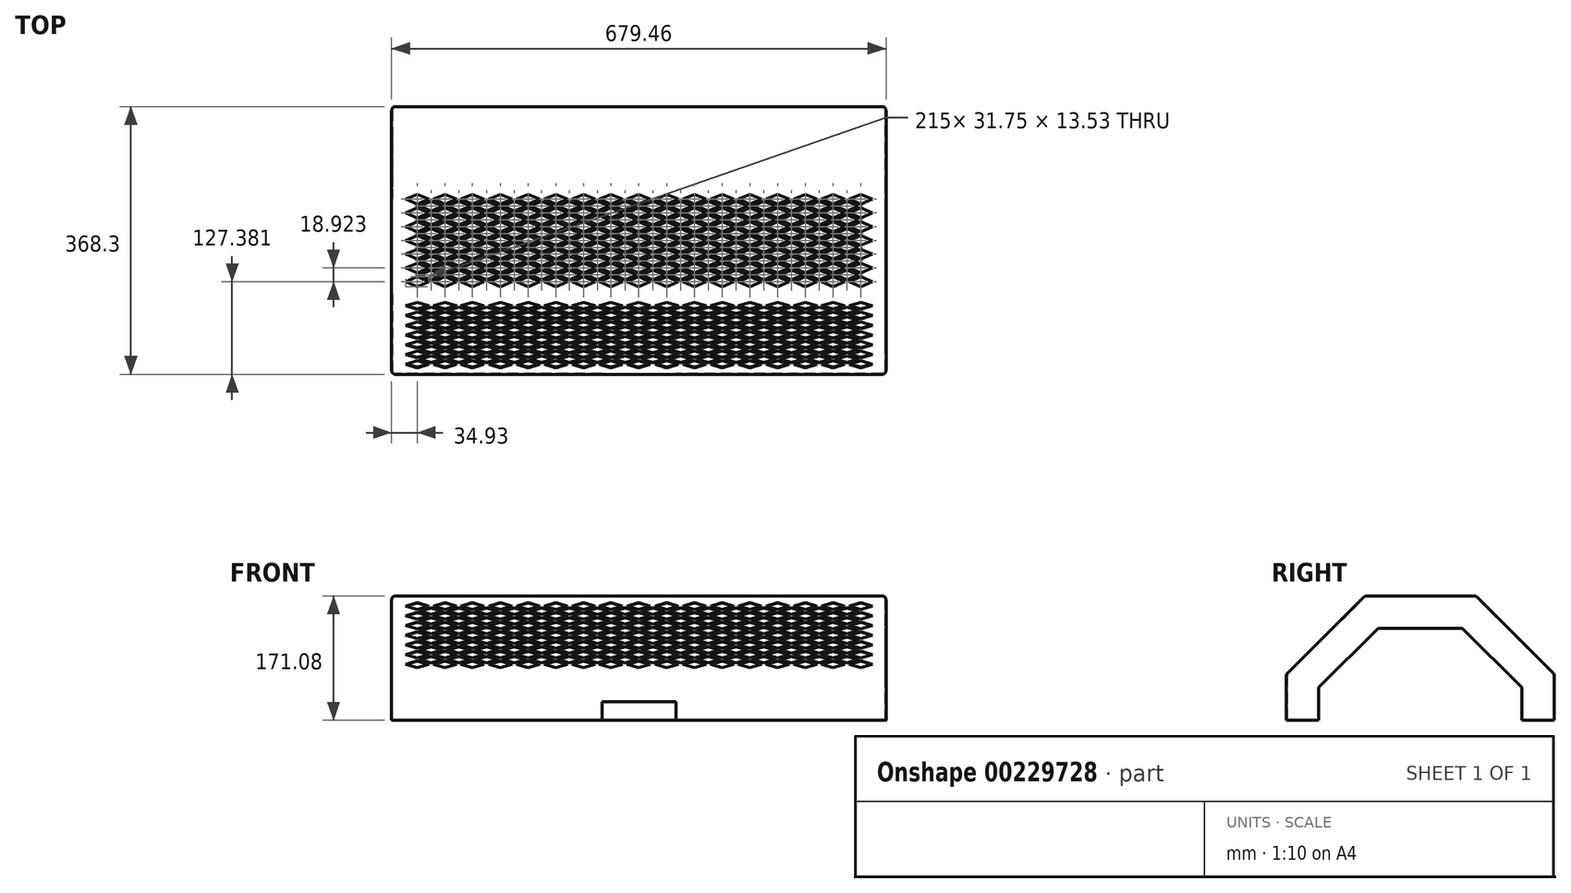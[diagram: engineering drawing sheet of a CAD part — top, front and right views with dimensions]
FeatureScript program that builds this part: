
annotation { "Feature Type Name" : "Feature", "Feature Type Description" : "" }
export const myFeature = defineFeature(function(context is Context, id is Id, definition is map)
    precondition{}
    {
        {
            var Q0;
            Q0=qCreatedBy(makeId("Right.planeOp"),FACE);
            var sketch = newSketch(context, id + "F0", { "sketchPlane" : qUnion([Q0])});
            skLineSegment(sketch, "E0", {"start": v(0, 0) * mm, "end": v(0, 333.95) * mm, "construction": true});
            skLineSegment(sketch, "E1", {"start": v(184.15, 0) * mm, "end": v(184.15, 63.5) * mm});
            skLineSegment(sketch, "E2", {"start": v(184.15, 63.5) * mm, "end": v(76.2, 171.08) * mm});
            skLineSegment(sketch, "E3", {"start": v(76.2, 171.08) * mm, "end": v(0, 171.08) * mm});
            skLineSegment(sketch, "E4", {"start": v(184.15, 0) * mm, "end": v(139.7, 0) * mm});
            skLineSegment(sketch, "E5", {"start": v(139.7, 0) * mm, "end": v(139.7, 45.04) * mm});
            skLineSegment(sketch, "E6", {"start": v(139.7, 45.04) * mm, "end": v(57.83, 126.63) * mm});
            skLineSegment(sketch, "E7", {"start": v(57.83, 126.63) * mm, "end": v(0, 126.63) * mm});
            skLineSegment(sketch, "E8.MirrorCS", {"start": v(-139.7, 45.04) * mm, "end": v(-57.83, 126.63) * mm});
            skLineSegment(sketch, "E9.MirrorCS", {"start": v(-184.15, 0) * mm, "end": v(-184.15, 63.5) * mm});
            skLineSegment(sketch, "E10.MirrorCS", {"start": v(-139.7, 0) * mm, "end": v(-139.7, 45.04) * mm});
            skLineSegment(sketch, "E11.MirrorCS", {"start": v(-76.2, 171.08) * mm, "end": v(0, 171.08) * mm});
            skLineSegment(sketch, "E12.MirrorCS", {"start": v(-57.83, 126.63) * mm, "end": v(0, 126.63) * mm});
            skLineSegment(sketch, "E13.MirrorCS", {"start": v(-184.15, 63.5) * mm, "end": v(-76.2, 171.08) * mm});
            skLineSegment(sketch, "E14.MirrorCS", {"start": v(-184.15, 0) * mm, "end": v(-139.7, 0) * mm});
            skSolve(sketch);
        }
        {
            var Q0;
            Q0 = qSketchRegion(id + "F0", true);
            extrude(context, id + "F1", {"entities" : qUnion([Q0]), "endBound" : BoundingType.SYMMETRIC, "depth" : 679.45 * mm});
        }
        {
            var Q0;
            Q0=makeQuery(id+"F1.opExtrude","SWEPT_EDGE",EDGE,{"disambiguationData":[OSD([sQuery(id+"F0.wireOp",EDGE,"E11.MirrorCS"),sQuery(id+"F0.wireOp",EDGE,"E13.MirrorCS")])]});
            var Q1;
            Q1=makeQuery(id+"F1.opExtrude","SWEPT_EDGE",EDGE,{"disambiguationData":[OSD([sQuery(id+"F0.wireOp",EDGE,"E2"),sQuery(id+"F0.wireOp",EDGE,"E3")])]});
            var Q2;
            Q2=makeQuery(id+"F1.opExtrude","SWEPT_EDGE",EDGE,{"disambiguationData":[OSD([sQuery(id+"F0.wireOp",EDGE,"E1"),sQuery(id+"F0.wireOp",EDGE,"E2")])]});
            var Q3;
            Q3=makeQuery(id+"F1.opExtrude","CAP_EDGE",EDGE,{"disambiguationData":[OSD([sQuery(id+"F0.wireOp",EDGE,"E1")])],"isStart":false});
            var Q4;
            Q4=makeQuery(id+"F1.opExtrude","CAP_EDGE",EDGE,{"disambiguationData":[OSD([sQuery(id+"F0.wireOp",EDGE,"E2")])],"isStart":false});
            var Q5;
            Q5=makeQuery(id+"F1.opExtrude","CAP_EDGE",EDGE,{"disambiguationData":[OSD([sQuery(id+"F0.wireOp",EDGE,"E3"),sQuery(id+"F0.wireOp",EDGE,"E11.MirrorCS")])],"isStart":false});
            var Q6;
            Q6=makeQuery(id+"F1.opExtrude","SWEPT_EDGE",EDGE,{"disambiguationData":[OSD([sQuery(id+"F0.wireOp",EDGE,"E9.MirrorCS"),sQuery(id+"F0.wireOp",EDGE,"E13.MirrorCS")])]});
            var Q7;
            Q7=makeQuery(id+"F1.opExtrude","CAP_EDGE",EDGE,{"disambiguationData":[OSD([sQuery(id+"F0.wireOp",EDGE,"E13.MirrorCS")])],"isStart":false});
            var Q8;
            Q8=makeQuery(id+"F1.opExtrude","CAP_EDGE",EDGE,{"disambiguationData":[OSD([sQuery(id+"F0.wireOp",EDGE,"E9.MirrorCS")])],"isStart":false});
            var Q9;
            Q9=makeQuery(id+"F1.opExtrude","CAP_EDGE",EDGE,{"disambiguationData":[OSD([sQuery(id+"F0.wireOp",EDGE,"E1")])],"isStart":true});
            var Q10;
            Q10=makeQuery(id+"F1.opExtrude","CAP_EDGE",EDGE,{"disambiguationData":[OSD([sQuery(id+"F0.wireOp",EDGE,"E2")])],"isStart":true});
            var Q11;
            Q11=makeQuery(id+"F1.opExtrude","CAP_EDGE",EDGE,{"disambiguationData":[OSD([sQuery(id+"F0.wireOp",EDGE,"E3"),sQuery(id+"F0.wireOp",EDGE,"E11.MirrorCS")])],"isStart":true});
            var Q12;
            Q12=makeQuery(id+"F1.opExtrude","CAP_EDGE",EDGE,{"disambiguationData":[OSD([sQuery(id+"F0.wireOp",EDGE,"E13.MirrorCS")])],"isStart":true});
            var Q13;
            Q13=makeQuery(id+"F1.opExtrude","CAP_EDGE",EDGE,{"disambiguationData":[OSD([sQuery(id+"F0.wireOp",EDGE,"E9.MirrorCS")])],"isStart":true});
            fillet(context, id + "F2", {"entities" : qUnion([Q0, Q1, Q2, Q3, Q4, Q5, Q6, Q7, Q8, Q9, Q10, Q11, Q12, Q13]), "radius" : 5.08 * mm, "tangentPropagation" : true, "allowEdgeOverflow" : false});
        }
        {
            var Q0;
            Q0=makeQuery(id+"F1.opExtrude","SWEPT_FACE",FACE,{"disambiguationData":[OSD([sQuery(id+"F0.wireOp",EDGE,"E4")])]});
            var Q1;
            Q1=makeQuery(id+"F1.opExtrude","SWEPT_FACE",FACE,{"disambiguationData":[OSD([sQuery(id+"F0.wireOp",EDGE,"E5")])]});
            var Q2;
            Q2=makeQuery(id+"F1.opExtrude","SWEPT_FACE",FACE,{"disambiguationData":[OSD([sQuery(id+"F0.wireOp",EDGE,"E6")])]});
            var Q3;
            Q3=makeQuery(id+"F1.opExtrude","SWEPT_FACE",FACE,{"disambiguationData":[OSD([sQuery(id+"F0.wireOp",EDGE,"E7"),sQuery(id+"F0.wireOp",EDGE,"E12.MirrorCS")])]});
            var Q4;
            Q4=makeQuery(id+"F1.opExtrude","SWEPT_FACE",FACE,{"disambiguationData":[OSD([sQuery(id+"F0.wireOp",EDGE,"E8.MirrorCS")])]});
            var Q5;
            Q5=makeQuery(id+"F1.opExtrude","SWEPT_FACE",FACE,{"disambiguationData":[OSD([sQuery(id+"F0.wireOp",EDGE,"E14.MirrorCS")])]});
            var Q6;
            Q6=makeQuery(id+"F1.opExtrude","SWEPT_FACE",FACE,{"disambiguationData":[OSD([sQuery(id+"F0.wireOp",EDGE,"E10.MirrorCS")])]});
            shell(context, id + "F3", {"entities" : qUnion([Q0, Q1, Q2, Q3, Q4, Q5, Q6]), "thickness" : 0.95 * mm});
        }
        {
            var Q0;
            Q0=makeQuery(id+"F1.opExtrude","SWEPT_FACE",FACE,{"disambiguationData":[OSD([sQuery(id+"F0.wireOp",EDGE,"E9.MirrorCS")])]});
            var sketch = newSketch(context, id + "F4", { "sketchPlane" : qUnion([Q0])});
            skLineSegment(sketch, "E15.bottom", {"start": v(-50.8, 0) * mm, "end": v(50.8, 0) * mm});
            skLineSegment(sketch, "E15.top", {"start": v(-50.8, 25.4) * mm, "end": v(50.8, 25.4) * mm});
            skLineSegment(sketch, "E15.left", {"start": v(-50.8, 0) * mm, "end": v(-50.8, 25.4) * mm});
            skLineSegment(sketch, "E15.right", {"start": v(50.8, 0) * mm, "end": v(50.8, 25.4) * mm});
            skSolve(sketch);
        }
        {
            var Q0;
            Q0 = qSketchRegion(id + "F4", true);
            extrude(context, id + "F5", {"entities" : qUnion([Q0]), "operationType" : NewBodyOperationType.REMOVE, "oppositeDirection" : true, "depth" : 25.4 * mm});
        }
        {
            var Q0;
            Q0=makeQuery(id+"F1.opExtrude","SWEPT_FACE",FACE,{"disambiguationData":[OSD([sQuery(id+"F0.wireOp",EDGE,"E3"),sQuery(id+"F0.wireOp",EDGE,"E11.MirrorCS")])]});
            var sketch = newSketch(context, id + "F6", { "sketchPlane" : qUnion([Q0])});
            skLineSegment(sketch, "E16", {"start": v(-15.88, 0) * mm, "end": v(0, 6.76) * mm});
            skLineSegment(sketch, "E17", {"start": v(0, 6.76) * mm, "end": v(15.88, 0) * mm});
            skLineSegment(sketch, "E18", {"start": v(15.88, 0) * mm, "end": v(0, -6.76) * mm});
            skLineSegment(sketch, "E19", {"start": v(0, -6.76) * mm, "end": v(-15.88, 0) * mm});
            skLineSegment(sketch, "E20.0.1.0", {"start": v(15.88, 18.92) * mm, "end": v(0, 12.16) * mm});
            skLineSegment(sketch, "E20.0.1.1", {"start": v(0, 25.69) * mm, "end": v(15.88, 18.92) * mm});
            skLineSegment(sketch, "E20.0.1.2", {"start": v(-15.88, 18.92) * mm, "end": v(0, 25.69) * mm});
            skLineSegment(sketch, "E20.0.1.3", {"start": v(0, 12.16) * mm, "end": v(-15.88, 18.92) * mm});
            skLineSegment(sketch, "E20.0.2.0", {"start": v(15.88, 37.85) * mm, "end": v(0, 31.08) * mm});
            skLineSegment(sketch, "E20.0.2.1", {"start": v(0, 44.6) * mm, "end": v(15.88, 37.85) * mm});
            skLineSegment(sketch, "E20.0.2.2", {"start": v(-15.88, 37.85) * mm, "end": v(0, 44.6) * mm});
            skLineSegment(sketch, "E20.0.2.3", {"start": v(0, 31.08) * mm, "end": v(-15.87, 37.85) * mm});
            skLineSegment(sketch, "E20.0.3.0", {"start": v(15.88, 56.77) * mm, "end": v(0, 50) * mm});
            skLineSegment(sketch, "E20.0.3.1", {"start": v(0, 63.53) * mm, "end": v(15.88, 56.77) * mm});
            skLineSegment(sketch, "E20.0.3.2", {"start": v(-15.88, 56.77) * mm, "end": v(0, 63.53) * mm});
            skLineSegment(sketch, "E20.0.3.3", {"start": v(0, 50) * mm, "end": v(-15.87, 56.77) * mm});
            skLineSegment(sketch, "E20.1.0.0", {"start": v(53.98, 0) * mm, "end": v(38.1, -6.76) * mm});
            skLineSegment(sketch, "E20.1.0.1", {"start": v(38.1, 6.76) * mm, "end": v(53.98, 0) * mm});
            skLineSegment(sketch, "E20.1.0.2", {"start": v(22.22, 0) * mm, "end": v(38.1, 6.76) * mm});
            skLineSegment(sketch, "E20.1.0.3", {"start": v(38.1, -6.76) * mm, "end": v(22.23, 0) * mm});
            skLineSegment(sketch, "E20.1.1.0", {"start": v(53.98, 18.92) * mm, "end": v(38.1, 12.16) * mm});
            skLineSegment(sketch, "E20.1.1.1", {"start": v(38.1, 25.69) * mm, "end": v(53.98, 18.92) * mm});
            skLineSegment(sketch, "E20.1.1.2", {"start": v(22.22, 18.92) * mm, "end": v(38.1, 25.69) * mm});
            skLineSegment(sketch, "E20.1.1.3", {"start": v(38.1, 12.16) * mm, "end": v(22.23, 18.92) * mm});
            skLineSegment(sketch, "E20.1.2.0", {"start": v(53.98, 37.85) * mm, "end": v(38.1, 31.08) * mm});
            skLineSegment(sketch, "E20.1.2.1", {"start": v(38.1, 44.6) * mm, "end": v(53.98, 37.85) * mm});
            skLineSegment(sketch, "E20.1.2.2", {"start": v(22.22, 37.85) * mm, "end": v(38.1, 44.6) * mm});
            skLineSegment(sketch, "E20.1.2.3", {"start": v(38.1, 31.08) * mm, "end": v(22.23, 37.85) * mm});
            skLineSegment(sketch, "E20.1.3.0", {"start": v(53.98, 56.77) * mm, "end": v(38.1, 50) * mm});
            skLineSegment(sketch, "E20.1.3.1", {"start": v(38.1, 63.53) * mm, "end": v(53.98, 56.77) * mm});
            skLineSegment(sketch, "E20.1.3.2", {"start": v(22.22, 56.77) * mm, "end": v(38.1, 63.53) * mm});
            skLineSegment(sketch, "E20.1.3.3", {"start": v(38.1, 50) * mm, "end": v(22.23, 56.77) * mm});
            skLineSegment(sketch, "E20.2.0.0", {"start": v(92.08, 0) * mm, "end": v(76.2, -6.76) * mm});
            skLineSegment(sketch, "E20.2.0.1", {"start": v(76.2, 6.76) * mm, "end": v(92.08, 0) * mm});
            skLineSegment(sketch, "E20.2.0.2", {"start": v(60.33, 0) * mm, "end": v(76.2, 6.76) * mm});
            skLineSegment(sketch, "E20.2.0.3", {"start": v(76.2, -6.76) * mm, "end": v(60.33, 0) * mm});
            skLineSegment(sketch, "E20.2.1.0", {"start": v(92.08, 18.92) * mm, "end": v(76.2, 12.16) * mm});
            skLineSegment(sketch, "E20.2.1.1", {"start": v(76.2, 25.69) * mm, "end": v(92.08, 18.92) * mm});
            skLineSegment(sketch, "E20.2.1.2", {"start": v(60.33, 18.92) * mm, "end": v(76.2, 25.69) * mm});
            skLineSegment(sketch, "E20.2.1.3", {"start": v(76.2, 12.16) * mm, "end": v(60.33, 18.92) * mm});
            skLineSegment(sketch, "E20.2.2.0", {"start": v(92.08, 37.85) * mm, "end": v(76.2, 31.08) * mm});
            skLineSegment(sketch, "E20.2.2.1", {"start": v(76.2, 44.6) * mm, "end": v(92.08, 37.85) * mm});
            skLineSegment(sketch, "E20.2.2.2", {"start": v(60.33, 37.85) * mm, "end": v(76.2, 44.6) * mm});
            skLineSegment(sketch, "E20.2.2.3", {"start": v(76.2, 31.08) * mm, "end": v(60.33, 37.85) * mm});
            skLineSegment(sketch, "E20.2.3.0", {"start": v(92.08, 56.77) * mm, "end": v(76.2, 50) * mm});
            skLineSegment(sketch, "E20.2.3.1", {"start": v(76.2, 63.53) * mm, "end": v(92.08, 56.77) * mm});
            skLineSegment(sketch, "E20.2.3.2", {"start": v(60.33, 56.77) * mm, "end": v(76.2, 63.53) * mm});
            skLineSegment(sketch, "E20.2.3.3", {"start": v(76.2, 50) * mm, "end": v(60.33, 56.77) * mm});
            skLineSegment(sketch, "E20.3.0.0", {"start": v(130.18, 0) * mm, "end": v(114.3, -6.76) * mm});
            skLineSegment(sketch, "E20.3.0.1", {"start": v(114.3, 6.76) * mm, "end": v(130.18, 0) * mm});
            skLineSegment(sketch, "E20.3.0.2", {"start": v(98.43, 0) * mm, "end": v(114.3, 6.76) * mm});
            skLineSegment(sketch, "E20.3.0.3", {"start": v(114.3, -6.76) * mm, "end": v(98.43, 0) * mm});
            skLineSegment(sketch, "E20.3.1.0", {"start": v(130.18, 18.92) * mm, "end": v(114.3, 12.16) * mm});
            skLineSegment(sketch, "E20.3.1.1", {"start": v(114.3, 25.69) * mm, "end": v(130.18, 18.92) * mm});
            skLineSegment(sketch, "E20.3.1.2", {"start": v(98.43, 18.92) * mm, "end": v(114.3, 25.69) * mm});
            skLineSegment(sketch, "E20.3.1.3", {"start": v(114.3, 12.16) * mm, "end": v(98.43, 18.92) * mm});
            skLineSegment(sketch, "E20.3.2.0", {"start": v(130.18, 37.85) * mm, "end": v(114.3, 31.08) * mm});
            skLineSegment(sketch, "E20.3.2.1", {"start": v(114.3, 44.6) * mm, "end": v(130.18, 37.85) * mm});
            skLineSegment(sketch, "E20.3.2.2", {"start": v(98.43, 37.85) * mm, "end": v(114.3, 44.6) * mm});
            skLineSegment(sketch, "E20.3.2.3", {"start": v(114.3, 31.08) * mm, "end": v(98.43, 37.85) * mm});
            skLineSegment(sketch, "E20.3.3.0", {"start": v(130.18, 56.77) * mm, "end": v(114.3, 50) * mm});
            skLineSegment(sketch, "E20.3.3.1", {"start": v(114.3, 63.53) * mm, "end": v(130.18, 56.77) * mm});
            skLineSegment(sketch, "E20.3.3.2", {"start": v(98.43, 56.77) * mm, "end": v(114.3, 63.53) * mm});
            skLineSegment(sketch, "E20.3.3.3", {"start": v(114.3, 50) * mm, "end": v(98.43, 56.77) * mm});
            skLineSegment(sketch, "E20.4.0.0", {"start": v(168.28, 0) * mm, "end": v(152.4, -6.76) * mm});
            skLineSegment(sketch, "E20.4.0.1", {"start": v(152.4, 6.76) * mm, "end": v(168.28, 0) * mm});
            skLineSegment(sketch, "E20.4.0.2", {"start": v(136.53, 0) * mm, "end": v(152.4, 6.76) * mm});
            skLineSegment(sketch, "E20.4.0.3", {"start": v(152.4, -6.76) * mm, "end": v(136.53, 0) * mm});
            skLineSegment(sketch, "E20.4.1.0", {"start": v(168.28, 18.92) * mm, "end": v(152.4, 12.16) * mm});
            skLineSegment(sketch, "E20.4.1.1", {"start": v(152.4, 25.69) * mm, "end": v(168.28, 18.92) * mm});
            skLineSegment(sketch, "E20.4.1.2", {"start": v(136.53, 18.92) * mm, "end": v(152.4, 25.69) * mm});
            skLineSegment(sketch, "E20.4.1.3", {"start": v(152.4, 12.16) * mm, "end": v(136.53, 18.92) * mm});
            skLineSegment(sketch, "E20.4.2.0", {"start": v(168.28, 37.85) * mm, "end": v(152.4, 31.08) * mm});
            skLineSegment(sketch, "E20.4.2.1", {"start": v(152.4, 44.6) * mm, "end": v(168.28, 37.85) * mm});
            skLineSegment(sketch, "E20.4.2.2", {"start": v(136.53, 37.85) * mm, "end": v(152.4, 44.6) * mm});
            skLineSegment(sketch, "E20.4.2.3", {"start": v(152.4, 31.08) * mm, "end": v(136.53, 37.85) * mm});
            skLineSegment(sketch, "E20.4.3.0", {"start": v(168.28, 56.77) * mm, "end": v(152.4, 50) * mm});
            skLineSegment(sketch, "E20.4.3.1", {"start": v(152.4, 63.53) * mm, "end": v(168.28, 56.77) * mm});
            skLineSegment(sketch, "E20.4.3.2", {"start": v(136.53, 56.77) * mm, "end": v(152.4, 63.53) * mm});
            skLineSegment(sketch, "E20.4.3.3", {"start": v(152.4, 50) * mm, "end": v(136.53, 56.77) * mm});
            skLineSegment(sketch, "E20.5.0.0", {"start": v(206.38, 0) * mm, "end": v(190.5, -6.76) * mm});
            skLineSegment(sketch, "E20.5.0.1", {"start": v(190.5, 6.76) * mm, "end": v(206.38, 0) * mm});
            skLineSegment(sketch, "E20.5.0.2", {"start": v(174.62, 0) * mm, "end": v(190.5, 6.76) * mm});
            skLineSegment(sketch, "E20.5.0.3", {"start": v(190.5, -6.76) * mm, "end": v(174.62, 0) * mm});
            skLineSegment(sketch, "E20.5.1.0", {"start": v(206.38, 18.92) * mm, "end": v(190.5, 12.16) * mm});
            skLineSegment(sketch, "E20.5.1.1", {"start": v(190.5, 25.69) * mm, "end": v(206.38, 18.92) * mm});
            skLineSegment(sketch, "E20.5.1.2", {"start": v(174.62, 18.92) * mm, "end": v(190.5, 25.69) * mm});
            skLineSegment(sketch, "E20.5.1.3", {"start": v(190.5, 12.16) * mm, "end": v(174.62, 18.92) * mm});
            skLineSegment(sketch, "E20.5.2.0", {"start": v(206.38, 37.85) * mm, "end": v(190.5, 31.08) * mm});
            skLineSegment(sketch, "E20.5.2.1", {"start": v(190.5, 44.6) * mm, "end": v(206.38, 37.85) * mm});
            skLineSegment(sketch, "E20.5.2.2", {"start": v(174.62, 37.85) * mm, "end": v(190.5, 44.6) * mm});
            skLineSegment(sketch, "E20.5.2.3", {"start": v(190.5, 31.08) * mm, "end": v(174.62, 37.85) * mm});
            skLineSegment(sketch, "E20.5.3.0", {"start": v(206.38, 56.77) * mm, "end": v(190.5, 50) * mm});
            skLineSegment(sketch, "E20.5.3.1", {"start": v(190.5, 63.53) * mm, "end": v(206.38, 56.77) * mm});
            skLineSegment(sketch, "E20.5.3.2", {"start": v(174.62, 56.77) * mm, "end": v(190.5, 63.53) * mm});
            skLineSegment(sketch, "E20.5.3.3", {"start": v(190.5, 50) * mm, "end": v(174.62, 56.77) * mm});
            skLineSegment(sketch, "E20.6.0.0", {"start": v(244.48, 0) * mm, "end": v(228.6, -6.76) * mm});
            skLineSegment(sketch, "E20.6.0.1", {"start": v(228.6, 6.76) * mm, "end": v(244.48, 0) * mm});
            skLineSegment(sketch, "E20.6.0.2", {"start": v(212.73, 0) * mm, "end": v(228.6, 6.76) * mm});
            skLineSegment(sketch, "E20.6.0.3", {"start": v(228.6, -6.76) * mm, "end": v(212.73, 0) * mm});
            skLineSegment(sketch, "E20.6.1.0", {"start": v(244.48, 18.92) * mm, "end": v(228.6, 12.16) * mm});
            skLineSegment(sketch, "E20.6.1.1", {"start": v(228.6, 25.69) * mm, "end": v(244.48, 18.92) * mm});
            skLineSegment(sketch, "E20.6.1.2", {"start": v(212.73, 18.92) * mm, "end": v(228.6, 25.69) * mm});
            skLineSegment(sketch, "E20.6.1.3", {"start": v(228.6, 12.16) * mm, "end": v(212.73, 18.92) * mm});
            skLineSegment(sketch, "E20.6.2.0", {"start": v(244.48, 37.85) * mm, "end": v(228.6, 31.08) * mm});
            skLineSegment(sketch, "E20.6.2.1", {"start": v(228.6, 44.6) * mm, "end": v(244.48, 37.85) * mm});
            skLineSegment(sketch, "E20.6.2.2", {"start": v(212.73, 37.85) * mm, "end": v(228.6, 44.6) * mm});
            skLineSegment(sketch, "E20.6.2.3", {"start": v(228.6, 31.08) * mm, "end": v(212.73, 37.85) * mm});
            skLineSegment(sketch, "E20.6.3.0", {"start": v(244.48, 56.77) * mm, "end": v(228.6, 50) * mm});
            skLineSegment(sketch, "E20.6.3.1", {"start": v(228.6, 63.53) * mm, "end": v(244.48, 56.77) * mm});
            skLineSegment(sketch, "E20.6.3.2", {"start": v(212.73, 56.77) * mm, "end": v(228.6, 63.53) * mm});
            skLineSegment(sketch, "E20.6.3.3", {"start": v(228.6, 50) * mm, "end": v(212.73, 56.77) * mm});
            skLineSegment(sketch, "E20.7.0.0", {"start": v(282.58, 0) * mm, "end": v(266.7, -6.76) * mm});
            skLineSegment(sketch, "E20.7.0.1", {"start": v(266.7, 6.76) * mm, "end": v(282.58, 0) * mm});
            skLineSegment(sketch, "E20.7.0.2", {"start": v(250.82, 0) * mm, "end": v(266.7, 6.76) * mm});
            skLineSegment(sketch, "E20.7.0.3", {"start": v(266.7, -6.76) * mm, "end": v(250.83, 0) * mm});
            skLineSegment(sketch, "E20.7.1.0", {"start": v(282.58, 18.92) * mm, "end": v(266.7, 12.16) * mm});
            skLineSegment(sketch, "E20.7.1.1", {"start": v(266.7, 25.69) * mm, "end": v(282.58, 18.92) * mm});
            skLineSegment(sketch, "E20.7.1.2", {"start": v(250.82, 18.92) * mm, "end": v(266.7, 25.69) * mm});
            skLineSegment(sketch, "E20.7.1.3", {"start": v(266.7, 12.16) * mm, "end": v(250.83, 18.92) * mm});
            skLineSegment(sketch, "E20.7.2.0", {"start": v(282.58, 37.85) * mm, "end": v(266.7, 31.08) * mm});
            skLineSegment(sketch, "E20.7.2.1", {"start": v(266.7, 44.6) * mm, "end": v(282.58, 37.85) * mm});
            skLineSegment(sketch, "E20.7.2.2", {"start": v(250.82, 37.85) * mm, "end": v(266.7, 44.6) * mm});
            skLineSegment(sketch, "E20.7.2.3", {"start": v(266.7, 31.08) * mm, "end": v(250.83, 37.85) * mm});
            skLineSegment(sketch, "E20.7.3.0", {"start": v(282.58, 56.77) * mm, "end": v(266.7, 50) * mm});
            skLineSegment(sketch, "E20.7.3.1", {"start": v(266.7, 63.53) * mm, "end": v(282.58, 56.77) * mm});
            skLineSegment(sketch, "E20.7.3.2", {"start": v(250.82, 56.77) * mm, "end": v(266.7, 63.53) * mm});
            skLineSegment(sketch, "E20.7.3.3", {"start": v(266.7, 50) * mm, "end": v(250.83, 56.77) * mm});
            skLineSegment(sketch, "E20.8.0.0", {"start": v(320.68, 0) * mm, "end": v(304.8, -6.76) * mm});
            skLineSegment(sketch, "E20.8.0.1", {"start": v(304.8, 6.76) * mm, "end": v(320.68, 0) * mm});
            skLineSegment(sketch, "E20.8.0.2", {"start": v(288.93, 0) * mm, "end": v(304.8, 6.76) * mm});
            skLineSegment(sketch, "E20.8.0.3", {"start": v(304.8, -6.76) * mm, "end": v(288.93, 0) * mm});
            skLineSegment(sketch, "E20.8.1.0", {"start": v(320.68, 18.92) * mm, "end": v(304.8, 12.16) * mm});
            skLineSegment(sketch, "E20.8.1.1", {"start": v(304.8, 25.69) * mm, "end": v(320.68, 18.92) * mm});
            skLineSegment(sketch, "E20.8.1.2", {"start": v(288.93, 18.92) * mm, "end": v(304.8, 25.69) * mm});
            skLineSegment(sketch, "E20.8.1.3", {"start": v(304.8, 12.16) * mm, "end": v(288.93, 18.92) * mm});
            skLineSegment(sketch, "E20.8.2.0", {"start": v(320.68, 37.85) * mm, "end": v(304.8, 31.08) * mm});
            skLineSegment(sketch, "E20.8.2.1", {"start": v(304.8, 44.6) * mm, "end": v(320.68, 37.85) * mm});
            skLineSegment(sketch, "E20.8.2.2", {"start": v(288.93, 37.85) * mm, "end": v(304.8, 44.6) * mm});
            skLineSegment(sketch, "E20.8.2.3", {"start": v(304.8, 31.08) * mm, "end": v(288.93, 37.85) * mm});
            skLineSegment(sketch, "E20.8.3.0", {"start": v(320.68, 56.77) * mm, "end": v(304.8, 50) * mm});
            skLineSegment(sketch, "E20.8.3.1", {"start": v(304.8, 63.53) * mm, "end": v(320.68, 56.77) * mm});
            skLineSegment(sketch, "E20.8.3.2", {"start": v(288.93, 56.77) * mm, "end": v(304.8, 63.53) * mm});
            skLineSegment(sketch, "E20.8.3.3", {"start": v(304.8, 50) * mm, "end": v(288.93, 56.77) * mm});
            skLineSegment(sketch, "E20.direction1", {"start": v(-15.88, 0) * mm, "end": v(22.23, 0) * mm, "construction": true});
            skLineSegment(sketch, "E20.direction2", {"start": v(-15.88, 0) * mm, "end": v(-15.88, 18.92) * mm, "construction": true});
            skLineSegment(sketch, "E21.0.1.0", {"start": v(228.6, -25.69) * mm, "end": v(212.73, -18.92) * mm});
            skLineSegment(sketch, "E21.0.1.1", {"start": v(174.62, -18.92) * mm, "end": v(190.5, -12.16) * mm});
            skLineSegment(sketch, "E21.0.1.2", {"start": v(38.1, -25.69) * mm, "end": v(22.23, -18.92) * mm});
            skLineSegment(sketch, "E21.0.1.3", {"start": v(76.2, -25.69) * mm, "end": v(60.33, -18.92) * mm});
            skLineSegment(sketch, "E21.0.1.4", {"start": v(114.3, -25.69) * mm, "end": v(98.43, -18.92) * mm});
            skLineSegment(sketch, "E21.0.1.5", {"start": v(60.33, -18.92) * mm, "end": v(76.2, -12.16) * mm});
            skLineSegment(sketch, "E21.0.1.6", {"start": v(190.5, -25.69) * mm, "end": v(174.62, -18.92) * mm});
            skLineSegment(sketch, "E21.0.1.7", {"start": v(266.7, -25.69) * mm, "end": v(250.83, -18.92) * mm});
            skLineSegment(sketch, "E21.0.1.8", {"start": v(304.8, -25.69) * mm, "end": v(288.93, -18.92) * mm});
            skLineSegment(sketch, "E21.0.1.9", {"start": v(98.43, -18.92) * mm, "end": v(114.3, -12.16) * mm});
            skLineSegment(sketch, "E21.0.1.10", {"start": v(136.53, -18.92) * mm, "end": v(152.4, -12.16) * mm});
            skLineSegment(sketch, "E21.0.1.11", {"start": v(22.22, -18.92) * mm, "end": v(38.1, -12.16) * mm});
            skLineSegment(sketch, "E21.0.1.12", {"start": v(152.4, -25.69) * mm, "end": v(136.53, -18.92) * mm});
            skLineSegment(sketch, "E21.0.1.13", {"start": v(250.82, -18.92) * mm, "end": v(266.7, -12.16) * mm});
            skLineSegment(sketch, "E21.0.1.14", {"start": v(288.93, -18.92) * mm, "end": v(304.8, -12.16) * mm});
            skLineSegment(sketch, "E21.0.1.15", {"start": v(212.73, -18.92) * mm, "end": v(228.6, -12.16) * mm});
            skLineSegment(sketch, "E21.0.1.16", {"start": v(206.38, -18.92) * mm, "end": v(190.5, -25.69) * mm});
            skLineSegment(sketch, "E21.0.1.17", {"start": v(53.98, -18.92) * mm, "end": v(38.1, -25.69) * mm});
            skLineSegment(sketch, "E21.0.1.18", {"start": v(92.08, -18.92) * mm, "end": v(76.2, -25.69) * mm});
            skLineSegment(sketch, "E21.0.1.19", {"start": v(130.18, -18.92) * mm, "end": v(114.3, -25.69) * mm});
            skLineSegment(sketch, "E21.0.1.20", {"start": v(244.48, -18.92) * mm, "end": v(228.6, -25.69) * mm});
            skLineSegment(sketch, "E21.0.1.21", {"start": v(168.28, -18.92) * mm, "end": v(152.4, -25.69) * mm});
            skLineSegment(sketch, "E21.0.1.22", {"start": v(282.58, -18.92) * mm, "end": v(266.7, -25.69) * mm});
            skLineSegment(sketch, "E21.0.1.23", {"start": v(190.5, -12.16) * mm, "end": v(206.38, -18.92) * mm});
            skLineSegment(sketch, "E21.0.1.24", {"start": v(228.6, -12.16) * mm, "end": v(244.48, -18.92) * mm});
            skLineSegment(sketch, "E21.0.1.25", {"start": v(266.7, -12.16) * mm, "end": v(282.58, -18.92) * mm});
            skLineSegment(sketch, "E21.0.1.26", {"start": v(304.8, -12.16) * mm, "end": v(320.68, -18.92) * mm});
            skLineSegment(sketch, "E21.0.1.27", {"start": v(38.1, -12.16) * mm, "end": v(53.98, -18.92) * mm});
            skLineSegment(sketch, "E21.0.1.28", {"start": v(76.2, -12.16) * mm, "end": v(92.08, -18.92) * mm});
            skLineSegment(sketch, "E21.0.1.29", {"start": v(114.3, -12.16) * mm, "end": v(130.18, -18.92) * mm});
            skLineSegment(sketch, "E21.0.1.30", {"start": v(152.4, -12.16) * mm, "end": v(168.28, -18.92) * mm});
            skLineSegment(sketch, "E21.0.1.31", {"start": v(320.68, -18.92) * mm, "end": v(304.8, -25.69) * mm});
            skLineSegment(sketch, "E21.0.1.32", {"start": v(-15.88, -18.92) * mm, "end": v(0, -12.16) * mm});
            skLineSegment(sketch, "E21.0.1.33", {"start": v(0, -12.16) * mm, "end": v(15.88, -18.92) * mm});
            skLineSegment(sketch, "E21.0.1.34", {"start": v(15.88, -18.92) * mm, "end": v(0, -25.69) * mm});
            skLineSegment(sketch, "E21.0.1.35", {"start": v(0, -25.69) * mm, "end": v(-15.88, -18.92) * mm});
            skLineSegment(sketch, "E21.0.2.0", {"start": v(228.6, -44.6) * mm, "end": v(212.73, -37.85) * mm});
            skLineSegment(sketch, "E21.0.2.1", {"start": v(174.62, -37.85) * mm, "end": v(190.5, -31.08) * mm});
            skLineSegment(sketch, "E21.0.2.2", {"start": v(38.1, -44.6) * mm, "end": v(22.23, -37.85) * mm});
            skLineSegment(sketch, "E21.0.2.3", {"start": v(76.2, -44.6) * mm, "end": v(60.33, -37.85) * mm});
            skLineSegment(sketch, "E21.0.2.4", {"start": v(114.3, -44.6) * mm, "end": v(98.43, -37.85) * mm});
            skLineSegment(sketch, "E21.0.2.5", {"start": v(60.33, -37.85) * mm, "end": v(76.2, -31.08) * mm});
            skLineSegment(sketch, "E21.0.2.6", {"start": v(190.5, -44.6) * mm, "end": v(174.62, -37.85) * mm});
            skLineSegment(sketch, "E21.0.2.7", {"start": v(266.7, -44.6) * mm, "end": v(250.83, -37.85) * mm});
            skLineSegment(sketch, "E21.0.2.8", {"start": v(304.8, -44.6) * mm, "end": v(288.93, -37.85) * mm});
            skLineSegment(sketch, "E21.0.2.9", {"start": v(98.43, -37.85) * mm, "end": v(114.3, -31.08) * mm});
            skLineSegment(sketch, "E21.0.2.10", {"start": v(136.53, -37.85) * mm, "end": v(152.4, -31.08) * mm});
            skLineSegment(sketch, "E21.0.2.11", {"start": v(22.22, -37.85) * mm, "end": v(38.1, -31.08) * mm});
            skLineSegment(sketch, "E21.0.2.12", {"start": v(152.4, -44.6) * mm, "end": v(136.53, -37.85) * mm});
            skLineSegment(sketch, "E21.0.2.13", {"start": v(250.82, -37.85) * mm, "end": v(266.7, -31.08) * mm});
            skLineSegment(sketch, "E21.0.2.14", {"start": v(288.93, -37.85) * mm, "end": v(304.8, -31.08) * mm});
            skLineSegment(sketch, "E21.0.2.15", {"start": v(212.73, -37.85) * mm, "end": v(228.6, -31.08) * mm});
            skLineSegment(sketch, "E21.0.2.16", {"start": v(206.38, -37.85) * mm, "end": v(190.5, -44.6) * mm});
            skLineSegment(sketch, "E21.0.2.17", {"start": v(53.98, -37.85) * mm, "end": v(38.1, -44.6) * mm});
            skLineSegment(sketch, "E21.0.2.18", {"start": v(92.08, -37.85) * mm, "end": v(76.2, -44.6) * mm});
            skLineSegment(sketch, "E21.0.2.19", {"start": v(130.18, -37.85) * mm, "end": v(114.3, -44.6) * mm});
            skLineSegment(sketch, "E21.0.2.20", {"start": v(244.48, -37.85) * mm, "end": v(228.6, -44.6) * mm});
            skLineSegment(sketch, "E21.0.2.21", {"start": v(168.28, -37.85) * mm, "end": v(152.4, -44.6) * mm});
            skLineSegment(sketch, "E21.0.2.22", {"start": v(282.58, -37.85) * mm, "end": v(266.7, -44.6) * mm});
            skLineSegment(sketch, "E21.0.2.23", {"start": v(190.5, -31.08) * mm, "end": v(206.38, -37.85) * mm});
            skLineSegment(sketch, "E21.0.2.24", {"start": v(228.6, -31.08) * mm, "end": v(244.48, -37.85) * mm});
            skLineSegment(sketch, "E21.0.2.25", {"start": v(266.7, -31.08) * mm, "end": v(282.58, -37.85) * mm});
            skLineSegment(sketch, "E21.0.2.26", {"start": v(304.8, -31.08) * mm, "end": v(320.68, -37.85) * mm});
            skLineSegment(sketch, "E21.0.2.27", {"start": v(38.1, -31.08) * mm, "end": v(53.98, -37.85) * mm});
            skLineSegment(sketch, "E21.0.2.28", {"start": v(76.2, -31.08) * mm, "end": v(92.08, -37.85) * mm});
            skLineSegment(sketch, "E21.0.2.29", {"start": v(114.3, -31.08) * mm, "end": v(130.18, -37.85) * mm});
            skLineSegment(sketch, "E21.0.2.30", {"start": v(152.4, -31.08) * mm, "end": v(168.28, -37.85) * mm});
            skLineSegment(sketch, "E21.0.2.31", {"start": v(320.68, -37.85) * mm, "end": v(304.8, -44.6) * mm});
            skLineSegment(sketch, "E21.0.2.32", {"start": v(-15.88, -37.85) * mm, "end": v(0, -31.08) * mm});
            skLineSegment(sketch, "E21.0.2.33", {"start": v(0, -31.08) * mm, "end": v(15.88, -37.85) * mm});
            skLineSegment(sketch, "E21.0.2.34", {"start": v(15.88, -37.85) * mm, "end": v(0, -44.6) * mm});
            skLineSegment(sketch, "E21.0.2.35", {"start": v(0, -44.6) * mm, "end": v(-15.87, -37.85) * mm});
            skLineSegment(sketch, "E21.0.3.0", {"start": v(228.6, -63.53) * mm, "end": v(212.73, -56.77) * mm});
            skLineSegment(sketch, "E21.0.3.1", {"start": v(174.62, -56.77) * mm, "end": v(190.5, -50) * mm});
            skLineSegment(sketch, "E21.0.3.2", {"start": v(38.1, -63.53) * mm, "end": v(22.23, -56.77) * mm});
            skLineSegment(sketch, "E21.0.3.3", {"start": v(76.2, -63.53) * mm, "end": v(60.33, -56.77) * mm});
            skLineSegment(sketch, "E21.0.3.4", {"start": v(114.3, -63.53) * mm, "end": v(98.43, -56.77) * mm});
            skLineSegment(sketch, "E21.0.3.5", {"start": v(60.33, -56.77) * mm, "end": v(76.2, -50) * mm});
            skLineSegment(sketch, "E21.0.3.6", {"start": v(190.5, -63.53) * mm, "end": v(174.62, -56.77) * mm});
            skLineSegment(sketch, "E21.0.3.7", {"start": v(266.7, -63.53) * mm, "end": v(250.83, -56.77) * mm});
            skLineSegment(sketch, "E21.0.3.8", {"start": v(304.8, -63.53) * mm, "end": v(288.93, -56.77) * mm});
            skLineSegment(sketch, "E21.0.3.9", {"start": v(98.43, -56.77) * mm, "end": v(114.3, -50) * mm});
            skLineSegment(sketch, "E21.0.3.10", {"start": v(136.53, -56.77) * mm, "end": v(152.4, -50) * mm});
            skLineSegment(sketch, "E21.0.3.11", {"start": v(22.22, -56.77) * mm, "end": v(38.1, -50) * mm});
            skLineSegment(sketch, "E21.0.3.12", {"start": v(152.4, -63.53) * mm, "end": v(136.53, -56.77) * mm});
            skLineSegment(sketch, "E21.0.3.13", {"start": v(250.82, -56.77) * mm, "end": v(266.7, -50) * mm});
            skLineSegment(sketch, "E21.0.3.14", {"start": v(288.93, -56.77) * mm, "end": v(304.8, -50) * mm});
            skLineSegment(sketch, "E21.0.3.15", {"start": v(212.73, -56.77) * mm, "end": v(228.6, -50) * mm});
            skLineSegment(sketch, "E21.0.3.16", {"start": v(206.38, -56.77) * mm, "end": v(190.5, -63.53) * mm});
            skLineSegment(sketch, "E21.0.3.17", {"start": v(53.98, -56.77) * mm, "end": v(38.1, -63.53) * mm});
            skLineSegment(sketch, "E21.0.3.18", {"start": v(92.08, -56.77) * mm, "end": v(76.2, -63.53) * mm});
            skLineSegment(sketch, "E21.0.3.19", {"start": v(130.18, -56.77) * mm, "end": v(114.3, -63.53) * mm});
            skLineSegment(sketch, "E21.0.3.20", {"start": v(244.48, -56.77) * mm, "end": v(228.6, -63.53) * mm});
            skLineSegment(sketch, "E21.0.3.21", {"start": v(168.28, -56.77) * mm, "end": v(152.4, -63.53) * mm});
            skLineSegment(sketch, "E21.0.3.22", {"start": v(282.58, -56.77) * mm, "end": v(266.7, -63.53) * mm});
            skLineSegment(sketch, "E21.0.3.23", {"start": v(190.5, -50) * mm, "end": v(206.38, -56.77) * mm});
            skLineSegment(sketch, "E21.0.3.24", {"start": v(228.6, -50) * mm, "end": v(244.48, -56.77) * mm});
            skLineSegment(sketch, "E21.0.3.25", {"start": v(266.7, -50) * mm, "end": v(282.58, -56.77) * mm});
            skLineSegment(sketch, "E21.0.3.26", {"start": v(304.8, -50) * mm, "end": v(320.68, -56.77) * mm});
            skLineSegment(sketch, "E21.0.3.27", {"start": v(38.1, -50) * mm, "end": v(53.98, -56.77) * mm});
            skLineSegment(sketch, "E21.0.3.28", {"start": v(76.2, -50) * mm, "end": v(92.08, -56.77) * mm});
            skLineSegment(sketch, "E21.0.3.29", {"start": v(114.3, -50) * mm, "end": v(130.18, -56.77) * mm});
            skLineSegment(sketch, "E21.0.3.30", {"start": v(152.4, -50) * mm, "end": v(168.28, -56.77) * mm});
            skLineSegment(sketch, "E21.0.3.31", {"start": v(320.68, -56.77) * mm, "end": v(304.8, -63.53) * mm});
            skLineSegment(sketch, "E21.0.3.32", {"start": v(-15.88, -56.77) * mm, "end": v(0, -50) * mm});
            skLineSegment(sketch, "E21.0.3.33", {"start": v(0, -50) * mm, "end": v(15.88, -56.77) * mm});
            skLineSegment(sketch, "E21.0.3.34", {"start": v(15.88, -56.77) * mm, "end": v(0, -63.53) * mm});
            skLineSegment(sketch, "E21.0.3.35", {"start": v(0, -63.53) * mm, "end": v(-15.87, -56.77) * mm});
            skLineSegment(sketch, "E21.direction1", {"start": v(-15.88, 0) * mm, "end": v(9.52, 0) * mm, "construction": true});
            skLineSegment(sketch, "E21.direction2", {"start": v(-15.88, 0) * mm, "end": v(-15.88, -18.92) * mm, "construction": true});
            skLineSegment(sketch, "E22.1.0.0", {"start": v(-53.98, -18.92) * mm, "end": v(-38.1, -12.16) * mm});
            skLineSegment(sketch, "E22.1.0.1", {"start": v(-22.23, -18.92) * mm, "end": v(-38.1, -25.69) * mm});
            skLineSegment(sketch, "E22.1.0.2", {"start": v(-38.1, -25.69) * mm, "end": v(-53.98, -18.92) * mm});
            skLineSegment(sketch, "E22.1.0.3", {"start": v(-53.98, -37.85) * mm, "end": v(-38.1, -31.08) * mm});
            skLineSegment(sketch, "E22.1.0.4", {"start": v(-38.1, -31.08) * mm, "end": v(-22.23, -37.85) * mm});
            skLineSegment(sketch, "E22.1.0.5", {"start": v(-22.23, -37.85) * mm, "end": v(-38.1, -44.6) * mm});
            skLineSegment(sketch, "E22.1.0.6", {"start": v(-38.1, -44.6) * mm, "end": v(-53.98, -37.85) * mm});
            skLineSegment(sketch, "E22.1.0.7", {"start": v(-53.98, -56.77) * mm, "end": v(-38.1, -50) * mm});
            skLineSegment(sketch, "E22.1.0.8", {"start": v(-38.1, -63.53) * mm, "end": v(-53.98, -56.77) * mm});
            skLineSegment(sketch, "E22.1.0.9", {"start": v(-38.1, -50) * mm, "end": v(-22.23, -56.77) * mm});
            skLineSegment(sketch, "E22.1.0.10", {"start": v(-22.23, -56.77) * mm, "end": v(-38.1, -63.53) * mm});
            skLineSegment(sketch, "E22.1.0.11", {"start": v(-38.1, 63.53) * mm, "end": v(-22.23, 56.77) * mm});
            skLineSegment(sketch, "E22.1.0.12", {"start": v(-53.98, 56.77) * mm, "end": v(-38.1, 63.53) * mm});
            skLineSegment(sketch, "E22.1.0.13", {"start": v(-38.1, 50) * mm, "end": v(-53.98, 56.77) * mm});
            skLineSegment(sketch, "E22.1.0.14", {"start": v(-53.98, 0) * mm, "end": v(-38.1, 6.76) * mm});
            skLineSegment(sketch, "E22.1.0.15", {"start": v(-38.1, 6.76) * mm, "end": v(-22.23, 0) * mm});
            skLineSegment(sketch, "E22.1.0.16", {"start": v(-38.1, -6.76) * mm, "end": v(-53.98, 0) * mm});
            skLineSegment(sketch, "E22.1.0.17", {"start": v(-22.23, 18.92) * mm, "end": v(-38.1, 12.16) * mm});
            skLineSegment(sketch, "E22.1.0.18", {"start": v(-38.1, 25.69) * mm, "end": v(-22.23, 18.92) * mm});
            skLineSegment(sketch, "E22.1.0.19", {"start": v(-53.98, 18.92) * mm, "end": v(-38.1, 25.69) * mm});
            skLineSegment(sketch, "E22.1.0.20", {"start": v(-38.1, 12.16) * mm, "end": v(-53.98, 18.92) * mm});
            skLineSegment(sketch, "E22.1.0.21", {"start": v(-22.23, 37.85) * mm, "end": v(-38.1, 31.08) * mm});
            skLineSegment(sketch, "E22.1.0.22", {"start": v(-38.1, 44.6) * mm, "end": v(-22.23, 37.85) * mm});
            skLineSegment(sketch, "E22.1.0.23", {"start": v(-53.98, 37.85) * mm, "end": v(-38.1, 44.6) * mm});
            skLineSegment(sketch, "E22.1.0.24", {"start": v(-38.1, 31.08) * mm, "end": v(-53.98, 37.85) * mm});
            skLineSegment(sketch, "E22.1.0.25", {"start": v(-22.23, 56.77) * mm, "end": v(-38.1, 50) * mm});
            skLineSegment(sketch, "E22.1.0.26", {"start": v(-38.1, -12.16) * mm, "end": v(-22.23, -18.92) * mm});
            skLineSegment(sketch, "E22.1.0.27", {"start": v(-22.23, 0) * mm, "end": v(-38.1, -6.76) * mm});
            skLineSegment(sketch, "E22.2.0.0", {"start": v(-92.08, -18.92) * mm, "end": v(-76.2, -12.16) * mm});
            skLineSegment(sketch, "E22.2.0.1", {"start": v(-60.33, -18.92) * mm, "end": v(-76.2, -25.69) * mm});
            skLineSegment(sketch, "E22.2.0.2", {"start": v(-76.2, -25.69) * mm, "end": v(-92.08, -18.92) * mm});
            skLineSegment(sketch, "E22.2.0.3", {"start": v(-92.08, -37.85) * mm, "end": v(-76.2, -31.08) * mm});
            skLineSegment(sketch, "E22.2.0.4", {"start": v(-76.2, -31.08) * mm, "end": v(-60.32, -37.85) * mm});
            skLineSegment(sketch, "E22.2.0.5", {"start": v(-60.33, -37.85) * mm, "end": v(-76.2, -44.6) * mm});
            skLineSegment(sketch, "E22.2.0.6", {"start": v(-76.2, -44.6) * mm, "end": v(-92.08, -37.85) * mm});
            skLineSegment(sketch, "E22.2.0.7", {"start": v(-92.08, -56.77) * mm, "end": v(-76.2, -50) * mm});
            skLineSegment(sketch, "E22.2.0.8", {"start": v(-76.2, -63.53) * mm, "end": v(-92.08, -56.77) * mm});
            skLineSegment(sketch, "E22.2.0.9", {"start": v(-76.2, -50) * mm, "end": v(-60.32, -56.77) * mm});
            skLineSegment(sketch, "E22.2.0.10", {"start": v(-60.33, -56.77) * mm, "end": v(-76.2, -63.53) * mm});
            skLineSegment(sketch, "E22.2.0.11", {"start": v(-76.2, 63.53) * mm, "end": v(-60.32, 56.77) * mm});
            skLineSegment(sketch, "E22.2.0.12", {"start": v(-92.08, 56.77) * mm, "end": v(-76.2, 63.53) * mm});
            skLineSegment(sketch, "E22.2.0.13", {"start": v(-76.2, 50) * mm, "end": v(-92.08, 56.77) * mm});
            skLineSegment(sketch, "E22.2.0.14", {"start": v(-92.08, 0) * mm, "end": v(-76.2, 6.76) * mm});
            skLineSegment(sketch, "E22.2.0.15", {"start": v(-76.2, 6.76) * mm, "end": v(-60.32, 0) * mm});
            skLineSegment(sketch, "E22.2.0.16", {"start": v(-76.2, -6.76) * mm, "end": v(-92.08, 0) * mm});
            skLineSegment(sketch, "E22.2.0.17", {"start": v(-60.33, 18.92) * mm, "end": v(-76.2, 12.16) * mm});
            skLineSegment(sketch, "E22.2.0.18", {"start": v(-76.2, 25.69) * mm, "end": v(-60.32, 18.92) * mm});
            skLineSegment(sketch, "E22.2.0.19", {"start": v(-92.08, 18.92) * mm, "end": v(-76.2, 25.69) * mm});
            skLineSegment(sketch, "E22.2.0.20", {"start": v(-76.2, 12.16) * mm, "end": v(-92.08, 18.92) * mm});
            skLineSegment(sketch, "E22.2.0.21", {"start": v(-60.33, 37.85) * mm, "end": v(-76.2, 31.08) * mm});
            skLineSegment(sketch, "E22.2.0.22", {"start": v(-76.2, 44.6) * mm, "end": v(-60.32, 37.85) * mm});
            skLineSegment(sketch, "E22.2.0.23", {"start": v(-92.08, 37.85) * mm, "end": v(-76.2, 44.6) * mm});
            skLineSegment(sketch, "E22.2.0.24", {"start": v(-76.2, 31.08) * mm, "end": v(-92.08, 37.85) * mm});
            skLineSegment(sketch, "E22.2.0.25", {"start": v(-60.33, 56.77) * mm, "end": v(-76.2, 50) * mm});
            skLineSegment(sketch, "E22.2.0.26", {"start": v(-76.2, -12.16) * mm, "end": v(-60.32, -18.92) * mm});
            skLineSegment(sketch, "E22.2.0.27", {"start": v(-60.33, 0) * mm, "end": v(-76.2, -6.76) * mm});
            skLineSegment(sketch, "E22.3.0.0", {"start": v(-130.18, -18.92) * mm, "end": v(-114.3, -12.16) * mm});
            skLineSegment(sketch, "E22.3.0.1", {"start": v(-98.43, -18.92) * mm, "end": v(-114.3, -25.69) * mm});
            skLineSegment(sketch, "E22.3.0.2", {"start": v(-114.3, -25.69) * mm, "end": v(-130.18, -18.92) * mm});
            skLineSegment(sketch, "E22.3.0.3", {"start": v(-130.18, -37.85) * mm, "end": v(-114.3, -31.08) * mm});
            skLineSegment(sketch, "E22.3.0.4", {"start": v(-114.3, -31.08) * mm, "end": v(-98.43, -37.85) * mm});
            skLineSegment(sketch, "E22.3.0.5", {"start": v(-98.43, -37.85) * mm, "end": v(-114.3, -44.6) * mm});
            skLineSegment(sketch, "E22.3.0.6", {"start": v(-114.3, -44.6) * mm, "end": v(-130.18, -37.85) * mm});
            skLineSegment(sketch, "E22.3.0.7", {"start": v(-130.18, -56.77) * mm, "end": v(-114.3, -50) * mm});
            skLineSegment(sketch, "E22.3.0.8", {"start": v(-114.3, -63.53) * mm, "end": v(-130.18, -56.77) * mm});
            skLineSegment(sketch, "E22.3.0.9", {"start": v(-114.3, -50) * mm, "end": v(-98.43, -56.77) * mm});
            skLineSegment(sketch, "E22.3.0.10", {"start": v(-98.43, -56.77) * mm, "end": v(-114.3, -63.53) * mm});
            skLineSegment(sketch, "E22.3.0.11", {"start": v(-114.3, 63.53) * mm, "end": v(-98.43, 56.77) * mm});
            skLineSegment(sketch, "E22.3.0.12", {"start": v(-130.18, 56.77) * mm, "end": v(-114.3, 63.53) * mm});
            skLineSegment(sketch, "E22.3.0.13", {"start": v(-114.3, 50) * mm, "end": v(-130.18, 56.77) * mm});
            skLineSegment(sketch, "E22.3.0.14", {"start": v(-130.18, 0) * mm, "end": v(-114.3, 6.76) * mm});
            skLineSegment(sketch, "E22.3.0.15", {"start": v(-114.3, 6.76) * mm, "end": v(-98.43, 0) * mm});
            skLineSegment(sketch, "E22.3.0.16", {"start": v(-114.3, -6.76) * mm, "end": v(-130.18, 0) * mm});
            skLineSegment(sketch, "E22.3.0.17", {"start": v(-98.43, 18.92) * mm, "end": v(-114.3, 12.16) * mm});
            skLineSegment(sketch, "E22.3.0.18", {"start": v(-114.3, 25.69) * mm, "end": v(-98.43, 18.92) * mm});
            skLineSegment(sketch, "E22.3.0.19", {"start": v(-130.18, 18.92) * mm, "end": v(-114.3, 25.69) * mm});
            skLineSegment(sketch, "E22.3.0.20", {"start": v(-114.3, 12.16) * mm, "end": v(-130.18, 18.92) * mm});
            skLineSegment(sketch, "E22.3.0.21", {"start": v(-98.43, 37.85) * mm, "end": v(-114.3, 31.08) * mm});
            skLineSegment(sketch, "E22.3.0.22", {"start": v(-114.3, 44.6) * mm, "end": v(-98.43, 37.85) * mm});
            skLineSegment(sketch, "E22.3.0.23", {"start": v(-130.18, 37.85) * mm, "end": v(-114.3, 44.6) * mm});
            skLineSegment(sketch, "E22.3.0.24", {"start": v(-114.3, 31.08) * mm, "end": v(-130.18, 37.85) * mm});
            skLineSegment(sketch, "E22.3.0.25", {"start": v(-98.43, 56.77) * mm, "end": v(-114.3, 50) * mm});
            skLineSegment(sketch, "E22.3.0.26", {"start": v(-114.3, -12.16) * mm, "end": v(-98.43, -18.92) * mm});
            skLineSegment(sketch, "E22.3.0.27", {"start": v(-98.43, 0) * mm, "end": v(-114.3, -6.76) * mm});
            skLineSegment(sketch, "E22.4.0.0", {"start": v(-168.28, -18.92) * mm, "end": v(-152.4, -12.16) * mm});
            skLineSegment(sketch, "E22.4.0.1", {"start": v(-136.53, -18.92) * mm, "end": v(-152.4, -25.69) * mm});
            skLineSegment(sketch, "E22.4.0.2", {"start": v(-152.4, -25.69) * mm, "end": v(-168.28, -18.92) * mm});
            skLineSegment(sketch, "E22.4.0.3", {"start": v(-168.28, -37.85) * mm, "end": v(-152.4, -31.08) * mm});
            skLineSegment(sketch, "E22.4.0.4", {"start": v(-152.4, -31.08) * mm, "end": v(-136.53, -37.85) * mm});
            skLineSegment(sketch, "E22.4.0.5", {"start": v(-136.53, -37.85) * mm, "end": v(-152.4, -44.6) * mm});
            skLineSegment(sketch, "E22.4.0.6", {"start": v(-152.4, -44.6) * mm, "end": v(-168.28, -37.85) * mm});
            skLineSegment(sketch, "E22.4.0.7", {"start": v(-168.28, -56.77) * mm, "end": v(-152.4, -50) * mm});
            skLineSegment(sketch, "E22.4.0.8", {"start": v(-152.4, -63.53) * mm, "end": v(-168.28, -56.77) * mm});
            skLineSegment(sketch, "E22.4.0.9", {"start": v(-152.4, -50) * mm, "end": v(-136.53, -56.77) * mm});
            skLineSegment(sketch, "E22.4.0.10", {"start": v(-136.53, -56.77) * mm, "end": v(-152.4, -63.53) * mm});
            skLineSegment(sketch, "E22.4.0.11", {"start": v(-152.4, 63.53) * mm, "end": v(-136.53, 56.77) * mm});
            skLineSegment(sketch, "E22.4.0.12", {"start": v(-168.28, 56.77) * mm, "end": v(-152.4, 63.53) * mm});
            skLineSegment(sketch, "E22.4.0.13", {"start": v(-152.4, 50) * mm, "end": v(-168.28, 56.77) * mm});
            skLineSegment(sketch, "E22.4.0.14", {"start": v(-168.28, 0) * mm, "end": v(-152.4, 6.76) * mm});
            skLineSegment(sketch, "E22.4.0.15", {"start": v(-152.4, 6.76) * mm, "end": v(-136.53, 0) * mm});
            skLineSegment(sketch, "E22.4.0.16", {"start": v(-152.4, -6.76) * mm, "end": v(-168.28, 0) * mm});
            skLineSegment(sketch, "E22.4.0.17", {"start": v(-136.53, 18.92) * mm, "end": v(-152.4, 12.16) * mm});
            skLineSegment(sketch, "E22.4.0.18", {"start": v(-152.4, 25.69) * mm, "end": v(-136.53, 18.92) * mm});
            skLineSegment(sketch, "E22.4.0.19", {"start": v(-168.28, 18.92) * mm, "end": v(-152.4, 25.69) * mm});
            skLineSegment(sketch, "E22.4.0.20", {"start": v(-152.4, 12.16) * mm, "end": v(-168.28, 18.92) * mm});
            skLineSegment(sketch, "E22.4.0.21", {"start": v(-136.53, 37.85) * mm, "end": v(-152.4, 31.08) * mm});
            skLineSegment(sketch, "E22.4.0.22", {"start": v(-152.4, 44.6) * mm, "end": v(-136.53, 37.85) * mm});
            skLineSegment(sketch, "E22.4.0.23", {"start": v(-168.28, 37.85) * mm, "end": v(-152.4, 44.6) * mm});
            skLineSegment(sketch, "E22.4.0.24", {"start": v(-152.4, 31.08) * mm, "end": v(-168.28, 37.85) * mm});
            skLineSegment(sketch, "E22.4.0.25", {"start": v(-136.53, 56.77) * mm, "end": v(-152.4, 50) * mm});
            skLineSegment(sketch, "E22.4.0.26", {"start": v(-152.4, -12.16) * mm, "end": v(-136.53, -18.92) * mm});
            skLineSegment(sketch, "E22.4.0.27", {"start": v(-136.53, 0) * mm, "end": v(-152.4, -6.76) * mm});
            skLineSegment(sketch, "E22.5.0.0", {"start": v(-206.38, -18.92) * mm, "end": v(-190.5, -12.16) * mm});
            skLineSegment(sketch, "E22.5.0.1", {"start": v(-174.62, -18.92) * mm, "end": v(-190.5, -25.69) * mm});
            skLineSegment(sketch, "E22.5.0.2", {"start": v(-190.5, -25.69) * mm, "end": v(-206.38, -18.92) * mm});
            skLineSegment(sketch, "E22.5.0.3", {"start": v(-206.38, -37.85) * mm, "end": v(-190.5, -31.08) * mm});
            skLineSegment(sketch, "E22.5.0.4", {"start": v(-190.5, -31.08) * mm, "end": v(-174.62, -37.85) * mm});
            skLineSegment(sketch, "E22.5.0.5", {"start": v(-174.62, -37.85) * mm, "end": v(-190.5, -44.6) * mm});
            skLineSegment(sketch, "E22.5.0.6", {"start": v(-190.5, -44.6) * mm, "end": v(-206.38, -37.85) * mm});
            skLineSegment(sketch, "E22.5.0.7", {"start": v(-206.38, -56.77) * mm, "end": v(-190.5, -50) * mm});
            skLineSegment(sketch, "E22.5.0.8", {"start": v(-190.5, -63.53) * mm, "end": v(-206.38, -56.77) * mm});
            skLineSegment(sketch, "E22.5.0.9", {"start": v(-190.5, -50) * mm, "end": v(-174.62, -56.77) * mm});
            skLineSegment(sketch, "E22.5.0.10", {"start": v(-174.62, -56.77) * mm, "end": v(-190.5, -63.53) * mm});
            skLineSegment(sketch, "E22.5.0.11", {"start": v(-190.5, 63.53) * mm, "end": v(-174.62, 56.77) * mm});
            skLineSegment(sketch, "E22.5.0.12", {"start": v(-206.38, 56.77) * mm, "end": v(-190.5, 63.53) * mm});
            skLineSegment(sketch, "E22.5.0.13", {"start": v(-190.5, 50) * mm, "end": v(-206.38, 56.77) * mm});
            skLineSegment(sketch, "E22.5.0.14", {"start": v(-206.38, 0) * mm, "end": v(-190.5, 6.76) * mm});
            skLineSegment(sketch, "E22.5.0.15", {"start": v(-190.5, 6.76) * mm, "end": v(-174.62, 0) * mm});
            skLineSegment(sketch, "E22.5.0.16", {"start": v(-190.5, -6.76) * mm, "end": v(-206.38, 0) * mm});
            skLineSegment(sketch, "E22.5.0.17", {"start": v(-174.62, 18.92) * mm, "end": v(-190.5, 12.16) * mm});
            skLineSegment(sketch, "E22.5.0.18", {"start": v(-190.5, 25.69) * mm, "end": v(-174.62, 18.92) * mm});
            skLineSegment(sketch, "E22.5.0.19", {"start": v(-206.38, 18.92) * mm, "end": v(-190.5, 25.69) * mm});
            skLineSegment(sketch, "E22.5.0.20", {"start": v(-190.5, 12.16) * mm, "end": v(-206.38, 18.92) * mm});
            skLineSegment(sketch, "E22.5.0.21", {"start": v(-174.62, 37.85) * mm, "end": v(-190.5, 31.08) * mm});
            skLineSegment(sketch, "E22.5.0.22", {"start": v(-190.5, 44.6) * mm, "end": v(-174.62, 37.85) * mm});
            skLineSegment(sketch, "E22.5.0.23", {"start": v(-206.38, 37.85) * mm, "end": v(-190.5, 44.6) * mm});
            skLineSegment(sketch, "E22.5.0.24", {"start": v(-190.5, 31.08) * mm, "end": v(-206.38, 37.85) * mm});
            skLineSegment(sketch, "E22.5.0.25", {"start": v(-174.62, 56.77) * mm, "end": v(-190.5, 50) * mm});
            skLineSegment(sketch, "E22.5.0.26", {"start": v(-190.5, -12.16) * mm, "end": v(-174.62, -18.92) * mm});
            skLineSegment(sketch, "E22.5.0.27", {"start": v(-174.62, 0) * mm, "end": v(-190.5, -6.76) * mm});
            skLineSegment(sketch, "E22.6.0.0", {"start": v(-244.48, -18.92) * mm, "end": v(-228.6, -12.16) * mm});
            skLineSegment(sketch, "E22.6.0.1", {"start": v(-212.73, -18.92) * mm, "end": v(-228.6, -25.69) * mm});
            skLineSegment(sketch, "E22.6.0.2", {"start": v(-228.6, -25.69) * mm, "end": v(-244.48, -18.92) * mm});
            skLineSegment(sketch, "E22.6.0.3", {"start": v(-244.48, -37.85) * mm, "end": v(-228.6, -31.08) * mm});
            skLineSegment(sketch, "E22.6.0.4", {"start": v(-228.6, -31.08) * mm, "end": v(-212.73, -37.85) * mm});
            skLineSegment(sketch, "E22.6.0.5", {"start": v(-212.73, -37.85) * mm, "end": v(-228.6, -44.6) * mm});
            skLineSegment(sketch, "E22.6.0.6", {"start": v(-228.6, -44.6) * mm, "end": v(-244.48, -37.85) * mm});
            skLineSegment(sketch, "E22.6.0.7", {"start": v(-244.48, -56.77) * mm, "end": v(-228.6, -50) * mm});
            skLineSegment(sketch, "E22.6.0.8", {"start": v(-228.6, -63.53) * mm, "end": v(-244.48, -56.77) * mm});
            skLineSegment(sketch, "E22.6.0.9", {"start": v(-228.6, -50) * mm, "end": v(-212.73, -56.77) * mm});
            skLineSegment(sketch, "E22.6.0.10", {"start": v(-212.73, -56.77) * mm, "end": v(-228.6, -63.53) * mm});
            skLineSegment(sketch, "E22.6.0.11", {"start": v(-228.6, 63.53) * mm, "end": v(-212.73, 56.77) * mm});
            skLineSegment(sketch, "E22.6.0.12", {"start": v(-244.48, 56.77) * mm, "end": v(-228.6, 63.53) * mm});
            skLineSegment(sketch, "E22.6.0.13", {"start": v(-228.6, 50) * mm, "end": v(-244.48, 56.77) * mm});
            skLineSegment(sketch, "E22.6.0.14", {"start": v(-244.48, 0) * mm, "end": v(-228.6, 6.76) * mm});
            skLineSegment(sketch, "E22.6.0.15", {"start": v(-228.6, 6.76) * mm, "end": v(-212.73, 0) * mm});
            skLineSegment(sketch, "E22.6.0.16", {"start": v(-228.6, -6.76) * mm, "end": v(-244.48, 0) * mm});
            skLineSegment(sketch, "E22.6.0.17", {"start": v(-212.73, 18.92) * mm, "end": v(-228.6, 12.16) * mm});
            skLineSegment(sketch, "E22.6.0.18", {"start": v(-228.6, 25.69) * mm, "end": v(-212.73, 18.92) * mm});
            skLineSegment(sketch, "E22.6.0.19", {"start": v(-244.48, 18.92) * mm, "end": v(-228.6, 25.69) * mm});
            skLineSegment(sketch, "E22.6.0.20", {"start": v(-228.6, 12.16) * mm, "end": v(-244.48, 18.92) * mm});
            skLineSegment(sketch, "E22.6.0.21", {"start": v(-212.73, 37.85) * mm, "end": v(-228.6, 31.08) * mm});
            skLineSegment(sketch, "E22.6.0.22", {"start": v(-228.6, 44.6) * mm, "end": v(-212.73, 37.85) * mm});
            skLineSegment(sketch, "E22.6.0.23", {"start": v(-244.48, 37.85) * mm, "end": v(-228.6, 44.6) * mm});
            skLineSegment(sketch, "E22.6.0.24", {"start": v(-228.6, 31.08) * mm, "end": v(-244.48, 37.85) * mm});
            skLineSegment(sketch, "E22.6.0.25", {"start": v(-212.73, 56.77) * mm, "end": v(-228.6, 50) * mm});
            skLineSegment(sketch, "E22.6.0.26", {"start": v(-228.6, -12.16) * mm, "end": v(-212.73, -18.92) * mm});
            skLineSegment(sketch, "E22.6.0.27", {"start": v(-212.73, 0) * mm, "end": v(-228.6, -6.76) * mm});
            skLineSegment(sketch, "E22.7.0.0", {"start": v(-282.58, -18.92) * mm, "end": v(-266.7, -12.16) * mm});
            skLineSegment(sketch, "E22.7.0.1", {"start": v(-250.83, -18.92) * mm, "end": v(-266.7, -25.69) * mm});
            skLineSegment(sketch, "E22.7.0.2", {"start": v(-266.7, -25.69) * mm, "end": v(-282.57, -18.92) * mm});
            skLineSegment(sketch, "E22.7.0.3", {"start": v(-282.58, -37.85) * mm, "end": v(-266.7, -31.08) * mm});
            skLineSegment(sketch, "E22.7.0.4", {"start": v(-266.7, -31.08) * mm, "end": v(-250.82, -37.85) * mm});
            skLineSegment(sketch, "E22.7.0.5", {"start": v(-250.83, -37.85) * mm, "end": v(-266.7, -44.6) * mm});
            skLineSegment(sketch, "E22.7.0.6", {"start": v(-266.7, -44.6) * mm, "end": v(-282.57, -37.85) * mm});
            skLineSegment(sketch, "E22.7.0.7", {"start": v(-282.58, -56.77) * mm, "end": v(-266.7, -50) * mm});
            skLineSegment(sketch, "E22.7.0.8", {"start": v(-266.7, -63.53) * mm, "end": v(-282.57, -56.77) * mm});
            skLineSegment(sketch, "E22.7.0.9", {"start": v(-266.7, -50) * mm, "end": v(-250.82, -56.77) * mm});
            skLineSegment(sketch, "E22.7.0.10", {"start": v(-250.83, -56.77) * mm, "end": v(-266.7, -63.53) * mm});
            skLineSegment(sketch, "E22.7.0.11", {"start": v(-266.7, 63.53) * mm, "end": v(-250.82, 56.77) * mm});
            skLineSegment(sketch, "E22.7.0.12", {"start": v(-282.58, 56.77) * mm, "end": v(-266.7, 63.53) * mm});
            skLineSegment(sketch, "E22.7.0.13", {"start": v(-266.7, 50) * mm, "end": v(-282.57, 56.77) * mm});
            skLineSegment(sketch, "E22.7.0.14", {"start": v(-282.58, 0) * mm, "end": v(-266.7, 6.76) * mm});
            skLineSegment(sketch, "E22.7.0.15", {"start": v(-266.7, 6.76) * mm, "end": v(-250.82, 0) * mm});
            skLineSegment(sketch, "E22.7.0.16", {"start": v(-266.7, -6.76) * mm, "end": v(-282.57, 0) * mm});
            skLineSegment(sketch, "E22.7.0.17", {"start": v(-250.83, 18.92) * mm, "end": v(-266.7, 12.16) * mm});
            skLineSegment(sketch, "E22.7.0.18", {"start": v(-266.7, 25.69) * mm, "end": v(-250.82, 18.92) * mm});
            skLineSegment(sketch, "E22.7.0.19", {"start": v(-282.58, 18.92) * mm, "end": v(-266.7, 25.69) * mm});
            skLineSegment(sketch, "E22.7.0.20", {"start": v(-266.7, 12.16) * mm, "end": v(-282.57, 18.92) * mm});
            skLineSegment(sketch, "E22.7.0.21", {"start": v(-250.83, 37.85) * mm, "end": v(-266.7, 31.08) * mm});
            skLineSegment(sketch, "E22.7.0.22", {"start": v(-266.7, 44.6) * mm, "end": v(-250.82, 37.85) * mm});
            skLineSegment(sketch, "E22.7.0.23", {"start": v(-282.58, 37.85) * mm, "end": v(-266.7, 44.6) * mm});
            skLineSegment(sketch, "E22.7.0.24", {"start": v(-266.7, 31.08) * mm, "end": v(-282.57, 37.85) * mm});
            skLineSegment(sketch, "E22.7.0.25", {"start": v(-250.83, 56.77) * mm, "end": v(-266.7, 50) * mm});
            skLineSegment(sketch, "E22.7.0.26", {"start": v(-266.7, -12.16) * mm, "end": v(-250.82, -18.92) * mm});
            skLineSegment(sketch, "E22.7.0.27", {"start": v(-250.82, 0) * mm, "end": v(-266.7, -6.76) * mm});
            skLineSegment(sketch, "E22.8.0.0", {"start": v(-320.68, -18.92) * mm, "end": v(-304.8, -12.16) * mm});
            skLineSegment(sketch, "E22.8.0.1", {"start": v(-288.93, -18.92) * mm, "end": v(-304.8, -25.69) * mm});
            skLineSegment(sketch, "E22.8.0.2", {"start": v(-304.8, -25.69) * mm, "end": v(-320.68, -18.92) * mm});
            skLineSegment(sketch, "E22.8.0.3", {"start": v(-320.68, -37.85) * mm, "end": v(-304.8, -31.08) * mm});
            skLineSegment(sketch, "E22.8.0.4", {"start": v(-304.8, -31.08) * mm, "end": v(-288.93, -37.85) * mm});
            skLineSegment(sketch, "E22.8.0.5", {"start": v(-288.93, -37.85) * mm, "end": v(-304.8, -44.6) * mm});
            skLineSegment(sketch, "E22.8.0.6", {"start": v(-304.8, -44.6) * mm, "end": v(-320.68, -37.85) * mm});
            skLineSegment(sketch, "E22.8.0.7", {"start": v(-320.68, -56.77) * mm, "end": v(-304.8, -50) * mm});
            skLineSegment(sketch, "E22.8.0.8", {"start": v(-304.8, -63.53) * mm, "end": v(-320.68, -56.77) * mm});
            skLineSegment(sketch, "E22.8.0.9", {"start": v(-304.8, -50) * mm, "end": v(-288.93, -56.77) * mm});
            skLineSegment(sketch, "E22.8.0.10", {"start": v(-288.93, -56.77) * mm, "end": v(-304.8, -63.53) * mm});
            skLineSegment(sketch, "E22.8.0.11", {"start": v(-304.8, 63.53) * mm, "end": v(-288.93, 56.77) * mm});
            skLineSegment(sketch, "E22.8.0.12", {"start": v(-320.68, 56.77) * mm, "end": v(-304.8, 63.53) * mm});
            skLineSegment(sketch, "E22.8.0.13", {"start": v(-304.8, 50) * mm, "end": v(-320.68, 56.77) * mm});
            skLineSegment(sketch, "E22.8.0.14", {"start": v(-320.68, 0) * mm, "end": v(-304.8, 6.76) * mm});
            skLineSegment(sketch, "E22.8.0.15", {"start": v(-304.8, 6.76) * mm, "end": v(-288.93, 0) * mm});
            skLineSegment(sketch, "E22.8.0.16", {"start": v(-304.8, -6.76) * mm, "end": v(-320.68, 0) * mm});
            skLineSegment(sketch, "E22.8.0.17", {"start": v(-288.93, 18.92) * mm, "end": v(-304.8, 12.16) * mm});
            skLineSegment(sketch, "E22.8.0.18", {"start": v(-304.8, 25.69) * mm, "end": v(-288.93, 18.92) * mm});
            skLineSegment(sketch, "E22.8.0.19", {"start": v(-320.68, 18.92) * mm, "end": v(-304.8, 25.69) * mm});
            skLineSegment(sketch, "E22.8.0.20", {"start": v(-304.8, 12.16) * mm, "end": v(-320.68, 18.92) * mm});
            skLineSegment(sketch, "E22.8.0.21", {"start": v(-288.93, 37.85) * mm, "end": v(-304.8, 31.08) * mm});
            skLineSegment(sketch, "E22.8.0.22", {"start": v(-304.8, 44.6) * mm, "end": v(-288.93, 37.85) * mm});
            skLineSegment(sketch, "E22.8.0.23", {"start": v(-320.68, 37.85) * mm, "end": v(-304.8, 44.6) * mm});
            skLineSegment(sketch, "E22.8.0.24", {"start": v(-304.8, 31.08) * mm, "end": v(-320.68, 37.85) * mm});
            skLineSegment(sketch, "E22.8.0.25", {"start": v(-288.93, 56.77) * mm, "end": v(-304.8, 50) * mm});
            skLineSegment(sketch, "E22.8.0.26", {"start": v(-304.8, -12.16) * mm, "end": v(-288.93, -18.92) * mm});
            skLineSegment(sketch, "E22.8.0.27", {"start": v(-288.93, 0) * mm, "end": v(-304.8, -6.76) * mm});
            skLineSegment(sketch, "E22.direction1", {"start": v(-15.88, -56.77) * mm, "end": v(-53.98, -56.77) * mm, "construction": true});
            skLineSegment(sketch, "E23", {"start": v(285.75, -40.54) * mm, "end": v(269.87, -47.3) * mm});
            skLineSegment(sketch, "E24", {"start": v(269.87, -47.3) * mm, "end": v(285.75, -54.07) * mm});
            skLineSegment(sketch, "E25", {"start": v(285.75, -54.07) * mm, "end": v(301.62, -47.3) * mm});
            skLineSegment(sketch, "E26", {"start": v(301.62, -47.3) * mm, "end": v(285.75, -40.54) * mm});
            skLineSegment(sketch, "E27.0.1.0", {"start": v(285.75, -21.62) * mm, "end": v(269.87, -28.38) * mm});
            skLineSegment(sketch, "E27.0.1.1", {"start": v(301.62, -28.38) * mm, "end": v(285.75, -21.62) * mm});
            skLineSegment(sketch, "E27.0.1.2", {"start": v(285.75, -35.15) * mm, "end": v(301.62, -28.38) * mm});
            skLineSegment(sketch, "E27.0.1.3", {"start": v(269.87, -28.38) * mm, "end": v(285.75, -35.15) * mm});
            skLineSegment(sketch, "E27.0.2.0", {"start": v(285.75, -2.7) * mm, "end": v(269.87, -9.46) * mm});
            skLineSegment(sketch, "E27.0.2.1", {"start": v(301.62, -9.46) * mm, "end": v(285.75, -2.7) * mm});
            skLineSegment(sketch, "E27.0.2.2", {"start": v(285.75, -16.22) * mm, "end": v(301.62, -9.46) * mm});
            skLineSegment(sketch, "E27.0.2.3", {"start": v(269.87, -9.46) * mm, "end": v(285.75, -16.22) * mm});
            skLineSegment(sketch, "E27.0.3.0", {"start": v(285.75, 16.22) * mm, "end": v(269.87, 9.46) * mm});
            skLineSegment(sketch, "E27.0.3.1", {"start": v(301.62, 9.46) * mm, "end": v(285.75, 16.22) * mm});
            skLineSegment(sketch, "E27.0.3.2", {"start": v(285.75, 2.7) * mm, "end": v(301.62, 9.46) * mm});
            skLineSegment(sketch, "E27.0.3.3", {"start": v(269.87, 9.46) * mm, "end": v(285.75, 2.7) * mm});
            skLineSegment(sketch, "E27.0.4.0", {"start": v(285.75, 35.15) * mm, "end": v(269.87, 28.38) * mm});
            skLineSegment(sketch, "E27.0.4.1", {"start": v(301.62, 28.38) * mm, "end": v(285.75, 35.15) * mm});
            skLineSegment(sketch, "E27.0.4.2", {"start": v(285.75, 21.62) * mm, "end": v(301.62, 28.38) * mm});
            skLineSegment(sketch, "E27.0.4.3", {"start": v(269.87, 28.38) * mm, "end": v(285.75, 21.62) * mm});
            skLineSegment(sketch, "E27.0.5.0", {"start": v(285.75, 54.07) * mm, "end": v(269.87, 47.3) * mm});
            skLineSegment(sketch, "E27.0.5.1", {"start": v(301.62, 47.3) * mm, "end": v(285.75, 54.07) * mm});
            skLineSegment(sketch, "E27.0.5.2", {"start": v(285.75, 40.54) * mm, "end": v(301.62, 47.3) * mm});
            skLineSegment(sketch, "E27.0.5.3", {"start": v(269.87, 47.3) * mm, "end": v(285.75, 40.54) * mm});
            skLineSegment(sketch, "E27.1.0.0", {"start": v(247.65, -40.54) * mm, "end": v(231.77, -47.3) * mm});
            skLineSegment(sketch, "E27.1.0.1", {"start": v(263.52, -47.3) * mm, "end": v(247.65, -40.54) * mm});
            skLineSegment(sketch, "E27.1.0.2", {"start": v(247.65, -54.07) * mm, "end": v(263.52, -47.3) * mm});
            skLineSegment(sketch, "E27.1.0.3", {"start": v(231.77, -47.3) * mm, "end": v(247.65, -54.07) * mm});
            skLineSegment(sketch, "E27.1.1.0", {"start": v(247.65, -21.62) * mm, "end": v(231.77, -28.38) * mm});
            skLineSegment(sketch, "E27.1.1.1", {"start": v(263.52, -28.38) * mm, "end": v(247.65, -21.62) * mm});
            skLineSegment(sketch, "E27.1.1.2", {"start": v(247.65, -35.15) * mm, "end": v(263.52, -28.38) * mm});
            skLineSegment(sketch, "E27.1.1.3", {"start": v(231.77, -28.38) * mm, "end": v(247.65, -35.15) * mm});
            skLineSegment(sketch, "E27.1.2.0", {"start": v(247.65, -2.7) * mm, "end": v(231.77, -9.46) * mm});
            skLineSegment(sketch, "E27.1.2.1", {"start": v(263.52, -9.46) * mm, "end": v(247.65, -2.7) * mm});
            skLineSegment(sketch, "E27.1.2.2", {"start": v(247.65, -16.22) * mm, "end": v(263.52, -9.46) * mm});
            skLineSegment(sketch, "E27.1.2.3", {"start": v(231.77, -9.46) * mm, "end": v(247.65, -16.22) * mm});
            skLineSegment(sketch, "E27.1.3.0", {"start": v(247.65, 16.22) * mm, "end": v(231.77, 9.46) * mm});
            skLineSegment(sketch, "E27.1.3.1", {"start": v(263.52, 9.46) * mm, "end": v(247.65, 16.22) * mm});
            skLineSegment(sketch, "E27.1.3.2", {"start": v(247.65, 2.7) * mm, "end": v(263.52, 9.46) * mm});
            skLineSegment(sketch, "E27.1.3.3", {"start": v(231.77, 9.46) * mm, "end": v(247.65, 2.7) * mm});
            skLineSegment(sketch, "E27.1.4.0", {"start": v(247.65, 35.15) * mm, "end": v(231.77, 28.38) * mm});
            skLineSegment(sketch, "E27.1.4.1", {"start": v(263.52, 28.38) * mm, "end": v(247.65, 35.15) * mm});
            skLineSegment(sketch, "E27.1.4.2", {"start": v(247.65, 21.62) * mm, "end": v(263.52, 28.38) * mm});
            skLineSegment(sketch, "E27.1.4.3", {"start": v(231.77, 28.38) * mm, "end": v(247.65, 21.62) * mm});
            skLineSegment(sketch, "E27.1.5.0", {"start": v(247.65, 54.07) * mm, "end": v(231.77, 47.3) * mm});
            skLineSegment(sketch, "E27.1.5.1", {"start": v(263.52, 47.3) * mm, "end": v(247.65, 54.07) * mm});
            skLineSegment(sketch, "E27.1.5.2", {"start": v(247.65, 40.54) * mm, "end": v(263.52, 47.3) * mm});
            skLineSegment(sketch, "E27.1.5.3", {"start": v(231.77, 47.3) * mm, "end": v(247.65, 40.54) * mm});
            skLineSegment(sketch, "E27.2.0.0", {"start": v(209.55, -40.54) * mm, "end": v(193.67, -47.3) * mm});
            skLineSegment(sketch, "E27.2.0.1", {"start": v(225.42, -47.3) * mm, "end": v(209.55, -40.54) * mm});
            skLineSegment(sketch, "E27.2.0.2", {"start": v(209.55, -54.07) * mm, "end": v(225.42, -47.3) * mm});
            skLineSegment(sketch, "E27.2.0.3", {"start": v(193.67, -47.3) * mm, "end": v(209.55, -54.07) * mm});
            skLineSegment(sketch, "E27.2.1.0", {"start": v(209.55, -21.62) * mm, "end": v(193.67, -28.38) * mm});
            skLineSegment(sketch, "E27.2.1.1", {"start": v(225.42, -28.38) * mm, "end": v(209.55, -21.62) * mm});
            skLineSegment(sketch, "E27.2.1.2", {"start": v(209.55, -35.15) * mm, "end": v(225.42, -28.38) * mm});
            skLineSegment(sketch, "E27.2.1.3", {"start": v(193.67, -28.38) * mm, "end": v(209.55, -35.15) * mm});
            skLineSegment(sketch, "E27.2.2.0", {"start": v(209.55, -2.7) * mm, "end": v(193.67, -9.46) * mm});
            skLineSegment(sketch, "E27.2.2.1", {"start": v(225.42, -9.46) * mm, "end": v(209.55, -2.7) * mm});
            skLineSegment(sketch, "E27.2.2.2", {"start": v(209.55, -16.22) * mm, "end": v(225.42, -9.46) * mm});
            skLineSegment(sketch, "E27.2.2.3", {"start": v(193.67, -9.46) * mm, "end": v(209.55, -16.22) * mm});
            skLineSegment(sketch, "E27.2.3.0", {"start": v(209.55, 16.22) * mm, "end": v(193.67, 9.46) * mm});
            skLineSegment(sketch, "E27.2.3.1", {"start": v(225.42, 9.46) * mm, "end": v(209.55, 16.22) * mm});
            skLineSegment(sketch, "E27.2.3.2", {"start": v(209.55, 2.7) * mm, "end": v(225.42, 9.46) * mm});
            skLineSegment(sketch, "E27.2.3.3", {"start": v(193.67, 9.46) * mm, "end": v(209.55, 2.7) * mm});
            skLineSegment(sketch, "E27.2.4.0", {"start": v(209.55, 35.15) * mm, "end": v(193.67, 28.38) * mm});
            skLineSegment(sketch, "E27.2.4.1", {"start": v(225.42, 28.38) * mm, "end": v(209.55, 35.15) * mm});
            skLineSegment(sketch, "E27.2.4.2", {"start": v(209.55, 21.62) * mm, "end": v(225.42, 28.38) * mm});
            skLineSegment(sketch, "E27.2.4.3", {"start": v(193.67, 28.38) * mm, "end": v(209.55, 21.62) * mm});
            skLineSegment(sketch, "E27.2.5.0", {"start": v(209.55, 54.07) * mm, "end": v(193.67, 47.3) * mm});
            skLineSegment(sketch, "E27.2.5.1", {"start": v(225.42, 47.3) * mm, "end": v(209.55, 54.07) * mm});
            skLineSegment(sketch, "E27.2.5.2", {"start": v(209.55, 40.54) * mm, "end": v(225.42, 47.3) * mm});
            skLineSegment(sketch, "E27.2.5.3", {"start": v(193.67, 47.3) * mm, "end": v(209.55, 40.54) * mm});
            skLineSegment(sketch, "E27.3.0.0", {"start": v(171.45, -40.54) * mm, "end": v(155.57, -47.3) * mm});
            skLineSegment(sketch, "E27.3.0.1", {"start": v(187.32, -47.3) * mm, "end": v(171.45, -40.54) * mm});
            skLineSegment(sketch, "E27.3.0.2", {"start": v(171.45, -54.07) * mm, "end": v(187.32, -47.3) * mm});
            skLineSegment(sketch, "E27.3.0.3", {"start": v(155.57, -47.3) * mm, "end": v(171.45, -54.07) * mm});
            skLineSegment(sketch, "E27.3.1.0", {"start": v(171.45, -21.62) * mm, "end": v(155.57, -28.38) * mm});
            skLineSegment(sketch, "E27.3.1.1", {"start": v(187.32, -28.38) * mm, "end": v(171.45, -21.62) * mm});
            skLineSegment(sketch, "E27.3.1.2", {"start": v(171.45, -35.15) * mm, "end": v(187.32, -28.38) * mm});
            skLineSegment(sketch, "E27.3.1.3", {"start": v(155.57, -28.38) * mm, "end": v(171.45, -35.15) * mm});
            skLineSegment(sketch, "E27.3.2.0", {"start": v(171.45, -2.7) * mm, "end": v(155.57, -9.46) * mm});
            skLineSegment(sketch, "E27.3.2.1", {"start": v(187.32, -9.46) * mm, "end": v(171.45, -2.7) * mm});
            skLineSegment(sketch, "E27.3.2.2", {"start": v(171.45, -16.22) * mm, "end": v(187.32, -9.46) * mm});
            skLineSegment(sketch, "E27.3.2.3", {"start": v(155.57, -9.46) * mm, "end": v(171.45, -16.22) * mm});
            skLineSegment(sketch, "E27.3.3.0", {"start": v(171.45, 16.22) * mm, "end": v(155.57, 9.46) * mm});
            skLineSegment(sketch, "E27.3.3.1", {"start": v(187.32, 9.46) * mm, "end": v(171.45, 16.22) * mm});
            skLineSegment(sketch, "E27.3.3.2", {"start": v(171.45, 2.7) * mm, "end": v(187.32, 9.46) * mm});
            skLineSegment(sketch, "E27.3.3.3", {"start": v(155.57, 9.46) * mm, "end": v(171.45, 2.7) * mm});
            skLineSegment(sketch, "E27.3.4.0", {"start": v(171.45, 35.15) * mm, "end": v(155.57, 28.38) * mm});
            skLineSegment(sketch, "E27.3.4.1", {"start": v(187.32, 28.38) * mm, "end": v(171.45, 35.15) * mm});
            skLineSegment(sketch, "E27.3.4.2", {"start": v(171.45, 21.62) * mm, "end": v(187.32, 28.38) * mm});
            skLineSegment(sketch, "E27.3.4.3", {"start": v(155.57, 28.38) * mm, "end": v(171.45, 21.62) * mm});
            skLineSegment(sketch, "E27.3.5.0", {"start": v(171.45, 54.07) * mm, "end": v(155.57, 47.3) * mm});
            skLineSegment(sketch, "E27.3.5.1", {"start": v(187.32, 47.3) * mm, "end": v(171.45, 54.07) * mm});
            skLineSegment(sketch, "E27.3.5.2", {"start": v(171.45, 40.54) * mm, "end": v(187.32, 47.3) * mm});
            skLineSegment(sketch, "E27.3.5.3", {"start": v(155.57, 47.3) * mm, "end": v(171.45, 40.54) * mm});
            skLineSegment(sketch, "E27.4.0.0", {"start": v(133.35, -40.54) * mm, "end": v(117.47, -47.3) * mm});
            skLineSegment(sketch, "E27.4.0.1", {"start": v(149.22, -47.3) * mm, "end": v(133.35, -40.54) * mm});
            skLineSegment(sketch, "E27.4.0.2", {"start": v(133.35, -54.07) * mm, "end": v(149.22, -47.3) * mm});
            skLineSegment(sketch, "E27.4.0.3", {"start": v(117.47, -47.3) * mm, "end": v(133.35, -54.07) * mm});
            skLineSegment(sketch, "E27.4.1.0", {"start": v(133.35, -21.62) * mm, "end": v(117.47, -28.38) * mm});
            skLineSegment(sketch, "E27.4.1.1", {"start": v(149.22, -28.38) * mm, "end": v(133.35, -21.62) * mm});
            skLineSegment(sketch, "E27.4.1.2", {"start": v(133.35, -35.15) * mm, "end": v(149.22, -28.38) * mm});
            skLineSegment(sketch, "E27.4.1.3", {"start": v(117.47, -28.38) * mm, "end": v(133.35, -35.15) * mm});
            skLineSegment(sketch, "E27.4.2.0", {"start": v(133.35, -2.7) * mm, "end": v(117.47, -9.46) * mm});
            skLineSegment(sketch, "E27.4.2.1", {"start": v(149.22, -9.46) * mm, "end": v(133.35, -2.7) * mm});
            skLineSegment(sketch, "E27.4.2.2", {"start": v(133.35, -16.22) * mm, "end": v(149.22, -9.46) * mm});
            skLineSegment(sketch, "E27.4.2.3", {"start": v(117.47, -9.46) * mm, "end": v(133.35, -16.22) * mm});
            skLineSegment(sketch, "E27.4.3.0", {"start": v(133.35, 16.22) * mm, "end": v(117.47, 9.46) * mm});
            skLineSegment(sketch, "E27.4.3.1", {"start": v(149.22, 9.46) * mm, "end": v(133.35, 16.22) * mm});
            skLineSegment(sketch, "E27.4.3.2", {"start": v(133.35, 2.7) * mm, "end": v(149.22, 9.46) * mm});
            skLineSegment(sketch, "E27.4.3.3", {"start": v(117.47, 9.46) * mm, "end": v(133.35, 2.7) * mm});
            skLineSegment(sketch, "E27.4.4.0", {"start": v(133.35, 35.15) * mm, "end": v(117.47, 28.38) * mm});
            skLineSegment(sketch, "E27.4.4.1", {"start": v(149.22, 28.38) * mm, "end": v(133.35, 35.15) * mm});
            skLineSegment(sketch, "E27.4.4.2", {"start": v(133.35, 21.62) * mm, "end": v(149.22, 28.38) * mm});
            skLineSegment(sketch, "E27.4.4.3", {"start": v(117.47, 28.38) * mm, "end": v(133.35, 21.62) * mm});
            skLineSegment(sketch, "E27.4.5.0", {"start": v(133.35, 54.07) * mm, "end": v(117.47, 47.3) * mm});
            skLineSegment(sketch, "E27.4.5.1", {"start": v(149.22, 47.3) * mm, "end": v(133.35, 54.07) * mm});
            skLineSegment(sketch, "E27.4.5.2", {"start": v(133.35, 40.54) * mm, "end": v(149.22, 47.3) * mm});
            skLineSegment(sketch, "E27.4.5.3", {"start": v(117.47, 47.3) * mm, "end": v(133.35, 40.54) * mm});
            skLineSegment(sketch, "E27.5.0.0", {"start": v(95.25, -40.54) * mm, "end": v(79.37, -47.3) * mm});
            skLineSegment(sketch, "E27.5.0.1", {"start": v(111.12, -47.3) * mm, "end": v(95.25, -40.54) * mm});
            skLineSegment(sketch, "E27.5.0.2", {"start": v(95.25, -54.07) * mm, "end": v(111.12, -47.3) * mm});
            skLineSegment(sketch, "E27.5.0.3", {"start": v(79.37, -47.3) * mm, "end": v(95.25, -54.07) * mm});
            skLineSegment(sketch, "E27.5.1.0", {"start": v(95.25, -21.62) * mm, "end": v(79.37, -28.38) * mm});
            skLineSegment(sketch, "E27.5.1.1", {"start": v(111.12, -28.38) * mm, "end": v(95.25, -21.62) * mm});
            skLineSegment(sketch, "E27.5.1.2", {"start": v(95.25, -35.15) * mm, "end": v(111.12, -28.38) * mm});
            skLineSegment(sketch, "E27.5.1.3", {"start": v(79.37, -28.38) * mm, "end": v(95.25, -35.15) * mm});
            skLineSegment(sketch, "E27.5.2.0", {"start": v(95.25, -2.7) * mm, "end": v(79.37, -9.46) * mm});
            skLineSegment(sketch, "E27.5.2.1", {"start": v(111.12, -9.46) * mm, "end": v(95.25, -2.7) * mm});
            skLineSegment(sketch, "E27.5.2.2", {"start": v(95.25, -16.22) * mm, "end": v(111.12, -9.46) * mm});
            skLineSegment(sketch, "E27.5.2.3", {"start": v(79.37, -9.46) * mm, "end": v(95.25, -16.22) * mm});
            skLineSegment(sketch, "E27.5.3.0", {"start": v(95.25, 16.22) * mm, "end": v(79.37, 9.46) * mm});
            skLineSegment(sketch, "E27.5.3.1", {"start": v(111.12, 9.46) * mm, "end": v(95.25, 16.22) * mm});
            skLineSegment(sketch, "E27.5.3.2", {"start": v(95.25, 2.7) * mm, "end": v(111.12, 9.46) * mm});
            skLineSegment(sketch, "E27.5.3.3", {"start": v(79.37, 9.46) * mm, "end": v(95.25, 2.7) * mm});
            skLineSegment(sketch, "E27.5.4.0", {"start": v(95.25, 35.15) * mm, "end": v(79.37, 28.38) * mm});
            skLineSegment(sketch, "E27.5.4.1", {"start": v(111.12, 28.38) * mm, "end": v(95.25, 35.15) * mm});
            skLineSegment(sketch, "E27.5.4.2", {"start": v(95.25, 21.62) * mm, "end": v(111.12, 28.38) * mm});
            skLineSegment(sketch, "E27.5.4.3", {"start": v(79.37, 28.38) * mm, "end": v(95.25, 21.62) * mm});
            skLineSegment(sketch, "E27.5.5.0", {"start": v(95.25, 54.07) * mm, "end": v(79.37, 47.3) * mm});
            skLineSegment(sketch, "E27.5.5.1", {"start": v(111.12, 47.3) * mm, "end": v(95.25, 54.07) * mm});
            skLineSegment(sketch, "E27.5.5.2", {"start": v(95.25, 40.54) * mm, "end": v(111.12, 47.3) * mm});
            skLineSegment(sketch, "E27.5.5.3", {"start": v(79.37, 47.3) * mm, "end": v(95.25, 40.54) * mm});
            skLineSegment(sketch, "E27.6.0.0", {"start": v(57.15, -40.54) * mm, "end": v(41.27, -47.3) * mm});
            skLineSegment(sketch, "E27.6.0.1", {"start": v(73.02, -47.3) * mm, "end": v(57.15, -40.54) * mm});
            skLineSegment(sketch, "E27.6.0.2", {"start": v(57.15, -54.07) * mm, "end": v(73.02, -47.3) * mm});
            skLineSegment(sketch, "E27.6.0.3", {"start": v(41.27, -47.3) * mm, "end": v(57.15, -54.07) * mm});
            skLineSegment(sketch, "E27.6.1.0", {"start": v(57.15, -21.62) * mm, "end": v(41.27, -28.38) * mm});
            skLineSegment(sketch, "E27.6.1.1", {"start": v(73.02, -28.38) * mm, "end": v(57.15, -21.62) * mm});
            skLineSegment(sketch, "E27.6.1.2", {"start": v(57.15, -35.15) * mm, "end": v(73.02, -28.38) * mm});
            skLineSegment(sketch, "E27.6.1.3", {"start": v(41.27, -28.38) * mm, "end": v(57.15, -35.15) * mm});
            skLineSegment(sketch, "E27.6.2.0", {"start": v(57.15, -2.7) * mm, "end": v(41.27, -9.46) * mm});
            skLineSegment(sketch, "E27.6.2.1", {"start": v(73.02, -9.46) * mm, "end": v(57.15, -2.7) * mm});
            skLineSegment(sketch, "E27.6.2.2", {"start": v(57.15, -16.22) * mm, "end": v(73.02, -9.46) * mm});
            skLineSegment(sketch, "E27.6.2.3", {"start": v(41.27, -9.46) * mm, "end": v(57.15, -16.22) * mm});
            skLineSegment(sketch, "E27.6.3.0", {"start": v(57.15, 16.22) * mm, "end": v(41.27, 9.46) * mm});
            skLineSegment(sketch, "E27.6.3.1", {"start": v(73.02, 9.46) * mm, "end": v(57.15, 16.22) * mm});
            skLineSegment(sketch, "E27.6.3.2", {"start": v(57.15, 2.7) * mm, "end": v(73.02, 9.46) * mm});
            skLineSegment(sketch, "E27.6.3.3", {"start": v(41.27, 9.46) * mm, "end": v(57.15, 2.7) * mm});
            skLineSegment(sketch, "E27.6.4.0", {"start": v(57.15, 35.15) * mm, "end": v(41.27, 28.38) * mm});
            skLineSegment(sketch, "E27.6.4.1", {"start": v(73.02, 28.38) * mm, "end": v(57.15, 35.15) * mm});
            skLineSegment(sketch, "E27.6.4.2", {"start": v(57.15, 21.62) * mm, "end": v(73.02, 28.38) * mm});
            skLineSegment(sketch, "E27.6.4.3", {"start": v(41.27, 28.38) * mm, "end": v(57.15, 21.62) * mm});
            skLineSegment(sketch, "E27.6.5.0", {"start": v(57.15, 54.07) * mm, "end": v(41.27, 47.3) * mm});
            skLineSegment(sketch, "E27.6.5.1", {"start": v(73.02, 47.3) * mm, "end": v(57.15, 54.07) * mm});
            skLineSegment(sketch, "E27.6.5.2", {"start": v(57.15, 40.54) * mm, "end": v(73.02, 47.3) * mm});
            skLineSegment(sketch, "E27.6.5.3", {"start": v(41.27, 47.3) * mm, "end": v(57.15, 40.54) * mm});
            skLineSegment(sketch, "E27.7.0.0", {"start": v(19.05, -40.54) * mm, "end": v(3.17, -47.3) * mm});
            skLineSegment(sketch, "E27.7.0.1", {"start": v(34.92, -47.3) * mm, "end": v(19.05, -40.54) * mm});
            skLineSegment(sketch, "E27.7.0.2", {"start": v(19.05, -54.07) * mm, "end": v(34.92, -47.3) * mm});
            skLineSegment(sketch, "E27.7.0.3", {"start": v(3.17, -47.3) * mm, "end": v(19.05, -54.07) * mm});
            skLineSegment(sketch, "E27.7.1.0", {"start": v(19.05, -21.62) * mm, "end": v(3.17, -28.38) * mm});
            skLineSegment(sketch, "E27.7.1.1", {"start": v(34.92, -28.38) * mm, "end": v(19.05, -21.62) * mm});
            skLineSegment(sketch, "E27.7.1.2", {"start": v(19.05, -35.15) * mm, "end": v(34.92, -28.38) * mm});
            skLineSegment(sketch, "E27.7.1.3", {"start": v(3.17, -28.38) * mm, "end": v(19.05, -35.15) * mm});
            skLineSegment(sketch, "E27.7.2.0", {"start": v(19.05, -2.7) * mm, "end": v(3.17, -9.46) * mm});
            skLineSegment(sketch, "E27.7.2.1", {"start": v(34.92, -9.46) * mm, "end": v(19.05, -2.7) * mm});
            skLineSegment(sketch, "E27.7.2.2", {"start": v(19.05, -16.22) * mm, "end": v(34.92, -9.46) * mm});
            skLineSegment(sketch, "E27.7.2.3", {"start": v(3.17, -9.46) * mm, "end": v(19.05, -16.22) * mm});
            skLineSegment(sketch, "E27.7.3.0", {"start": v(19.05, 16.22) * mm, "end": v(3.17, 9.46) * mm});
            skLineSegment(sketch, "E27.7.3.1", {"start": v(34.92, 9.46) * mm, "end": v(19.05, 16.22) * mm});
            skLineSegment(sketch, "E27.7.3.2", {"start": v(19.05, 2.7) * mm, "end": v(34.92, 9.46) * mm});
            skLineSegment(sketch, "E27.7.3.3", {"start": v(3.17, 9.46) * mm, "end": v(19.05, 2.7) * mm});
            skLineSegment(sketch, "E27.7.4.0", {"start": v(19.05, 35.15) * mm, "end": v(3.17, 28.38) * mm});
            skLineSegment(sketch, "E27.7.4.1", {"start": v(34.92, 28.38) * mm, "end": v(19.05, 35.15) * mm});
            skLineSegment(sketch, "E27.7.4.2", {"start": v(19.05, 21.62) * mm, "end": v(34.92, 28.38) * mm});
            skLineSegment(sketch, "E27.7.4.3", {"start": v(3.17, 28.38) * mm, "end": v(19.05, 21.62) * mm});
            skLineSegment(sketch, "E27.7.5.0", {"start": v(19.05, 54.07) * mm, "end": v(3.17, 47.3) * mm});
            skLineSegment(sketch, "E27.7.5.1", {"start": v(34.92, 47.3) * mm, "end": v(19.05, 54.07) * mm});
            skLineSegment(sketch, "E27.7.5.2", {"start": v(19.05, 40.54) * mm, "end": v(34.92, 47.3) * mm});
            skLineSegment(sketch, "E27.7.5.3", {"start": v(3.17, 47.3) * mm, "end": v(19.05, 40.54) * mm});
            skLineSegment(sketch, "E27.8.0.0", {"start": v(-19.05, -40.54) * mm, "end": v(-34.93, -47.3) * mm});
            skLineSegment(sketch, "E27.8.0.1", {"start": v(-3.18, -47.3) * mm, "end": v(-19.05, -40.54) * mm});
            skLineSegment(sketch, "E27.8.0.2", {"start": v(-19.05, -54.07) * mm, "end": v(-3.18, -47.3) * mm});
            skLineSegment(sketch, "E27.8.0.3", {"start": v(-34.93, -47.3) * mm, "end": v(-19.05, -54.07) * mm});
            skLineSegment(sketch, "E27.8.1.0", {"start": v(-19.05, -21.62) * mm, "end": v(-34.93, -28.38) * mm});
            skLineSegment(sketch, "E27.8.1.1", {"start": v(-3.18, -28.38) * mm, "end": v(-19.05, -21.62) * mm});
            skLineSegment(sketch, "E27.8.1.2", {"start": v(-19.05, -35.15) * mm, "end": v(-3.18, -28.38) * mm});
            skLineSegment(sketch, "E27.8.1.3", {"start": v(-34.93, -28.38) * mm, "end": v(-19.05, -35.15) * mm});
            skLineSegment(sketch, "E27.8.2.0", {"start": v(-19.05, -2.7) * mm, "end": v(-34.93, -9.46) * mm});
            skLineSegment(sketch, "E27.8.2.1", {"start": v(-3.18, -9.46) * mm, "end": v(-19.05, -2.7) * mm});
            skLineSegment(sketch, "E27.8.2.2", {"start": v(-19.05, -16.22) * mm, "end": v(-3.18, -9.46) * mm});
            skLineSegment(sketch, "E27.8.2.3", {"start": v(-34.93, -9.46) * mm, "end": v(-19.05, -16.22) * mm});
            skLineSegment(sketch, "E27.8.3.0", {"start": v(-19.05, 16.22) * mm, "end": v(-34.93, 9.46) * mm});
            skLineSegment(sketch, "E27.8.3.1", {"start": v(-3.18, 9.46) * mm, "end": v(-19.05, 16.22) * mm});
            skLineSegment(sketch, "E27.8.3.2", {"start": v(-19.05, 2.7) * mm, "end": v(-3.18, 9.46) * mm});
            skLineSegment(sketch, "E27.8.3.3", {"start": v(-34.93, 9.46) * mm, "end": v(-19.05, 2.7) * mm});
            skLineSegment(sketch, "E27.8.4.0", {"start": v(-19.05, 35.15) * mm, "end": v(-34.93, 28.38) * mm});
            skLineSegment(sketch, "E27.8.4.1", {"start": v(-3.18, 28.38) * mm, "end": v(-19.05, 35.15) * mm});
            skLineSegment(sketch, "E27.8.4.2", {"start": v(-19.05, 21.62) * mm, "end": v(-3.18, 28.38) * mm});
            skLineSegment(sketch, "E27.8.4.3", {"start": v(-34.93, 28.38) * mm, "end": v(-19.05, 21.62) * mm});
            skLineSegment(sketch, "E27.8.5.0", {"start": v(-19.05, 54.07) * mm, "end": v(-34.93, 47.3) * mm});
            skLineSegment(sketch, "E27.8.5.1", {"start": v(-3.18, 47.3) * mm, "end": v(-19.05, 54.07) * mm});
            skLineSegment(sketch, "E27.8.5.2", {"start": v(-19.05, 40.54) * mm, "end": v(-3.18, 47.3) * mm});
            skLineSegment(sketch, "E27.8.5.3", {"start": v(-34.93, 47.3) * mm, "end": v(-19.05, 40.54) * mm});
            skLineSegment(sketch, "E27.9.0.0", {"start": v(-57.15, -40.54) * mm, "end": v(-73.03, -47.3) * mm});
            skLineSegment(sketch, "E27.9.0.1", {"start": v(-41.28, -47.3) * mm, "end": v(-57.15, -40.54) * mm});
            skLineSegment(sketch, "E27.9.0.2", {"start": v(-57.15, -54.07) * mm, "end": v(-41.28, -47.3) * mm});
            skLineSegment(sketch, "E27.9.0.3", {"start": v(-73.03, -47.3) * mm, "end": v(-57.15, -54.07) * mm});
            skLineSegment(sketch, "E27.9.1.0", {"start": v(-57.15, -21.62) * mm, "end": v(-73.03, -28.38) * mm});
            skLineSegment(sketch, "E27.9.1.1", {"start": v(-41.28, -28.38) * mm, "end": v(-57.15, -21.62) * mm});
            skLineSegment(sketch, "E27.9.1.2", {"start": v(-57.15, -35.15) * mm, "end": v(-41.28, -28.38) * mm});
            skLineSegment(sketch, "E27.9.1.3", {"start": v(-73.03, -28.38) * mm, "end": v(-57.15, -35.15) * mm});
            skLineSegment(sketch, "E27.9.2.0", {"start": v(-57.15, -2.7) * mm, "end": v(-73.03, -9.46) * mm});
            skLineSegment(sketch, "E27.9.2.1", {"start": v(-41.28, -9.46) * mm, "end": v(-57.15, -2.7) * mm});
            skLineSegment(sketch, "E27.9.2.2", {"start": v(-57.15, -16.22) * mm, "end": v(-41.28, -9.46) * mm});
            skLineSegment(sketch, "E27.9.2.3", {"start": v(-73.03, -9.46) * mm, "end": v(-57.15, -16.22) * mm});
            skLineSegment(sketch, "E27.9.3.0", {"start": v(-57.15, 16.22) * mm, "end": v(-73.03, 9.46) * mm});
            skLineSegment(sketch, "E27.9.3.1", {"start": v(-41.28, 9.46) * mm, "end": v(-57.15, 16.22) * mm});
            skLineSegment(sketch, "E27.9.3.2", {"start": v(-57.15, 2.7) * mm, "end": v(-41.28, 9.46) * mm});
            skLineSegment(sketch, "E27.9.3.3", {"start": v(-73.03, 9.46) * mm, "end": v(-57.15, 2.7) * mm});
            skLineSegment(sketch, "E27.9.4.0", {"start": v(-57.15, 35.15) * mm, "end": v(-73.03, 28.38) * mm});
            skLineSegment(sketch, "E27.9.4.1", {"start": v(-41.28, 28.38) * mm, "end": v(-57.15, 35.15) * mm});
            skLineSegment(sketch, "E27.9.4.2", {"start": v(-57.15, 21.62) * mm, "end": v(-41.28, 28.38) * mm});
            skLineSegment(sketch, "E27.9.4.3", {"start": v(-73.03, 28.38) * mm, "end": v(-57.15, 21.62) * mm});
            skLineSegment(sketch, "E27.9.5.0", {"start": v(-57.15, 54.07) * mm, "end": v(-73.03, 47.3) * mm});
            skLineSegment(sketch, "E27.9.5.1", {"start": v(-41.28, 47.3) * mm, "end": v(-57.15, 54.07) * mm});
            skLineSegment(sketch, "E27.9.5.2", {"start": v(-57.15, 40.54) * mm, "end": v(-41.28, 47.3) * mm});
            skLineSegment(sketch, "E27.9.5.3", {"start": v(-73.03, 47.3) * mm, "end": v(-57.15, 40.54) * mm});
            skLineSegment(sketch, "E27.10.0.0", {"start": v(-95.25, -40.54) * mm, "end": v(-111.13, -47.3) * mm});
            skLineSegment(sketch, "E27.10.0.1", {"start": v(-79.38, -47.3) * mm, "end": v(-95.25, -40.54) * mm});
            skLineSegment(sketch, "E27.10.0.2", {"start": v(-95.25, -54.07) * mm, "end": v(-79.38, -47.3) * mm});
            skLineSegment(sketch, "E27.10.0.3", {"start": v(-111.13, -47.3) * mm, "end": v(-95.25, -54.07) * mm});
            skLineSegment(sketch, "E27.10.1.0", {"start": v(-95.25, -21.62) * mm, "end": v(-111.13, -28.38) * mm});
            skLineSegment(sketch, "E27.10.1.1", {"start": v(-79.38, -28.38) * mm, "end": v(-95.25, -21.62) * mm});
            skLineSegment(sketch, "E27.10.1.2", {"start": v(-95.25, -35.15) * mm, "end": v(-79.38, -28.38) * mm});
            skLineSegment(sketch, "E27.10.1.3", {"start": v(-111.13, -28.38) * mm, "end": v(-95.25, -35.15) * mm});
            skLineSegment(sketch, "E27.10.2.0", {"start": v(-95.25, -2.7) * mm, "end": v(-111.13, -9.46) * mm});
            skLineSegment(sketch, "E27.10.2.1", {"start": v(-79.38, -9.46) * mm, "end": v(-95.25, -2.7) * mm});
            skLineSegment(sketch, "E27.10.2.2", {"start": v(-95.25, -16.22) * mm, "end": v(-79.38, -9.46) * mm});
            skLineSegment(sketch, "E27.10.2.3", {"start": v(-111.13, -9.46) * mm, "end": v(-95.25, -16.22) * mm});
            skLineSegment(sketch, "E27.10.3.0", {"start": v(-95.25, 16.22) * mm, "end": v(-111.13, 9.46) * mm});
            skLineSegment(sketch, "E27.10.3.1", {"start": v(-79.38, 9.46) * mm, "end": v(-95.25, 16.22) * mm});
            skLineSegment(sketch, "E27.10.3.2", {"start": v(-95.25, 2.7) * mm, "end": v(-79.38, 9.46) * mm});
            skLineSegment(sketch, "E27.10.3.3", {"start": v(-111.13, 9.46) * mm, "end": v(-95.25, 2.7) * mm});
            skLineSegment(sketch, "E27.10.4.0", {"start": v(-95.25, 35.15) * mm, "end": v(-111.13, 28.38) * mm});
            skLineSegment(sketch, "E27.10.4.1", {"start": v(-79.38, 28.38) * mm, "end": v(-95.25, 35.15) * mm});
            skLineSegment(sketch, "E27.10.4.2", {"start": v(-95.25, 21.62) * mm, "end": v(-79.38, 28.38) * mm});
            skLineSegment(sketch, "E27.10.4.3", {"start": v(-111.13, 28.38) * mm, "end": v(-95.25, 21.62) * mm});
            skLineSegment(sketch, "E27.10.5.0", {"start": v(-95.25, 54.07) * mm, "end": v(-111.13, 47.3) * mm});
            skLineSegment(sketch, "E27.10.5.1", {"start": v(-79.38, 47.3) * mm, "end": v(-95.25, 54.07) * mm});
            skLineSegment(sketch, "E27.10.5.2", {"start": v(-95.25, 40.54) * mm, "end": v(-79.38, 47.3) * mm});
            skLineSegment(sketch, "E27.10.5.3", {"start": v(-111.13, 47.3) * mm, "end": v(-95.25, 40.54) * mm});
            skLineSegment(sketch, "E27.11.0.0", {"start": v(-133.35, -40.54) * mm, "end": v(-149.23, -47.3) * mm});
            skLineSegment(sketch, "E27.11.0.1", {"start": v(-117.48, -47.3) * mm, "end": v(-133.35, -40.54) * mm});
            skLineSegment(sketch, "E27.11.0.2", {"start": v(-133.35, -54.07) * mm, "end": v(-117.48, -47.3) * mm});
            skLineSegment(sketch, "E27.11.0.3", {"start": v(-149.23, -47.3) * mm, "end": v(-133.35, -54.07) * mm});
            skLineSegment(sketch, "E27.11.1.0", {"start": v(-133.35, -21.62) * mm, "end": v(-149.23, -28.38) * mm});
            skLineSegment(sketch, "E27.11.1.1", {"start": v(-117.48, -28.38) * mm, "end": v(-133.35, -21.62) * mm});
            skLineSegment(sketch, "E27.11.1.2", {"start": v(-133.35, -35.15) * mm, "end": v(-117.48, -28.38) * mm});
            skLineSegment(sketch, "E27.11.1.3", {"start": v(-149.23, -28.38) * mm, "end": v(-133.35, -35.15) * mm});
            skLineSegment(sketch, "E27.11.2.0", {"start": v(-133.35, -2.7) * mm, "end": v(-149.23, -9.46) * mm});
            skLineSegment(sketch, "E27.11.2.1", {"start": v(-117.48, -9.46) * mm, "end": v(-133.35, -2.7) * mm});
            skLineSegment(sketch, "E27.11.2.2", {"start": v(-133.35, -16.22) * mm, "end": v(-117.48, -9.46) * mm});
            skLineSegment(sketch, "E27.11.2.3", {"start": v(-149.23, -9.46) * mm, "end": v(-133.35, -16.22) * mm});
            skLineSegment(sketch, "E27.11.3.0", {"start": v(-133.35, 16.22) * mm, "end": v(-149.23, 9.46) * mm});
            skLineSegment(sketch, "E27.11.3.1", {"start": v(-117.48, 9.46) * mm, "end": v(-133.35, 16.22) * mm});
            skLineSegment(sketch, "E27.11.3.2", {"start": v(-133.35, 2.7) * mm, "end": v(-117.48, 9.46) * mm});
            skLineSegment(sketch, "E27.11.3.3", {"start": v(-149.23, 9.46) * mm, "end": v(-133.35, 2.7) * mm});
            skLineSegment(sketch, "E27.11.4.0", {"start": v(-133.35, 35.15) * mm, "end": v(-149.23, 28.38) * mm});
            skLineSegment(sketch, "E27.11.4.1", {"start": v(-117.48, 28.38) * mm, "end": v(-133.35, 35.15) * mm});
            skLineSegment(sketch, "E27.11.4.2", {"start": v(-133.35, 21.62) * mm, "end": v(-117.48, 28.38) * mm});
            skLineSegment(sketch, "E27.11.4.3", {"start": v(-149.23, 28.38) * mm, "end": v(-133.35, 21.62) * mm});
            skLineSegment(sketch, "E27.11.5.0", {"start": v(-133.35, 54.07) * mm, "end": v(-149.23, 47.3) * mm});
            skLineSegment(sketch, "E27.11.5.1", {"start": v(-117.48, 47.3) * mm, "end": v(-133.35, 54.07) * mm});
            skLineSegment(sketch, "E27.11.5.2", {"start": v(-133.35, 40.54) * mm, "end": v(-117.48, 47.3) * mm});
            skLineSegment(sketch, "E27.11.5.3", {"start": v(-149.23, 47.3) * mm, "end": v(-133.35, 40.54) * mm});
            skLineSegment(sketch, "E27.12.0.0", {"start": v(-171.45, -40.54) * mm, "end": v(-187.33, -47.3) * mm});
            skLineSegment(sketch, "E27.12.0.1", {"start": v(-155.58, -47.3) * mm, "end": v(-171.45, -40.54) * mm});
            skLineSegment(sketch, "E27.12.0.2", {"start": v(-171.45, -54.07) * mm, "end": v(-155.58, -47.3) * mm});
            skLineSegment(sketch, "E27.12.0.3", {"start": v(-187.33, -47.3) * mm, "end": v(-171.45, -54.07) * mm});
            skLineSegment(sketch, "E27.12.1.0", {"start": v(-171.45, -21.62) * mm, "end": v(-187.33, -28.38) * mm});
            skLineSegment(sketch, "E27.12.1.1", {"start": v(-155.58, -28.38) * mm, "end": v(-171.45, -21.62) * mm});
            skLineSegment(sketch, "E27.12.1.2", {"start": v(-171.45, -35.15) * mm, "end": v(-155.58, -28.38) * mm});
            skLineSegment(sketch, "E27.12.1.3", {"start": v(-187.33, -28.38) * mm, "end": v(-171.45, -35.15) * mm});
            skLineSegment(sketch, "E27.12.2.0", {"start": v(-171.45, -2.7) * mm, "end": v(-187.33, -9.46) * mm});
            skLineSegment(sketch, "E27.12.2.1", {"start": v(-155.58, -9.46) * mm, "end": v(-171.45, -2.7) * mm});
            skLineSegment(sketch, "E27.12.2.2", {"start": v(-171.45, -16.22) * mm, "end": v(-155.58, -9.46) * mm});
            skLineSegment(sketch, "E27.12.2.3", {"start": v(-187.33, -9.46) * mm, "end": v(-171.45, -16.22) * mm});
            skLineSegment(sketch, "E27.12.3.0", {"start": v(-171.45, 16.22) * mm, "end": v(-187.33, 9.46) * mm});
            skLineSegment(sketch, "E27.12.3.1", {"start": v(-155.58, 9.46) * mm, "end": v(-171.45, 16.22) * mm});
            skLineSegment(sketch, "E27.12.3.2", {"start": v(-171.45, 2.7) * mm, "end": v(-155.58, 9.46) * mm});
            skLineSegment(sketch, "E27.12.3.3", {"start": v(-187.33, 9.46) * mm, "end": v(-171.45, 2.7) * mm});
            skLineSegment(sketch, "E27.12.4.0", {"start": v(-171.45, 35.15) * mm, "end": v(-187.33, 28.38) * mm});
            skLineSegment(sketch, "E27.12.4.1", {"start": v(-155.58, 28.38) * mm, "end": v(-171.45, 35.15) * mm});
            skLineSegment(sketch, "E27.12.4.2", {"start": v(-171.45, 21.62) * mm, "end": v(-155.58, 28.38) * mm});
            skLineSegment(sketch, "E27.12.4.3", {"start": v(-187.33, 28.38) * mm, "end": v(-171.45, 21.62) * mm});
            skLineSegment(sketch, "E27.12.5.0", {"start": v(-171.45, 54.07) * mm, "end": v(-187.33, 47.3) * mm});
            skLineSegment(sketch, "E27.12.5.1", {"start": v(-155.58, 47.3) * mm, "end": v(-171.45, 54.07) * mm});
            skLineSegment(sketch, "E27.12.5.2", {"start": v(-171.45, 40.54) * mm, "end": v(-155.58, 47.3) * mm});
            skLineSegment(sketch, "E27.12.5.3", {"start": v(-187.33, 47.3) * mm, "end": v(-171.45, 40.54) * mm});
            skLineSegment(sketch, "E27.13.0.0", {"start": v(-209.55, -40.54) * mm, "end": v(-225.43, -47.3) * mm});
            skLineSegment(sketch, "E27.13.0.1", {"start": v(-193.68, -47.3) * mm, "end": v(-209.55, -40.54) * mm});
            skLineSegment(sketch, "E27.13.0.2", {"start": v(-209.55, -54.07) * mm, "end": v(-193.68, -47.3) * mm});
            skLineSegment(sketch, "E27.13.0.3", {"start": v(-225.43, -47.3) * mm, "end": v(-209.55, -54.07) * mm});
            skLineSegment(sketch, "E27.13.1.0", {"start": v(-209.55, -21.62) * mm, "end": v(-225.43, -28.38) * mm});
            skLineSegment(sketch, "E27.13.1.1", {"start": v(-193.68, -28.38) * mm, "end": v(-209.55, -21.62) * mm});
            skLineSegment(sketch, "E27.13.1.2", {"start": v(-209.55, -35.15) * mm, "end": v(-193.68, -28.38) * mm});
            skLineSegment(sketch, "E27.13.1.3", {"start": v(-225.43, -28.38) * mm, "end": v(-209.55, -35.15) * mm});
            skLineSegment(sketch, "E27.13.2.0", {"start": v(-209.55, -2.7) * mm, "end": v(-225.43, -9.46) * mm});
            skLineSegment(sketch, "E27.13.2.1", {"start": v(-193.68, -9.46) * mm, "end": v(-209.55, -2.7) * mm});
            skLineSegment(sketch, "E27.13.2.2", {"start": v(-209.55, -16.22) * mm, "end": v(-193.68, -9.46) * mm});
            skLineSegment(sketch, "E27.13.2.3", {"start": v(-225.43, -9.46) * mm, "end": v(-209.55, -16.22) * mm});
            skLineSegment(sketch, "E27.13.3.0", {"start": v(-209.55, 16.22) * mm, "end": v(-225.43, 9.46) * mm});
            skLineSegment(sketch, "E27.13.3.1", {"start": v(-193.68, 9.46) * mm, "end": v(-209.55, 16.22) * mm});
            skLineSegment(sketch, "E27.13.3.2", {"start": v(-209.55, 2.7) * mm, "end": v(-193.68, 9.46) * mm});
            skLineSegment(sketch, "E27.13.3.3", {"start": v(-225.43, 9.46) * mm, "end": v(-209.55, 2.7) * mm});
            skLineSegment(sketch, "E27.13.4.0", {"start": v(-209.55, 35.15) * mm, "end": v(-225.43, 28.38) * mm});
            skLineSegment(sketch, "E27.13.4.1", {"start": v(-193.68, 28.38) * mm, "end": v(-209.55, 35.15) * mm});
            skLineSegment(sketch, "E27.13.4.2", {"start": v(-209.55, 21.62) * mm, "end": v(-193.68, 28.38) * mm});
            skLineSegment(sketch, "E27.13.4.3", {"start": v(-225.43, 28.38) * mm, "end": v(-209.55, 21.62) * mm});
            skLineSegment(sketch, "E27.13.5.0", {"start": v(-209.55, 54.07) * mm, "end": v(-225.43, 47.3) * mm});
            skLineSegment(sketch, "E27.13.5.1", {"start": v(-193.68, 47.3) * mm, "end": v(-209.55, 54.07) * mm});
            skLineSegment(sketch, "E27.13.5.2", {"start": v(-209.55, 40.54) * mm, "end": v(-193.68, 47.3) * mm});
            skLineSegment(sketch, "E27.13.5.3", {"start": v(-225.43, 47.3) * mm, "end": v(-209.55, 40.54) * mm});
            skLineSegment(sketch, "E27.14.0.0", {"start": v(-247.65, -40.54) * mm, "end": v(-263.53, -47.3) * mm});
            skLineSegment(sketch, "E27.14.0.1", {"start": v(-231.78, -47.3) * mm, "end": v(-247.65, -40.54) * mm});
            skLineSegment(sketch, "E27.14.0.2", {"start": v(-247.65, -54.07) * mm, "end": v(-231.78, -47.3) * mm});
            skLineSegment(sketch, "E27.14.0.3", {"start": v(-263.53, -47.3) * mm, "end": v(-247.65, -54.07) * mm});
            skLineSegment(sketch, "E27.14.1.0", {"start": v(-247.65, -21.62) * mm, "end": v(-263.53, -28.38) * mm});
            skLineSegment(sketch, "E27.14.1.1", {"start": v(-231.78, -28.38) * mm, "end": v(-247.65, -21.62) * mm});
            skLineSegment(sketch, "E27.14.1.2", {"start": v(-247.65, -35.15) * mm, "end": v(-231.78, -28.38) * mm});
            skLineSegment(sketch, "E27.14.1.3", {"start": v(-263.53, -28.38) * mm, "end": v(-247.65, -35.15) * mm});
            skLineSegment(sketch, "E27.14.2.0", {"start": v(-247.65, -2.7) * mm, "end": v(-263.53, -9.46) * mm});
            skLineSegment(sketch, "E27.14.2.1", {"start": v(-231.78, -9.46) * mm, "end": v(-247.65, -2.7) * mm});
            skLineSegment(sketch, "E27.14.2.2", {"start": v(-247.65, -16.22) * mm, "end": v(-231.78, -9.46) * mm});
            skLineSegment(sketch, "E27.14.2.3", {"start": v(-263.53, -9.46) * mm, "end": v(-247.65, -16.22) * mm});
            skLineSegment(sketch, "E27.14.3.0", {"start": v(-247.65, 16.22) * mm, "end": v(-263.53, 9.46) * mm});
            skLineSegment(sketch, "E27.14.3.1", {"start": v(-231.78, 9.46) * mm, "end": v(-247.65, 16.22) * mm});
            skLineSegment(sketch, "E27.14.3.2", {"start": v(-247.65, 2.7) * mm, "end": v(-231.78, 9.46) * mm});
            skLineSegment(sketch, "E27.14.3.3", {"start": v(-263.53, 9.46) * mm, "end": v(-247.65, 2.7) * mm});
            skLineSegment(sketch, "E27.14.4.0", {"start": v(-247.65, 35.15) * mm, "end": v(-263.53, 28.38) * mm});
            skLineSegment(sketch, "E27.14.4.1", {"start": v(-231.78, 28.38) * mm, "end": v(-247.65, 35.15) * mm});
            skLineSegment(sketch, "E27.14.4.2", {"start": v(-247.65, 21.62) * mm, "end": v(-231.78, 28.38) * mm});
            skLineSegment(sketch, "E27.14.4.3", {"start": v(-263.53, 28.38) * mm, "end": v(-247.65, 21.62) * mm});
            skLineSegment(sketch, "E27.14.5.0", {"start": v(-247.65, 54.07) * mm, "end": v(-263.53, 47.3) * mm});
            skLineSegment(sketch, "E27.14.5.1", {"start": v(-231.78, 47.3) * mm, "end": v(-247.65, 54.07) * mm});
            skLineSegment(sketch, "E27.14.5.2", {"start": v(-247.65, 40.54) * mm, "end": v(-231.78, 47.3) * mm});
            skLineSegment(sketch, "E27.14.5.3", {"start": v(-263.53, 47.3) * mm, "end": v(-247.65, 40.54) * mm});
            skLineSegment(sketch, "E27.15.0.0", {"start": v(-285.75, -40.54) * mm, "end": v(-301.63, -47.3) * mm});
            skLineSegment(sketch, "E27.15.0.1", {"start": v(-269.88, -47.3) * mm, "end": v(-285.75, -40.54) * mm});
            skLineSegment(sketch, "E27.15.0.2", {"start": v(-285.75, -54.07) * mm, "end": v(-269.88, -47.3) * mm});
            skLineSegment(sketch, "E27.15.0.3", {"start": v(-301.63, -47.3) * mm, "end": v(-285.75, -54.07) * mm});
            skLineSegment(sketch, "E27.15.1.0", {"start": v(-285.75, -21.62) * mm, "end": v(-301.63, -28.38) * mm});
            skLineSegment(sketch, "E27.15.1.1", {"start": v(-269.88, -28.38) * mm, "end": v(-285.75, -21.62) * mm});
            skLineSegment(sketch, "E27.15.1.2", {"start": v(-285.75, -35.15) * mm, "end": v(-269.88, -28.38) * mm});
            skLineSegment(sketch, "E27.15.1.3", {"start": v(-301.63, -28.38) * mm, "end": v(-285.75, -35.15) * mm});
            skLineSegment(sketch, "E27.15.2.0", {"start": v(-285.75, -2.7) * mm, "end": v(-301.63, -9.46) * mm});
            skLineSegment(sketch, "E27.15.2.1", {"start": v(-269.88, -9.46) * mm, "end": v(-285.75, -2.7) * mm});
            skLineSegment(sketch, "E27.15.2.2", {"start": v(-285.75, -16.22) * mm, "end": v(-269.88, -9.46) * mm});
            skLineSegment(sketch, "E27.15.2.3", {"start": v(-301.63, -9.46) * mm, "end": v(-285.75, -16.22) * mm});
            skLineSegment(sketch, "E27.15.3.0", {"start": v(-285.75, 16.22) * mm, "end": v(-301.63, 9.46) * mm});
            skLineSegment(sketch, "E27.15.3.1", {"start": v(-269.88, 9.46) * mm, "end": v(-285.75, 16.22) * mm});
            skLineSegment(sketch, "E27.15.3.2", {"start": v(-285.75, 2.7) * mm, "end": v(-269.88, 9.46) * mm});
            skLineSegment(sketch, "E27.15.3.3", {"start": v(-301.63, 9.46) * mm, "end": v(-285.75, 2.7) * mm});
            skLineSegment(sketch, "E27.15.4.0", {"start": v(-285.75, 35.15) * mm, "end": v(-301.63, 28.38) * mm});
            skLineSegment(sketch, "E27.15.4.1", {"start": v(-269.88, 28.38) * mm, "end": v(-285.75, 35.15) * mm});
            skLineSegment(sketch, "E27.15.4.2", {"start": v(-285.75, 21.62) * mm, "end": v(-269.88, 28.38) * mm});
            skLineSegment(sketch, "E27.15.4.3", {"start": v(-301.63, 28.38) * mm, "end": v(-285.75, 21.62) * mm});
            skLineSegment(sketch, "E27.15.5.0", {"start": v(-285.75, 54.07) * mm, "end": v(-301.63, 47.3) * mm});
            skLineSegment(sketch, "E27.15.5.1", {"start": v(-269.88, 47.3) * mm, "end": v(-285.75, 54.07) * mm});
            skLineSegment(sketch, "E27.15.5.2", {"start": v(-285.75, 40.54) * mm, "end": v(-269.88, 47.3) * mm});
            skLineSegment(sketch, "E27.15.5.3", {"start": v(-301.63, 47.3) * mm, "end": v(-285.75, 40.54) * mm});
            skLineSegment(sketch, "E27.direction1", {"start": v(269.87, -47.3) * mm, "end": v(231.77, -47.3) * mm, "construction": true});
            skLineSegment(sketch, "E27.direction2", {"start": v(269.87, -47.3) * mm, "end": v(269.87, -28.38) * mm, "construction": true});
            skSolve(sketch);
        }
        {
            var Q0;
            Q0 = qSketchRegion(id + "F6", true);
            extrude(context, id + "F7", {"entities" : qUnion([Q0]), "operationType" : NewBodyOperationType.REMOVE, "oppositeDirection" : true, "depth" : 25.4 * mm});
        }
        {
            var Q0;
            Q0=makeQuery(id+"F1.opExtrude","SWEPT_FACE",FACE,{"disambiguationData":[OSD([sQuery(id+"F0.wireOp",EDGE,"E13.MirrorCS")])]});
            var sketch = newSketch(context, id + "F8", { "sketchPlane" : qUnion([Q0])});
            skLineSegment(sketch, "E28", {"start": v(-334.65, 64.68) * mm, "end": v(334.65, -83.5) * mm, "construction": true});
            skLineSegment(sketch, "E29", {"start": v(334.65, 64.68) * mm, "end": v(0, -9.41) * mm, "construction": true});
            skLineSegment(sketch, "E30", {"start": v(0, -2.65) * mm, "end": v(-15.88, -9.41) * mm});
            skLineSegment(sketch, "E31", {"start": v(-15.88, -9.41) * mm, "end": v(0, -16.17) * mm});
            skLineSegment(sketch, "E32", {"start": v(0, -16.17) * mm, "end": v(15.88, -9.41) * mm});
            skLineSegment(sketch, "E33", {"start": v(15.88, -9.41) * mm, "end": v(0, -2.65) * mm});
            skLineSegment(sketch, "E34.0.1.0", {"start": v(15.88, 9.51) * mm, "end": v(0, 16.27) * mm});
            skLineSegment(sketch, "E34.0.1.1", {"start": v(-15.88, 9.51) * mm, "end": v(0, 2.75) * mm});
            skLineSegment(sketch, "E34.0.1.2", {"start": v(0, 16.27) * mm, "end": v(-15.88, 9.51) * mm});
            skLineSegment(sketch, "E34.0.1.3", {"start": v(0, 2.75) * mm, "end": v(15.88, 9.51) * mm});
            skLineSegment(sketch, "E34.0.2.0", {"start": v(15.88, 28.43) * mm, "end": v(0, 35.2) * mm});
            skLineSegment(sketch, "E34.0.2.1", {"start": v(-15.88, 28.43) * mm, "end": v(0, 21.67) * mm});
            skLineSegment(sketch, "E34.0.2.2", {"start": v(0, 35.2) * mm, "end": v(-15.88, 28.43) * mm});
            skLineSegment(sketch, "E34.0.2.3", {"start": v(0, 21.67) * mm, "end": v(15.88, 28.43) * mm});
            skLineSegment(sketch, "E34.0.3.0", {"start": v(15.88, 47.36) * mm, "end": v(0, 54.12) * mm});
            skLineSegment(sketch, "E34.0.3.1", {"start": v(-15.88, 47.36) * mm, "end": v(0, 40.6) * mm});
            skLineSegment(sketch, "E34.0.3.2", {"start": v(0, 54.12) * mm, "end": v(-15.88, 47.36) * mm});
            skLineSegment(sketch, "E34.0.3.3", {"start": v(0, 40.6) * mm, "end": v(15.88, 47.36) * mm});
            skLineSegment(sketch, "E34.1.0.0", {"start": v(53.98, -9.41) * mm, "end": v(38.1, -2.65) * mm});
            skLineSegment(sketch, "E34.1.0.1", {"start": v(22.22, -9.41) * mm, "end": v(38.1, -16.17) * mm});
            skLineSegment(sketch, "E34.1.0.2", {"start": v(38.1, -2.65) * mm, "end": v(22.23, -9.41) * mm});
            skLineSegment(sketch, "E34.1.0.3", {"start": v(38.1, -16.17) * mm, "end": v(53.98, -9.41) * mm});
            skLineSegment(sketch, "E34.1.1.0", {"start": v(53.98, 9.51) * mm, "end": v(38.1, 16.27) * mm});
            skLineSegment(sketch, "E34.1.1.1", {"start": v(22.22, 9.51) * mm, "end": v(38.1, 2.75) * mm});
            skLineSegment(sketch, "E34.1.1.2", {"start": v(38.1, 16.27) * mm, "end": v(22.23, 9.51) * mm});
            skLineSegment(sketch, "E34.1.1.3", {"start": v(38.1, 2.75) * mm, "end": v(53.98, 9.51) * mm});
            skLineSegment(sketch, "E34.1.2.0", {"start": v(53.98, 28.43) * mm, "end": v(38.1, 35.2) * mm});
            skLineSegment(sketch, "E34.1.2.1", {"start": v(22.22, 28.43) * mm, "end": v(38.1, 21.67) * mm});
            skLineSegment(sketch, "E34.1.2.2", {"start": v(38.1, 35.2) * mm, "end": v(22.23, 28.43) * mm});
            skLineSegment(sketch, "E34.1.2.3", {"start": v(38.1, 21.67) * mm, "end": v(53.98, 28.43) * mm});
            skLineSegment(sketch, "E34.1.3.0", {"start": v(53.98, 47.36) * mm, "end": v(38.1, 54.12) * mm});
            skLineSegment(sketch, "E34.1.3.1", {"start": v(22.22, 47.36) * mm, "end": v(38.1, 40.6) * mm});
            skLineSegment(sketch, "E34.1.3.2", {"start": v(38.1, 54.12) * mm, "end": v(22.23, 47.36) * mm});
            skLineSegment(sketch, "E34.1.3.3", {"start": v(38.1, 40.6) * mm, "end": v(53.98, 47.36) * mm});
            skLineSegment(sketch, "E34.2.0.0", {"start": v(92.08, -9.41) * mm, "end": v(76.2, -2.65) * mm});
            skLineSegment(sketch, "E34.2.0.1", {"start": v(60.33, -9.41) * mm, "end": v(76.2, -16.17) * mm});
            skLineSegment(sketch, "E34.2.0.2", {"start": v(76.2, -2.65) * mm, "end": v(60.33, -9.41) * mm});
            skLineSegment(sketch, "E34.2.0.3", {"start": v(76.2, -16.17) * mm, "end": v(92.08, -9.41) * mm});
            skLineSegment(sketch, "E34.2.1.0", {"start": v(92.08, 9.51) * mm, "end": v(76.2, 16.27) * mm});
            skLineSegment(sketch, "E34.2.1.1", {"start": v(60.33, 9.51) * mm, "end": v(76.2, 2.75) * mm});
            skLineSegment(sketch, "E34.2.1.2", {"start": v(76.2, 16.27) * mm, "end": v(60.33, 9.51) * mm});
            skLineSegment(sketch, "E34.2.1.3", {"start": v(76.2, 2.75) * mm, "end": v(92.08, 9.51) * mm});
            skLineSegment(sketch, "E34.2.2.0", {"start": v(92.08, 28.43) * mm, "end": v(76.2, 35.2) * mm});
            skLineSegment(sketch, "E34.2.2.1", {"start": v(60.33, 28.43) * mm, "end": v(76.2, 21.67) * mm});
            skLineSegment(sketch, "E34.2.2.2", {"start": v(76.2, 35.2) * mm, "end": v(60.33, 28.43) * mm});
            skLineSegment(sketch, "E34.2.2.3", {"start": v(76.2, 21.67) * mm, "end": v(92.08, 28.43) * mm});
            skLineSegment(sketch, "E34.2.3.0", {"start": v(92.08, 47.36) * mm, "end": v(76.2, 54.12) * mm});
            skLineSegment(sketch, "E34.2.3.1", {"start": v(60.33, 47.36) * mm, "end": v(76.2, 40.6) * mm});
            skLineSegment(sketch, "E34.2.3.2", {"start": v(76.2, 54.12) * mm, "end": v(60.33, 47.36) * mm});
            skLineSegment(sketch, "E34.2.3.3", {"start": v(76.2, 40.6) * mm, "end": v(92.08, 47.36) * mm});
            skLineSegment(sketch, "E34.3.0.0", {"start": v(130.18, -9.41) * mm, "end": v(114.3, -2.65) * mm});
            skLineSegment(sketch, "E34.3.0.1", {"start": v(98.43, -9.41) * mm, "end": v(114.3, -16.17) * mm});
            skLineSegment(sketch, "E34.3.0.2", {"start": v(114.3, -2.65) * mm, "end": v(98.43, -9.41) * mm});
            skLineSegment(sketch, "E34.3.0.3", {"start": v(114.3, -16.17) * mm, "end": v(130.18, -9.41) * mm});
            skLineSegment(sketch, "E34.3.1.0", {"start": v(130.18, 9.51) * mm, "end": v(114.3, 16.27) * mm});
            skLineSegment(sketch, "E34.3.1.1", {"start": v(98.43, 9.51) * mm, "end": v(114.3, 2.75) * mm});
            skLineSegment(sketch, "E34.3.1.2", {"start": v(114.3, 16.27) * mm, "end": v(98.43, 9.51) * mm});
            skLineSegment(sketch, "E34.3.1.3", {"start": v(114.3, 2.75) * mm, "end": v(130.18, 9.51) * mm});
            skLineSegment(sketch, "E34.3.2.0", {"start": v(130.18, 28.43) * mm, "end": v(114.3, 35.2) * mm});
            skLineSegment(sketch, "E34.3.2.1", {"start": v(98.43, 28.43) * mm, "end": v(114.3, 21.67) * mm});
            skLineSegment(sketch, "E34.3.2.2", {"start": v(114.3, 35.2) * mm, "end": v(98.43, 28.43) * mm});
            skLineSegment(sketch, "E34.3.2.3", {"start": v(114.3, 21.67) * mm, "end": v(130.18, 28.43) * mm});
            skLineSegment(sketch, "E34.3.3.0", {"start": v(130.18, 47.36) * mm, "end": v(114.3, 54.12) * mm});
            skLineSegment(sketch, "E34.3.3.1", {"start": v(98.43, 47.36) * mm, "end": v(114.3, 40.6) * mm});
            skLineSegment(sketch, "E34.3.3.2", {"start": v(114.3, 54.12) * mm, "end": v(98.43, 47.36) * mm});
            skLineSegment(sketch, "E34.3.3.3", {"start": v(114.3, 40.6) * mm, "end": v(130.18, 47.36) * mm});
            skLineSegment(sketch, "E34.4.0.0", {"start": v(168.28, -9.41) * mm, "end": v(152.4, -2.65) * mm});
            skLineSegment(sketch, "E34.4.0.1", {"start": v(136.52, -9.41) * mm, "end": v(152.4, -16.17) * mm});
            skLineSegment(sketch, "E34.4.0.2", {"start": v(152.4, -2.65) * mm, "end": v(136.53, -9.41) * mm});
            skLineSegment(sketch, "E34.4.0.3", {"start": v(152.4, -16.17) * mm, "end": v(168.28, -9.41) * mm});
            skLineSegment(sketch, "E34.4.1.0", {"start": v(168.28, 9.51) * mm, "end": v(152.4, 16.27) * mm});
            skLineSegment(sketch, "E34.4.1.1", {"start": v(136.52, 9.51) * mm, "end": v(152.4, 2.75) * mm});
            skLineSegment(sketch, "E34.4.1.2", {"start": v(152.4, 16.27) * mm, "end": v(136.53, 9.51) * mm});
            skLineSegment(sketch, "E34.4.1.3", {"start": v(152.4, 2.75) * mm, "end": v(168.28, 9.51) * mm});
            skLineSegment(sketch, "E34.4.2.0", {"start": v(168.28, 28.43) * mm, "end": v(152.4, 35.2) * mm});
            skLineSegment(sketch, "E34.4.2.1", {"start": v(136.52, 28.43) * mm, "end": v(152.4, 21.67) * mm});
            skLineSegment(sketch, "E34.4.2.2", {"start": v(152.4, 35.2) * mm, "end": v(136.53, 28.43) * mm});
            skLineSegment(sketch, "E34.4.2.3", {"start": v(152.4, 21.67) * mm, "end": v(168.28, 28.43) * mm});
            skLineSegment(sketch, "E34.4.3.0", {"start": v(168.28, 47.36) * mm, "end": v(152.4, 54.12) * mm});
            skLineSegment(sketch, "E34.4.3.1", {"start": v(136.52, 47.36) * mm, "end": v(152.4, 40.6) * mm});
            skLineSegment(sketch, "E34.4.3.2", {"start": v(152.4, 54.12) * mm, "end": v(136.53, 47.36) * mm});
            skLineSegment(sketch, "E34.4.3.3", {"start": v(152.4, 40.6) * mm, "end": v(168.28, 47.36) * mm});
            skLineSegment(sketch, "E34.5.0.0", {"start": v(206.38, -9.41) * mm, "end": v(190.5, -2.65) * mm});
            skLineSegment(sketch, "E34.5.0.1", {"start": v(174.62, -9.41) * mm, "end": v(190.5, -16.17) * mm});
            skLineSegment(sketch, "E34.5.0.2", {"start": v(190.5, -2.65) * mm, "end": v(174.62, -9.41) * mm});
            skLineSegment(sketch, "E34.5.0.3", {"start": v(190.5, -16.17) * mm, "end": v(206.38, -9.41) * mm});
            skLineSegment(sketch, "E34.5.1.0", {"start": v(206.38, 9.51) * mm, "end": v(190.5, 16.27) * mm});
            skLineSegment(sketch, "E34.5.1.1", {"start": v(174.62, 9.51) * mm, "end": v(190.5, 2.75) * mm});
            skLineSegment(sketch, "E34.5.1.2", {"start": v(190.5, 16.27) * mm, "end": v(174.62, 9.51) * mm});
            skLineSegment(sketch, "E34.5.1.3", {"start": v(190.5, 2.75) * mm, "end": v(206.38, 9.51) * mm});
            skLineSegment(sketch, "E34.5.2.0", {"start": v(206.38, 28.43) * mm, "end": v(190.5, 35.2) * mm});
            skLineSegment(sketch, "E34.5.2.1", {"start": v(174.62, 28.43) * mm, "end": v(190.5, 21.67) * mm});
            skLineSegment(sketch, "E34.5.2.2", {"start": v(190.5, 35.2) * mm, "end": v(174.62, 28.43) * mm});
            skLineSegment(sketch, "E34.5.2.3", {"start": v(190.5, 21.67) * mm, "end": v(206.38, 28.43) * mm});
            skLineSegment(sketch, "E34.5.3.0", {"start": v(206.38, 47.36) * mm, "end": v(190.5, 54.12) * mm});
            skLineSegment(sketch, "E34.5.3.1", {"start": v(174.62, 47.36) * mm, "end": v(190.5, 40.6) * mm});
            skLineSegment(sketch, "E34.5.3.2", {"start": v(190.5, 54.12) * mm, "end": v(174.62, 47.36) * mm});
            skLineSegment(sketch, "E34.5.3.3", {"start": v(190.5, 40.6) * mm, "end": v(206.38, 47.36) * mm});
            skLineSegment(sketch, "E34.6.0.0", {"start": v(244.48, -9.41) * mm, "end": v(228.6, -2.65) * mm});
            skLineSegment(sketch, "E34.6.0.1", {"start": v(212.72, -9.41) * mm, "end": v(228.6, -16.17) * mm});
            skLineSegment(sketch, "E34.6.0.2", {"start": v(228.6, -2.65) * mm, "end": v(212.73, -9.41) * mm});
            skLineSegment(sketch, "E34.6.0.3", {"start": v(228.6, -16.17) * mm, "end": v(244.48, -9.41) * mm});
            skLineSegment(sketch, "E34.6.1.0", {"start": v(244.48, 9.51) * mm, "end": v(228.6, 16.27) * mm});
            skLineSegment(sketch, "E34.6.1.1", {"start": v(212.72, 9.51) * mm, "end": v(228.6, 2.75) * mm});
            skLineSegment(sketch, "E34.6.1.2", {"start": v(228.6, 16.27) * mm, "end": v(212.73, 9.51) * mm});
            skLineSegment(sketch, "E34.6.1.3", {"start": v(228.6, 2.75) * mm, "end": v(244.48, 9.51) * mm});
            skLineSegment(sketch, "E34.6.2.0", {"start": v(244.48, 28.43) * mm, "end": v(228.6, 35.2) * mm});
            skLineSegment(sketch, "E34.6.2.1", {"start": v(212.72, 28.43) * mm, "end": v(228.6, 21.67) * mm});
            skLineSegment(sketch, "E34.6.2.2", {"start": v(228.6, 35.2) * mm, "end": v(212.73, 28.43) * mm});
            skLineSegment(sketch, "E34.6.2.3", {"start": v(228.6, 21.67) * mm, "end": v(244.48, 28.43) * mm});
            skLineSegment(sketch, "E34.6.3.0", {"start": v(244.48, 47.36) * mm, "end": v(228.6, 54.12) * mm});
            skLineSegment(sketch, "E34.6.3.1", {"start": v(212.72, 47.36) * mm, "end": v(228.6, 40.6) * mm});
            skLineSegment(sketch, "E34.6.3.2", {"start": v(228.6, 54.12) * mm, "end": v(212.73, 47.36) * mm});
            skLineSegment(sketch, "E34.6.3.3", {"start": v(228.6, 40.6) * mm, "end": v(244.48, 47.36) * mm});
            skLineSegment(sketch, "E34.7.0.0", {"start": v(282.58, -9.41) * mm, "end": v(266.7, -2.65) * mm});
            skLineSegment(sketch, "E34.7.0.1", {"start": v(250.82, -9.41) * mm, "end": v(266.7, -16.17) * mm});
            skLineSegment(sketch, "E34.7.0.2", {"start": v(266.7, -2.65) * mm, "end": v(250.83, -9.41) * mm});
            skLineSegment(sketch, "E34.7.0.3", {"start": v(266.7, -16.17) * mm, "end": v(282.58, -9.41) * mm});
            skLineSegment(sketch, "E34.7.1.0", {"start": v(282.58, 9.51) * mm, "end": v(266.7, 16.27) * mm});
            skLineSegment(sketch, "E34.7.1.1", {"start": v(250.82, 9.51) * mm, "end": v(266.7, 2.75) * mm});
            skLineSegment(sketch, "E34.7.1.2", {"start": v(266.7, 16.27) * mm, "end": v(250.83, 9.51) * mm});
            skLineSegment(sketch, "E34.7.1.3", {"start": v(266.7, 2.75) * mm, "end": v(282.58, 9.51) * mm});
            skLineSegment(sketch, "E34.7.2.0", {"start": v(282.58, 28.43) * mm, "end": v(266.7, 35.2) * mm});
            skLineSegment(sketch, "E34.7.2.1", {"start": v(250.82, 28.43) * mm, "end": v(266.7, 21.67) * mm});
            skLineSegment(sketch, "E34.7.2.2", {"start": v(266.7, 35.2) * mm, "end": v(250.83, 28.43) * mm});
            skLineSegment(sketch, "E34.7.2.3", {"start": v(266.7, 21.67) * mm, "end": v(282.58, 28.43) * mm});
            skLineSegment(sketch, "E34.7.3.0", {"start": v(282.58, 47.36) * mm, "end": v(266.7, 54.12) * mm});
            skLineSegment(sketch, "E34.7.3.1", {"start": v(250.82, 47.36) * mm, "end": v(266.7, 40.6) * mm});
            skLineSegment(sketch, "E34.7.3.2", {"start": v(266.7, 54.12) * mm, "end": v(250.83, 47.36) * mm});
            skLineSegment(sketch, "E34.7.3.3", {"start": v(266.7, 40.6) * mm, "end": v(282.58, 47.36) * mm});
            skLineSegment(sketch, "E34.8.0.0", {"start": v(320.68, -9.41) * mm, "end": v(304.8, -2.65) * mm});
            skLineSegment(sketch, "E34.8.0.1", {"start": v(288.93, -9.41) * mm, "end": v(304.8, -16.17) * mm});
            skLineSegment(sketch, "E34.8.0.2", {"start": v(304.8, -2.65) * mm, "end": v(288.93, -9.41) * mm});
            skLineSegment(sketch, "E34.8.0.3", {"start": v(304.8, -16.17) * mm, "end": v(320.68, -9.41) * mm});
            skLineSegment(sketch, "E34.8.1.0", {"start": v(320.68, 9.51) * mm, "end": v(304.8, 16.27) * mm});
            skLineSegment(sketch, "E34.8.1.1", {"start": v(288.93, 9.51) * mm, "end": v(304.8, 2.75) * mm});
            skLineSegment(sketch, "E34.8.1.2", {"start": v(304.8, 16.27) * mm, "end": v(288.93, 9.51) * mm});
            skLineSegment(sketch, "E34.8.1.3", {"start": v(304.8, 2.75) * mm, "end": v(320.68, 9.51) * mm});
            skLineSegment(sketch, "E34.8.2.0", {"start": v(320.68, 28.43) * mm, "end": v(304.8, 35.2) * mm});
            skLineSegment(sketch, "E34.8.2.1", {"start": v(288.93, 28.43) * mm, "end": v(304.8, 21.67) * mm});
            skLineSegment(sketch, "E34.8.2.2", {"start": v(304.8, 35.2) * mm, "end": v(288.93, 28.43) * mm});
            skLineSegment(sketch, "E34.8.2.3", {"start": v(304.8, 21.67) * mm, "end": v(320.68, 28.43) * mm});
            skLineSegment(sketch, "E34.8.3.0", {"start": v(320.68, 47.36) * mm, "end": v(304.8, 54.12) * mm});
            skLineSegment(sketch, "E34.8.3.1", {"start": v(288.93, 47.36) * mm, "end": v(304.8, 40.6) * mm});
            skLineSegment(sketch, "E34.8.3.2", {"start": v(304.8, 54.12) * mm, "end": v(288.93, 47.36) * mm});
            skLineSegment(sketch, "E34.8.3.3", {"start": v(304.8, 40.6) * mm, "end": v(320.68, 47.36) * mm});
            skLineSegment(sketch, "E34.direction1", {"start": v(-15.88, -9.41) * mm, "end": v(22.22, -9.41) * mm, "construction": true});
            skLineSegment(sketch, "E34.direction2", {"start": v(-15.88, -9.41) * mm, "end": v(-15.88, 9.51) * mm, "construction": true});
            skLineSegment(sketch, "E35.0.1.0", {"start": v(0, -21.57) * mm, "end": v(-15.88, -28.33) * mm});
            skLineSegment(sketch, "E35.0.1.1", {"start": v(-15.88, -28.33) * mm, "end": v(0, -35.1) * mm});
            skLineSegment(sketch, "E35.0.1.2", {"start": v(0, -35.1) * mm, "end": v(15.88, -28.33) * mm});
            skLineSegment(sketch, "E35.0.1.3", {"start": v(15.88, -28.33) * mm, "end": v(0, -21.57) * mm});
            skLineSegment(sketch, "E35.0.1.4", {"start": v(168.28, -28.33) * mm, "end": v(152.4, -21.57) * mm});
            skLineSegment(sketch, "E35.0.1.5", {"start": v(130.18, -28.33) * mm, "end": v(114.3, -21.57) * mm});
            skLineSegment(sketch, "E35.0.1.6", {"start": v(92.08, -28.33) * mm, "end": v(76.2, -21.57) * mm});
            skLineSegment(sketch, "E35.0.1.7", {"start": v(53.98, -28.33) * mm, "end": v(38.1, -21.57) * mm});
            skLineSegment(sketch, "E35.0.1.8", {"start": v(320.68, -28.33) * mm, "end": v(304.8, -21.57) * mm});
            skLineSegment(sketch, "E35.0.1.9", {"start": v(282.58, -28.33) * mm, "end": v(266.7, -21.57) * mm});
            skLineSegment(sketch, "E35.0.1.10", {"start": v(244.48, -28.33) * mm, "end": v(228.6, -21.57) * mm});
            skLineSegment(sketch, "E35.0.1.11", {"start": v(206.38, -28.33) * mm, "end": v(190.5, -21.57) * mm});
            skLineSegment(sketch, "E35.0.1.12", {"start": v(288.93, -28.33) * mm, "end": v(304.8, -35.1) * mm});
            skLineSegment(sketch, "E35.0.1.13", {"start": v(250.82, -28.33) * mm, "end": v(266.7, -35.1) * mm});
            skLineSegment(sketch, "E35.0.1.14", {"start": v(212.72, -28.33) * mm, "end": v(228.6, -35.1) * mm});
            skLineSegment(sketch, "E35.0.1.15", {"start": v(174.62, -28.33) * mm, "end": v(190.5, -35.1) * mm});
            skLineSegment(sketch, "E35.0.1.16", {"start": v(136.52, -28.33) * mm, "end": v(152.4, -35.1) * mm});
            skLineSegment(sketch, "E35.0.1.17", {"start": v(98.43, -28.33) * mm, "end": v(114.3, -35.1) * mm});
            skLineSegment(sketch, "E35.0.1.18", {"start": v(60.33, -28.33) * mm, "end": v(76.2, -35.1) * mm});
            skLineSegment(sketch, "E35.0.1.19", {"start": v(22.22, -28.33) * mm, "end": v(38.1, -35.1) * mm});
            skLineSegment(sketch, "E35.0.1.20", {"start": v(152.4, -21.57) * mm, "end": v(136.53, -28.33) * mm});
            skLineSegment(sketch, "E35.0.1.21", {"start": v(114.3, -21.57) * mm, "end": v(98.43, -28.33) * mm});
            skLineSegment(sketch, "E35.0.1.22", {"start": v(76.2, -21.57) * mm, "end": v(60.33, -28.33) * mm});
            skLineSegment(sketch, "E35.0.1.23", {"start": v(38.1, -21.57) * mm, "end": v(22.23, -28.33) * mm});
            skLineSegment(sketch, "E35.0.1.24", {"start": v(304.8, -21.57) * mm, "end": v(288.93, -28.33) * mm});
            skLineSegment(sketch, "E35.0.1.25", {"start": v(266.7, -21.57) * mm, "end": v(250.83, -28.33) * mm});
            skLineSegment(sketch, "E35.0.1.26", {"start": v(228.6, -21.57) * mm, "end": v(212.73, -28.33) * mm});
            skLineSegment(sketch, "E35.0.1.27", {"start": v(190.5, -21.57) * mm, "end": v(174.62, -28.33) * mm});
            skLineSegment(sketch, "E35.0.1.28", {"start": v(152.4, -35.1) * mm, "end": v(168.28, -28.33) * mm});
            skLineSegment(sketch, "E35.0.1.29", {"start": v(114.3, -35.1) * mm, "end": v(130.18, -28.33) * mm});
            skLineSegment(sketch, "E35.0.1.30", {"start": v(76.2, -35.1) * mm, "end": v(92.08, -28.33) * mm});
            skLineSegment(sketch, "E35.0.1.31", {"start": v(38.1, -35.1) * mm, "end": v(53.98, -28.33) * mm});
            skLineSegment(sketch, "E35.0.1.32", {"start": v(304.8, -35.1) * mm, "end": v(320.68, -28.33) * mm});
            skLineSegment(sketch, "E35.0.1.33", {"start": v(266.7, -35.1) * mm, "end": v(282.58, -28.33) * mm});
            skLineSegment(sketch, "E35.0.1.34", {"start": v(228.6, -35.1) * mm, "end": v(244.48, -28.33) * mm});
            skLineSegment(sketch, "E35.0.1.35", {"start": v(190.5, -35.1) * mm, "end": v(206.38, -28.33) * mm});
            skLineSegment(sketch, "E35.0.2.0", {"start": v(0, -40.5) * mm, "end": v(-15.88, -47.26) * mm});
            skLineSegment(sketch, "E35.0.2.1", {"start": v(-15.88, -47.26) * mm, "end": v(0, -54.02) * mm});
            skLineSegment(sketch, "E35.0.2.2", {"start": v(0, -54.02) * mm, "end": v(15.88, -47.26) * mm});
            skLineSegment(sketch, "E35.0.2.3", {"start": v(15.88, -47.26) * mm, "end": v(0, -40.5) * mm});
            skLineSegment(sketch, "E35.0.2.4", {"start": v(168.28, -47.26) * mm, "end": v(152.4, -40.5) * mm});
            skLineSegment(sketch, "E35.0.2.5", {"start": v(130.18, -47.26) * mm, "end": v(114.3, -40.5) * mm});
            skLineSegment(sketch, "E35.0.2.6", {"start": v(92.08, -47.26) * mm, "end": v(76.2, -40.5) * mm});
            skLineSegment(sketch, "E35.0.2.7", {"start": v(53.98, -47.26) * mm, "end": v(38.1, -40.5) * mm});
            skLineSegment(sketch, "E35.0.2.8", {"start": v(320.68, -47.26) * mm, "end": v(304.8, -40.5) * mm});
            skLineSegment(sketch, "E35.0.2.9", {"start": v(282.58, -47.26) * mm, "end": v(266.7, -40.5) * mm});
            skLineSegment(sketch, "E35.0.2.10", {"start": v(244.48, -47.26) * mm, "end": v(228.6, -40.5) * mm});
            skLineSegment(sketch, "E35.0.2.11", {"start": v(206.38, -47.26) * mm, "end": v(190.5, -40.5) * mm});
            skLineSegment(sketch, "E35.0.2.12", {"start": v(288.93, -47.26) * mm, "end": v(304.8, -54.02) * mm});
            skLineSegment(sketch, "E35.0.2.13", {"start": v(250.82, -47.26) * mm, "end": v(266.7, -54.02) * mm});
            skLineSegment(sketch, "E35.0.2.14", {"start": v(212.72, -47.26) * mm, "end": v(228.6, -54.02) * mm});
            skLineSegment(sketch, "E35.0.2.15", {"start": v(174.62, -47.26) * mm, "end": v(190.5, -54.02) * mm});
            skLineSegment(sketch, "E35.0.2.16", {"start": v(136.52, -47.26) * mm, "end": v(152.4, -54.02) * mm});
            skLineSegment(sketch, "E35.0.2.17", {"start": v(98.43, -47.26) * mm, "end": v(114.3, -54.02) * mm});
            skLineSegment(sketch, "E35.0.2.18", {"start": v(60.33, -47.26) * mm, "end": v(76.2, -54.02) * mm});
            skLineSegment(sketch, "E35.0.2.19", {"start": v(22.22, -47.26) * mm, "end": v(38.1, -54.02) * mm});
            skLineSegment(sketch, "E35.0.2.20", {"start": v(152.4, -40.5) * mm, "end": v(136.53, -47.26) * mm});
            skLineSegment(sketch, "E35.0.2.21", {"start": v(114.3, -40.5) * mm, "end": v(98.43, -47.26) * mm});
            skLineSegment(sketch, "E35.0.2.22", {"start": v(76.2, -40.5) * mm, "end": v(60.33, -47.26) * mm});
            skLineSegment(sketch, "E35.0.2.23", {"start": v(38.1, -40.5) * mm, "end": v(22.23, -47.26) * mm});
            skLineSegment(sketch, "E35.0.2.24", {"start": v(304.8, -40.5) * mm, "end": v(288.93, -47.26) * mm});
            skLineSegment(sketch, "E35.0.2.25", {"start": v(266.7, -40.5) * mm, "end": v(250.83, -47.26) * mm});
            skLineSegment(sketch, "E35.0.2.26", {"start": v(228.6, -40.5) * mm, "end": v(212.73, -47.26) * mm});
            skLineSegment(sketch, "E35.0.2.27", {"start": v(190.5, -40.5) * mm, "end": v(174.62, -47.26) * mm});
            skLineSegment(sketch, "E35.0.2.28", {"start": v(152.4, -54.02) * mm, "end": v(168.28, -47.26) * mm});
            skLineSegment(sketch, "E35.0.2.29", {"start": v(114.3, -54.02) * mm, "end": v(130.18, -47.26) * mm});
            skLineSegment(sketch, "E35.0.2.30", {"start": v(76.2, -54.02) * mm, "end": v(92.08, -47.26) * mm});
            skLineSegment(sketch, "E35.0.2.31", {"start": v(38.1, -54.02) * mm, "end": v(53.98, -47.26) * mm});
            skLineSegment(sketch, "E35.0.2.32", {"start": v(304.8, -54.02) * mm, "end": v(320.68, -47.26) * mm});
            skLineSegment(sketch, "E35.0.2.33", {"start": v(266.7, -54.02) * mm, "end": v(282.58, -47.26) * mm});
            skLineSegment(sketch, "E35.0.2.34", {"start": v(228.6, -54.02) * mm, "end": v(244.48, -47.26) * mm});
            skLineSegment(sketch, "E35.0.2.35", {"start": v(190.5, -54.02) * mm, "end": v(206.38, -47.26) * mm});
            skLineSegment(sketch, "E35.0.3.0", {"start": v(0, -59.42) * mm, "end": v(-15.88, -66.18) * mm});
            skLineSegment(sketch, "E35.0.3.1", {"start": v(-15.88, -66.18) * mm, "end": v(0, -72.94) * mm});
            skLineSegment(sketch, "E35.0.3.2", {"start": v(0, -72.94) * mm, "end": v(15.87, -66.18) * mm});
            skLineSegment(sketch, "E35.0.3.3", {"start": v(15.88, -66.18) * mm, "end": v(0, -59.42) * mm});
            skLineSegment(sketch, "E35.0.3.4", {"start": v(168.28, -66.18) * mm, "end": v(152.4, -59.42) * mm});
            skLineSegment(sketch, "E35.0.3.5", {"start": v(130.18, -66.18) * mm, "end": v(114.3, -59.42) * mm});
            skLineSegment(sketch, "E35.0.3.6", {"start": v(92.08, -66.18) * mm, "end": v(76.2, -59.42) * mm});
            skLineSegment(sketch, "E35.0.3.7", {"start": v(53.98, -66.18) * mm, "end": v(38.1, -59.42) * mm});
            skLineSegment(sketch, "E35.0.3.8", {"start": v(320.68, -66.18) * mm, "end": v(304.8, -59.42) * mm});
            skLineSegment(sketch, "E35.0.3.9", {"start": v(282.58, -66.18) * mm, "end": v(266.7, -59.42) * mm});
            skLineSegment(sketch, "E35.0.3.10", {"start": v(244.48, -66.18) * mm, "end": v(228.6, -59.42) * mm});
            skLineSegment(sketch, "E35.0.3.11", {"start": v(206.38, -66.18) * mm, "end": v(190.5, -59.42) * mm});
            skLineSegment(sketch, "E35.0.3.12", {"start": v(288.93, -66.18) * mm, "end": v(304.8, -72.94) * mm});
            skLineSegment(sketch, "E35.0.3.13", {"start": v(250.82, -66.18) * mm, "end": v(266.7, -72.94) * mm});
            skLineSegment(sketch, "E35.0.3.14", {"start": v(212.72, -66.18) * mm, "end": v(228.6, -72.94) * mm});
            skLineSegment(sketch, "E35.0.3.15", {"start": v(174.62, -66.18) * mm, "end": v(190.5, -72.94) * mm});
            skLineSegment(sketch, "E35.0.3.16", {"start": v(136.52, -66.18) * mm, "end": v(152.4, -72.94) * mm});
            skLineSegment(sketch, "E35.0.3.17", {"start": v(98.43, -66.18) * mm, "end": v(114.3, -72.94) * mm});
            skLineSegment(sketch, "E35.0.3.18", {"start": v(60.32, -66.18) * mm, "end": v(76.2, -72.94) * mm});
            skLineSegment(sketch, "E35.0.3.19", {"start": v(22.22, -66.18) * mm, "end": v(38.1, -72.94) * mm});
            skLineSegment(sketch, "E35.0.3.20", {"start": v(152.4, -59.42) * mm, "end": v(136.53, -66.18) * mm});
            skLineSegment(sketch, "E35.0.3.21", {"start": v(114.3, -59.42) * mm, "end": v(98.43, -66.18) * mm});
            skLineSegment(sketch, "E35.0.3.22", {"start": v(76.2, -59.42) * mm, "end": v(60.33, -66.18) * mm});
            skLineSegment(sketch, "E35.0.3.23", {"start": v(38.1, -59.42) * mm, "end": v(22.23, -66.18) * mm});
            skLineSegment(sketch, "E35.0.3.24", {"start": v(304.8, -59.42) * mm, "end": v(288.93, -66.18) * mm});
            skLineSegment(sketch, "E35.0.3.25", {"start": v(266.7, -59.42) * mm, "end": v(250.83, -66.18) * mm});
            skLineSegment(sketch, "E35.0.3.26", {"start": v(228.6, -59.42) * mm, "end": v(212.73, -66.18) * mm});
            skLineSegment(sketch, "E35.0.3.27", {"start": v(190.5, -59.42) * mm, "end": v(174.62, -66.18) * mm});
            skLineSegment(sketch, "E35.0.3.28", {"start": v(152.4, -72.94) * mm, "end": v(168.28, -66.18) * mm});
            skLineSegment(sketch, "E35.0.3.29", {"start": v(114.3, -72.94) * mm, "end": v(130.18, -66.18) * mm});
            skLineSegment(sketch, "E35.0.3.30", {"start": v(76.2, -72.94) * mm, "end": v(92.08, -66.18) * mm});
            skLineSegment(sketch, "E35.0.3.31", {"start": v(38.1, -72.94) * mm, "end": v(53.97, -66.18) * mm});
            skLineSegment(sketch, "E35.0.3.32", {"start": v(304.8, -72.94) * mm, "end": v(320.68, -66.18) * mm});
            skLineSegment(sketch, "E35.0.3.33", {"start": v(266.7, -72.94) * mm, "end": v(282.58, -66.18) * mm});
            skLineSegment(sketch, "E35.0.3.34", {"start": v(228.6, -72.94) * mm, "end": v(244.48, -66.18) * mm});
            skLineSegment(sketch, "E35.0.3.35", {"start": v(190.5, -72.94) * mm, "end": v(206.38, -66.18) * mm});
            skLineSegment(sketch, "E35.direction1", {"start": v(-15.88, -9.41) * mm, "end": v(9.52, -9.41) * mm, "construction": true});
            skLineSegment(sketch, "E35.direction2", {"start": v(-15.88, -9.41) * mm, "end": v(-15.88, -28.33) * mm, "construction": true});
            skLineSegment(sketch, "E36.1.0.0", {"start": v(-38.1, 40.6) * mm, "end": v(-22.23, 47.36) * mm});
            skLineSegment(sketch, "E36.1.0.1", {"start": v(-38.1, 54.12) * mm, "end": v(-53.98, 47.36) * mm});
            skLineSegment(sketch, "E36.1.0.2", {"start": v(-22.22, -66.18) * mm, "end": v(-38.1, -59.42) * mm});
            skLineSegment(sketch, "E36.1.0.3", {"start": v(-38.1, -72.94) * mm, "end": v(-22.23, -66.18) * mm});
            skLineSegment(sketch, "E36.1.0.4", {"start": v(-53.98, -66.18) * mm, "end": v(-38.1, -72.94) * mm});
            skLineSegment(sketch, "E36.1.0.5", {"start": v(-38.1, 35.2) * mm, "end": v(-53.98, 28.43) * mm});
            skLineSegment(sketch, "E36.1.0.6", {"start": v(-53.98, 28.43) * mm, "end": v(-38.1, 21.67) * mm});
            skLineSegment(sketch, "E36.1.0.7", {"start": v(-22.22, 28.43) * mm, "end": v(-38.1, 35.2) * mm});
            skLineSegment(sketch, "E36.1.0.8", {"start": v(-38.1, 2.75) * mm, "end": v(-22.23, 9.51) * mm});
            skLineSegment(sketch, "E36.1.0.9", {"start": v(-38.1, -21.57) * mm, "end": v(-53.98, -28.33) * mm});
            skLineSegment(sketch, "E36.1.0.10", {"start": v(-38.1, 16.27) * mm, "end": v(-53.98, 9.51) * mm});
            skLineSegment(sketch, "E36.1.0.11", {"start": v(-53.98, 9.51) * mm, "end": v(-38.1, 2.75) * mm});
            skLineSegment(sketch, "E36.1.0.12", {"start": v(-22.22, 9.51) * mm, "end": v(-38.1, 16.27) * mm});
            skLineSegment(sketch, "E36.1.0.13", {"start": v(-22.22, -9.41) * mm, "end": v(-38.1, -2.65) * mm});
            skLineSegment(sketch, "E36.1.0.14", {"start": v(-38.1, -16.17) * mm, "end": v(-22.23, -9.41) * mm});
            skLineSegment(sketch, "E36.1.0.15", {"start": v(-53.98, -9.41) * mm, "end": v(-38.1, -16.17) * mm});
            skLineSegment(sketch, "E36.1.0.16", {"start": v(-38.1, -2.65) * mm, "end": v(-53.98, -9.41) * mm});
            skLineSegment(sketch, "E36.1.0.17", {"start": v(-53.98, 47.36) * mm, "end": v(-38.1, 40.6) * mm});
            skLineSegment(sketch, "E36.1.0.18", {"start": v(-22.22, 47.36) * mm, "end": v(-38.1, 54.12) * mm});
            skLineSegment(sketch, "E36.1.0.19", {"start": v(-38.1, 21.67) * mm, "end": v(-22.23, 28.43) * mm});
            skLineSegment(sketch, "E36.1.0.20", {"start": v(-53.98, -28.33) * mm, "end": v(-38.1, -35.1) * mm});
            skLineSegment(sketch, "E36.1.0.21", {"start": v(-38.1, -35.1) * mm, "end": v(-22.23, -28.33) * mm});
            skLineSegment(sketch, "E36.1.0.22", {"start": v(-22.22, -28.33) * mm, "end": v(-38.1, -21.57) * mm});
            skLineSegment(sketch, "E36.1.0.23", {"start": v(-38.1, -40.5) * mm, "end": v(-53.98, -47.26) * mm});
            skLineSegment(sketch, "E36.1.0.24", {"start": v(-53.98, -47.26) * mm, "end": v(-38.1, -54.02) * mm});
            skLineSegment(sketch, "E36.1.0.25", {"start": v(-38.1, -54.02) * mm, "end": v(-22.23, -47.26) * mm});
            skLineSegment(sketch, "E36.1.0.26", {"start": v(-22.22, -47.26) * mm, "end": v(-38.1, -40.5) * mm});
            skLineSegment(sketch, "E36.1.0.27", {"start": v(-38.1, -59.42) * mm, "end": v(-53.98, -66.18) * mm});
            skLineSegment(sketch, "E36.1.0.28", {"start": v(-53.98, -9.41) * mm, "end": v(-28.58, -9.41) * mm, "construction": true});
            skLineSegment(sketch, "E36.2.0.0", {"start": v(-76.2, 40.6) * mm, "end": v(-60.33, 47.36) * mm});
            skLineSegment(sketch, "E36.2.0.1", {"start": v(-76.2, 54.12) * mm, "end": v(-92.08, 47.36) * mm});
            skLineSegment(sketch, "E36.2.0.2", {"start": v(-60.33, -66.18) * mm, "end": v(-76.2, -59.42) * mm});
            skLineSegment(sketch, "E36.2.0.3", {"start": v(-76.2, -72.94) * mm, "end": v(-60.33, -66.18) * mm});
            skLineSegment(sketch, "E36.2.0.4", {"start": v(-92.08, -66.18) * mm, "end": v(-76.2, -72.94) * mm});
            skLineSegment(sketch, "E36.2.0.5", {"start": v(-76.2, 35.2) * mm, "end": v(-92.08, 28.43) * mm});
            skLineSegment(sketch, "E36.2.0.6", {"start": v(-92.08, 28.43) * mm, "end": v(-76.2, 21.67) * mm});
            skLineSegment(sketch, "E36.2.0.7", {"start": v(-60.33, 28.43) * mm, "end": v(-76.2, 35.2) * mm});
            skLineSegment(sketch, "E36.2.0.8", {"start": v(-76.2, 2.75) * mm, "end": v(-60.33, 9.51) * mm});
            skLineSegment(sketch, "E36.2.0.9", {"start": v(-76.2, -21.57) * mm, "end": v(-92.08, -28.33) * mm});
            skLineSegment(sketch, "E36.2.0.10", {"start": v(-76.2, 16.27) * mm, "end": v(-92.08, 9.51) * mm});
            skLineSegment(sketch, "E36.2.0.11", {"start": v(-92.08, 9.51) * mm, "end": v(-76.2, 2.75) * mm});
            skLineSegment(sketch, "E36.2.0.12", {"start": v(-60.33, 9.51) * mm, "end": v(-76.2, 16.27) * mm});
            skLineSegment(sketch, "E36.2.0.13", {"start": v(-60.33, -9.41) * mm, "end": v(-76.2, -2.65) * mm});
            skLineSegment(sketch, "E36.2.0.14", {"start": v(-76.2, -16.17) * mm, "end": v(-60.33, -9.41) * mm});
            skLineSegment(sketch, "E36.2.0.15", {"start": v(-92.08, -9.41) * mm, "end": v(-76.2, -16.17) * mm});
            skLineSegment(sketch, "E36.2.0.16", {"start": v(-76.2, -2.65) * mm, "end": v(-92.08, -9.41) * mm});
            skLineSegment(sketch, "E36.2.0.17", {"start": v(-92.08, 47.36) * mm, "end": v(-76.2, 40.6) * mm});
            skLineSegment(sketch, "E36.2.0.18", {"start": v(-60.33, 47.36) * mm, "end": v(-76.2, 54.12) * mm});
            skLineSegment(sketch, "E36.2.0.19", {"start": v(-76.2, 21.67) * mm, "end": v(-60.33, 28.43) * mm});
            skLineSegment(sketch, "E36.2.0.20", {"start": v(-92.08, -28.33) * mm, "end": v(-76.2, -35.1) * mm});
            skLineSegment(sketch, "E36.2.0.21", {"start": v(-76.2, -35.1) * mm, "end": v(-60.33, -28.33) * mm});
            skLineSegment(sketch, "E36.2.0.22", {"start": v(-60.33, -28.33) * mm, "end": v(-76.2, -21.57) * mm});
            skLineSegment(sketch, "E36.2.0.23", {"start": v(-76.2, -40.5) * mm, "end": v(-92.08, -47.26) * mm});
            skLineSegment(sketch, "E36.2.0.24", {"start": v(-92.08, -47.26) * mm, "end": v(-76.2, -54.02) * mm});
            skLineSegment(sketch, "E36.2.0.25", {"start": v(-76.2, -54.02) * mm, "end": v(-60.33, -47.26) * mm});
            skLineSegment(sketch, "E36.2.0.26", {"start": v(-60.33, -47.26) * mm, "end": v(-76.2, -40.5) * mm});
            skLineSegment(sketch, "E36.2.0.27", {"start": v(-76.2, -59.42) * mm, "end": v(-92.08, -66.18) * mm});
            skLineSegment(sketch, "E36.2.0.28", {"start": v(-92.08, -9.41) * mm, "end": v(-66.67, -9.41) * mm, "construction": true});
            skLineSegment(sketch, "E36.3.0.0", {"start": v(-114.3, 40.6) * mm, "end": v(-98.43, 47.36) * mm});
            skLineSegment(sketch, "E36.3.0.1", {"start": v(-114.3, 54.12) * mm, "end": v(-130.18, 47.36) * mm});
            skLineSegment(sketch, "E36.3.0.2", {"start": v(-98.43, -66.18) * mm, "end": v(-114.3, -59.42) * mm});
            skLineSegment(sketch, "E36.3.0.3", {"start": v(-114.3, -72.94) * mm, "end": v(-98.43, -66.18) * mm});
            skLineSegment(sketch, "E36.3.0.4", {"start": v(-130.18, -66.18) * mm, "end": v(-114.3, -72.94) * mm});
            skLineSegment(sketch, "E36.3.0.5", {"start": v(-114.3, 35.2) * mm, "end": v(-130.18, 28.43) * mm});
            skLineSegment(sketch, "E36.3.0.6", {"start": v(-130.18, 28.43) * mm, "end": v(-114.3, 21.67) * mm});
            skLineSegment(sketch, "E36.3.0.7", {"start": v(-98.43, 28.43) * mm, "end": v(-114.3, 35.2) * mm});
            skLineSegment(sketch, "E36.3.0.8", {"start": v(-114.3, 2.75) * mm, "end": v(-98.43, 9.51) * mm});
            skLineSegment(sketch, "E36.3.0.9", {"start": v(-114.3, -21.57) * mm, "end": v(-130.18, -28.33) * mm});
            skLineSegment(sketch, "E36.3.0.10", {"start": v(-114.3, 16.27) * mm, "end": v(-130.18, 9.51) * mm});
            skLineSegment(sketch, "E36.3.0.11", {"start": v(-130.18, 9.51) * mm, "end": v(-114.3, 2.75) * mm});
            skLineSegment(sketch, "E36.3.0.12", {"start": v(-98.43, 9.51) * mm, "end": v(-114.3, 16.27) * mm});
            skLineSegment(sketch, "E36.3.0.13", {"start": v(-98.43, -9.41) * mm, "end": v(-114.3, -2.65) * mm});
            skLineSegment(sketch, "E36.3.0.14", {"start": v(-114.3, -16.17) * mm, "end": v(-98.43, -9.41) * mm});
            skLineSegment(sketch, "E36.3.0.15", {"start": v(-130.18, -9.41) * mm, "end": v(-114.3, -16.17) * mm});
            skLineSegment(sketch, "E36.3.0.16", {"start": v(-114.3, -2.65) * mm, "end": v(-130.18, -9.41) * mm});
            skLineSegment(sketch, "E36.3.0.17", {"start": v(-130.18, 47.36) * mm, "end": v(-114.3, 40.6) * mm});
            skLineSegment(sketch, "E36.3.0.18", {"start": v(-98.43, 47.36) * mm, "end": v(-114.3, 54.12) * mm});
            skLineSegment(sketch, "E36.3.0.19", {"start": v(-114.3, 21.67) * mm, "end": v(-98.43, 28.43) * mm});
            skLineSegment(sketch, "E36.3.0.20", {"start": v(-130.18, -28.33) * mm, "end": v(-114.3, -35.1) * mm});
            skLineSegment(sketch, "E36.3.0.21", {"start": v(-114.3, -35.1) * mm, "end": v(-98.43, -28.33) * mm});
            skLineSegment(sketch, "E36.3.0.22", {"start": v(-98.43, -28.33) * mm, "end": v(-114.3, -21.57) * mm});
            skLineSegment(sketch, "E36.3.0.23", {"start": v(-114.3, -40.5) * mm, "end": v(-130.18, -47.26) * mm});
            skLineSegment(sketch, "E36.3.0.24", {"start": v(-130.18, -47.26) * mm, "end": v(-114.3, -54.02) * mm});
            skLineSegment(sketch, "E36.3.0.25", {"start": v(-114.3, -54.02) * mm, "end": v(-98.43, -47.26) * mm});
            skLineSegment(sketch, "E36.3.0.26", {"start": v(-98.43, -47.26) * mm, "end": v(-114.3, -40.5) * mm});
            skLineSegment(sketch, "E36.3.0.27", {"start": v(-114.3, -59.42) * mm, "end": v(-130.18, -66.18) * mm});
            skLineSegment(sketch, "E36.3.0.28", {"start": v(-130.18, -9.41) * mm, "end": v(-104.78, -9.41) * mm, "construction": true});
            skLineSegment(sketch, "E36.4.0.0", {"start": v(-152.4, 40.6) * mm, "end": v(-136.53, 47.36) * mm});
            skLineSegment(sketch, "E36.4.0.1", {"start": v(-152.4, 54.12) * mm, "end": v(-168.28, 47.36) * mm});
            skLineSegment(sketch, "E36.4.0.2", {"start": v(-136.53, -66.18) * mm, "end": v(-152.4, -59.42) * mm});
            skLineSegment(sketch, "E36.4.0.3", {"start": v(-152.4, -72.94) * mm, "end": v(-136.53, -66.18) * mm});
            skLineSegment(sketch, "E36.4.0.4", {"start": v(-168.28, -66.18) * mm, "end": v(-152.4, -72.94) * mm});
            skLineSegment(sketch, "E36.4.0.5", {"start": v(-152.4, 35.2) * mm, "end": v(-168.28, 28.43) * mm});
            skLineSegment(sketch, "E36.4.0.6", {"start": v(-168.28, 28.43) * mm, "end": v(-152.4, 21.67) * mm});
            skLineSegment(sketch, "E36.4.0.7", {"start": v(-136.53, 28.43) * mm, "end": v(-152.4, 35.2) * mm});
            skLineSegment(sketch, "E36.4.0.8", {"start": v(-152.4, 2.75) * mm, "end": v(-136.53, 9.51) * mm});
            skLineSegment(sketch, "E36.4.0.9", {"start": v(-152.4, -21.57) * mm, "end": v(-168.28, -28.33) * mm});
            skLineSegment(sketch, "E36.4.0.10", {"start": v(-152.4, 16.27) * mm, "end": v(-168.28, 9.51) * mm});
            skLineSegment(sketch, "E36.4.0.11", {"start": v(-168.28, 9.51) * mm, "end": v(-152.4, 2.75) * mm});
            skLineSegment(sketch, "E36.4.0.12", {"start": v(-136.53, 9.51) * mm, "end": v(-152.4, 16.27) * mm});
            skLineSegment(sketch, "E36.4.0.13", {"start": v(-136.53, -9.41) * mm, "end": v(-152.4, -2.65) * mm});
            skLineSegment(sketch, "E36.4.0.14", {"start": v(-152.4, -16.17) * mm, "end": v(-136.53, -9.41) * mm});
            skLineSegment(sketch, "E36.4.0.15", {"start": v(-168.28, -9.41) * mm, "end": v(-152.4, -16.17) * mm});
            skLineSegment(sketch, "E36.4.0.16", {"start": v(-152.4, -2.65) * mm, "end": v(-168.28, -9.41) * mm});
            skLineSegment(sketch, "E36.4.0.17", {"start": v(-168.28, 47.36) * mm, "end": v(-152.4, 40.6) * mm});
            skLineSegment(sketch, "E36.4.0.18", {"start": v(-136.53, 47.36) * mm, "end": v(-152.4, 54.12) * mm});
            skLineSegment(sketch, "E36.4.0.19", {"start": v(-152.4, 21.67) * mm, "end": v(-136.53, 28.43) * mm});
            skLineSegment(sketch, "E36.4.0.20", {"start": v(-168.28, -28.33) * mm, "end": v(-152.4, -35.1) * mm});
            skLineSegment(sketch, "E36.4.0.21", {"start": v(-152.4, -35.1) * mm, "end": v(-136.53, -28.33) * mm});
            skLineSegment(sketch, "E36.4.0.22", {"start": v(-136.53, -28.33) * mm, "end": v(-152.4, -21.57) * mm});
            skLineSegment(sketch, "E36.4.0.23", {"start": v(-152.4, -40.5) * mm, "end": v(-168.28, -47.26) * mm});
            skLineSegment(sketch, "E36.4.0.24", {"start": v(-168.28, -47.26) * mm, "end": v(-152.4, -54.02) * mm});
            skLineSegment(sketch, "E36.4.0.25", {"start": v(-152.4, -54.02) * mm, "end": v(-136.53, -47.26) * mm});
            skLineSegment(sketch, "E36.4.0.26", {"start": v(-136.53, -47.26) * mm, "end": v(-152.4, -40.5) * mm});
            skLineSegment(sketch, "E36.4.0.27", {"start": v(-152.4, -59.42) * mm, "end": v(-168.28, -66.18) * mm});
            skLineSegment(sketch, "E36.4.0.28", {"start": v(-168.28, -9.41) * mm, "end": v(-142.88, -9.41) * mm, "construction": true});
            skLineSegment(sketch, "E36.5.0.0", {"start": v(-190.5, 40.6) * mm, "end": v(-174.62, 47.36) * mm});
            skLineSegment(sketch, "E36.5.0.1", {"start": v(-190.5, 54.12) * mm, "end": v(-206.38, 47.36) * mm});
            skLineSegment(sketch, "E36.5.0.2", {"start": v(-174.62, -66.18) * mm, "end": v(-190.5, -59.42) * mm});
            skLineSegment(sketch, "E36.5.0.3", {"start": v(-190.5, -72.94) * mm, "end": v(-174.62, -66.18) * mm});
            skLineSegment(sketch, "E36.5.0.4", {"start": v(-206.38, -66.18) * mm, "end": v(-190.5, -72.94) * mm});
            skLineSegment(sketch, "E36.5.0.5", {"start": v(-190.5, 35.2) * mm, "end": v(-206.38, 28.43) * mm});
            skLineSegment(sketch, "E36.5.0.6", {"start": v(-206.38, 28.43) * mm, "end": v(-190.5, 21.67) * mm});
            skLineSegment(sketch, "E36.5.0.7", {"start": v(-174.62, 28.43) * mm, "end": v(-190.5, 35.2) * mm});
            skLineSegment(sketch, "E36.5.0.8", {"start": v(-190.5, 2.75) * mm, "end": v(-174.62, 9.51) * mm});
            skLineSegment(sketch, "E36.5.0.9", {"start": v(-190.5, -21.57) * mm, "end": v(-206.38, -28.33) * mm});
            skLineSegment(sketch, "E36.5.0.10", {"start": v(-190.5, 16.27) * mm, "end": v(-206.38, 9.51) * mm});
            skLineSegment(sketch, "E36.5.0.11", {"start": v(-206.38, 9.51) * mm, "end": v(-190.5, 2.75) * mm});
            skLineSegment(sketch, "E36.5.0.12", {"start": v(-174.62, 9.51) * mm, "end": v(-190.5, 16.27) * mm});
            skLineSegment(sketch, "E36.5.0.13", {"start": v(-174.62, -9.41) * mm, "end": v(-190.5, -2.65) * mm});
            skLineSegment(sketch, "E36.5.0.14", {"start": v(-190.5, -16.17) * mm, "end": v(-174.62, -9.41) * mm});
            skLineSegment(sketch, "E36.5.0.15", {"start": v(-206.38, -9.41) * mm, "end": v(-190.5, -16.17) * mm});
            skLineSegment(sketch, "E36.5.0.16", {"start": v(-190.5, -2.65) * mm, "end": v(-206.38, -9.41) * mm});
            skLineSegment(sketch, "E36.5.0.17", {"start": v(-206.38, 47.36) * mm, "end": v(-190.5, 40.6) * mm});
            skLineSegment(sketch, "E36.5.0.18", {"start": v(-174.62, 47.36) * mm, "end": v(-190.5, 54.12) * mm});
            skLineSegment(sketch, "E36.5.0.19", {"start": v(-190.5, 21.67) * mm, "end": v(-174.62, 28.43) * mm});
            skLineSegment(sketch, "E36.5.0.20", {"start": v(-206.38, -28.33) * mm, "end": v(-190.5, -35.1) * mm});
            skLineSegment(sketch, "E36.5.0.21", {"start": v(-190.5, -35.1) * mm, "end": v(-174.62, -28.33) * mm});
            skLineSegment(sketch, "E36.5.0.22", {"start": v(-174.62, -28.33) * mm, "end": v(-190.5, -21.57) * mm});
            skLineSegment(sketch, "E36.5.0.23", {"start": v(-190.5, -40.5) * mm, "end": v(-206.38, -47.26) * mm});
            skLineSegment(sketch, "E36.5.0.24", {"start": v(-206.38, -47.26) * mm, "end": v(-190.5, -54.02) * mm});
            skLineSegment(sketch, "E36.5.0.25", {"start": v(-190.5, -54.02) * mm, "end": v(-174.62, -47.26) * mm});
            skLineSegment(sketch, "E36.5.0.26", {"start": v(-174.62, -47.26) * mm, "end": v(-190.5, -40.5) * mm});
            skLineSegment(sketch, "E36.5.0.27", {"start": v(-190.5, -59.42) * mm, "end": v(-206.38, -66.18) * mm});
            skLineSegment(sketch, "E36.5.0.28", {"start": v(-206.38, -9.41) * mm, "end": v(-180.98, -9.41) * mm, "construction": true});
            skLineSegment(sketch, "E36.6.0.0", {"start": v(-228.6, 40.6) * mm, "end": v(-212.73, 47.36) * mm});
            skLineSegment(sketch, "E36.6.0.1", {"start": v(-228.6, 54.12) * mm, "end": v(-244.48, 47.36) * mm});
            skLineSegment(sketch, "E36.6.0.2", {"start": v(-212.73, -66.18) * mm, "end": v(-228.6, -59.42) * mm});
            skLineSegment(sketch, "E36.6.0.3", {"start": v(-228.6, -72.94) * mm, "end": v(-212.73, -66.18) * mm});
            skLineSegment(sketch, "E36.6.0.4", {"start": v(-244.48, -66.18) * mm, "end": v(-228.6, -72.94) * mm});
            skLineSegment(sketch, "E36.6.0.5", {"start": v(-228.6, 35.2) * mm, "end": v(-244.48, 28.43) * mm});
            skLineSegment(sketch, "E36.6.0.6", {"start": v(-244.48, 28.43) * mm, "end": v(-228.6, 21.67) * mm});
            skLineSegment(sketch, "E36.6.0.7", {"start": v(-212.73, 28.43) * mm, "end": v(-228.6, 35.2) * mm});
            skLineSegment(sketch, "E36.6.0.8", {"start": v(-228.6, 2.75) * mm, "end": v(-212.73, 9.51) * mm});
            skLineSegment(sketch, "E36.6.0.9", {"start": v(-228.6, -21.57) * mm, "end": v(-244.48, -28.33) * mm});
            skLineSegment(sketch, "E36.6.0.10", {"start": v(-228.6, 16.27) * mm, "end": v(-244.48, 9.51) * mm});
            skLineSegment(sketch, "E36.6.0.11", {"start": v(-244.48, 9.51) * mm, "end": v(-228.6, 2.75) * mm});
            skLineSegment(sketch, "E36.6.0.12", {"start": v(-212.73, 9.51) * mm, "end": v(-228.6, 16.27) * mm});
            skLineSegment(sketch, "E36.6.0.13", {"start": v(-212.73, -9.41) * mm, "end": v(-228.6, -2.65) * mm});
            skLineSegment(sketch, "E36.6.0.14", {"start": v(-228.6, -16.17) * mm, "end": v(-212.73, -9.41) * mm});
            skLineSegment(sketch, "E36.6.0.15", {"start": v(-244.48, -9.41) * mm, "end": v(-228.6, -16.17) * mm});
            skLineSegment(sketch, "E36.6.0.16", {"start": v(-228.6, -2.65) * mm, "end": v(-244.48, -9.41) * mm});
            skLineSegment(sketch, "E36.6.0.17", {"start": v(-244.48, 47.36) * mm, "end": v(-228.6, 40.6) * mm});
            skLineSegment(sketch, "E36.6.0.18", {"start": v(-212.73, 47.36) * mm, "end": v(-228.6, 54.12) * mm});
            skLineSegment(sketch, "E36.6.0.19", {"start": v(-228.6, 21.67) * mm, "end": v(-212.73, 28.43) * mm});
            skLineSegment(sketch, "E36.6.0.20", {"start": v(-244.48, -28.33) * mm, "end": v(-228.6, -35.1) * mm});
            skLineSegment(sketch, "E36.6.0.21", {"start": v(-228.6, -35.1) * mm, "end": v(-212.73, -28.33) * mm});
            skLineSegment(sketch, "E36.6.0.22", {"start": v(-212.73, -28.33) * mm, "end": v(-228.6, -21.57) * mm});
            skLineSegment(sketch, "E36.6.0.23", {"start": v(-228.6, -40.5) * mm, "end": v(-244.48, -47.26) * mm});
            skLineSegment(sketch, "E36.6.0.24", {"start": v(-244.48, -47.26) * mm, "end": v(-228.6, -54.02) * mm});
            skLineSegment(sketch, "E36.6.0.25", {"start": v(-228.6, -54.02) * mm, "end": v(-212.73, -47.26) * mm});
            skLineSegment(sketch, "E36.6.0.26", {"start": v(-212.73, -47.26) * mm, "end": v(-228.6, -40.5) * mm});
            skLineSegment(sketch, "E36.6.0.27", {"start": v(-228.6, -59.42) * mm, "end": v(-244.48, -66.18) * mm});
            skLineSegment(sketch, "E36.6.0.28", {"start": v(-244.48, -9.41) * mm, "end": v(-219.08, -9.41) * mm, "construction": true});
            skLineSegment(sketch, "E36.7.0.0", {"start": v(-266.7, 40.6) * mm, "end": v(-250.82, 47.36) * mm});
            skLineSegment(sketch, "E36.7.0.1", {"start": v(-266.7, 54.12) * mm, "end": v(-282.57, 47.36) * mm});
            skLineSegment(sketch, "E36.7.0.2", {"start": v(-250.82, -66.18) * mm, "end": v(-266.7, -59.42) * mm});
            skLineSegment(sketch, "E36.7.0.3", {"start": v(-266.7, -72.94) * mm, "end": v(-250.82, -66.18) * mm});
            skLineSegment(sketch, "E36.7.0.4", {"start": v(-282.58, -66.18) * mm, "end": v(-266.7, -72.94) * mm});
            skLineSegment(sketch, "E36.7.0.5", {"start": v(-266.7, 35.2) * mm, "end": v(-282.57, 28.43) * mm});
            skLineSegment(sketch, "E36.7.0.6", {"start": v(-282.58, 28.43) * mm, "end": v(-266.7, 21.67) * mm});
            skLineSegment(sketch, "E36.7.0.7", {"start": v(-250.82, 28.43) * mm, "end": v(-266.7, 35.2) * mm});
            skLineSegment(sketch, "E36.7.0.8", {"start": v(-266.7, 2.75) * mm, "end": v(-250.82, 9.51) * mm});
            skLineSegment(sketch, "E36.7.0.9", {"start": v(-266.7, -21.57) * mm, "end": v(-282.57, -28.33) * mm});
            skLineSegment(sketch, "E36.7.0.10", {"start": v(-266.7, 16.27) * mm, "end": v(-282.57, 9.51) * mm});
            skLineSegment(sketch, "E36.7.0.11", {"start": v(-282.58, 9.51) * mm, "end": v(-266.7, 2.75) * mm});
            skLineSegment(sketch, "E36.7.0.12", {"start": v(-250.82, 9.51) * mm, "end": v(-266.7, 16.27) * mm});
            skLineSegment(sketch, "E36.7.0.13", {"start": v(-250.82, -9.41) * mm, "end": v(-266.7, -2.65) * mm});
            skLineSegment(sketch, "E36.7.0.14", {"start": v(-266.7, -16.17) * mm, "end": v(-250.82, -9.41) * mm});
            skLineSegment(sketch, "E36.7.0.15", {"start": v(-282.58, -9.41) * mm, "end": v(-266.7, -16.17) * mm});
            skLineSegment(sketch, "E36.7.0.16", {"start": v(-266.7, -2.65) * mm, "end": v(-282.57, -9.41) * mm});
            skLineSegment(sketch, "E36.7.0.17", {"start": v(-282.58, 47.36) * mm, "end": v(-266.7, 40.6) * mm});
            skLineSegment(sketch, "E36.7.0.18", {"start": v(-250.82, 47.36) * mm, "end": v(-266.7, 54.12) * mm});
            skLineSegment(sketch, "E36.7.0.19", {"start": v(-266.7, 21.67) * mm, "end": v(-250.82, 28.43) * mm});
            skLineSegment(sketch, "E36.7.0.20", {"start": v(-282.58, -28.33) * mm, "end": v(-266.7, -35.1) * mm});
            skLineSegment(sketch, "E36.7.0.21", {"start": v(-266.7, -35.1) * mm, "end": v(-250.82, -28.33) * mm});
            skLineSegment(sketch, "E36.7.0.22", {"start": v(-250.82, -28.33) * mm, "end": v(-266.7, -21.57) * mm});
            skLineSegment(sketch, "E36.7.0.23", {"start": v(-266.7, -40.5) * mm, "end": v(-282.57, -47.26) * mm});
            skLineSegment(sketch, "E36.7.0.24", {"start": v(-282.58, -47.26) * mm, "end": v(-266.7, -54.02) * mm});
            skLineSegment(sketch, "E36.7.0.25", {"start": v(-266.7, -54.02) * mm, "end": v(-250.82, -47.26) * mm});
            skLineSegment(sketch, "E36.7.0.26", {"start": v(-250.82, -47.26) * mm, "end": v(-266.7, -40.5) * mm});
            skLineSegment(sketch, "E36.7.0.27", {"start": v(-266.7, -59.42) * mm, "end": v(-282.57, -66.18) * mm});
            skLineSegment(sketch, "E36.7.0.28", {"start": v(-282.57, -9.41) * mm, "end": v(-257.18, -9.41) * mm, "construction": true});
            skLineSegment(sketch, "E36.8.0.0", {"start": v(-304.8, 40.6) * mm, "end": v(-288.93, 47.36) * mm});
            skLineSegment(sketch, "E36.8.0.1", {"start": v(-304.8, 54.12) * mm, "end": v(-320.68, 47.36) * mm});
            skLineSegment(sketch, "E36.8.0.2", {"start": v(-288.93, -66.18) * mm, "end": v(-304.8, -59.42) * mm});
            skLineSegment(sketch, "E36.8.0.3", {"start": v(-304.8, -72.94) * mm, "end": v(-288.93, -66.18) * mm});
            skLineSegment(sketch, "E36.8.0.4", {"start": v(-320.68, -66.18) * mm, "end": v(-304.8, -72.94) * mm});
            skLineSegment(sketch, "E36.8.0.5", {"start": v(-304.8, 35.2) * mm, "end": v(-320.68, 28.43) * mm});
            skLineSegment(sketch, "E36.8.0.6", {"start": v(-320.68, 28.43) * mm, "end": v(-304.8, 21.67) * mm});
            skLineSegment(sketch, "E36.8.0.7", {"start": v(-288.93, 28.43) * mm, "end": v(-304.8, 35.2) * mm});
            skLineSegment(sketch, "E36.8.0.8", {"start": v(-304.8, 2.75) * mm, "end": v(-288.93, 9.51) * mm});
            skLineSegment(sketch, "E36.8.0.9", {"start": v(-304.8, -21.57) * mm, "end": v(-320.68, -28.33) * mm});
            skLineSegment(sketch, "E36.8.0.10", {"start": v(-304.8, 16.27) * mm, "end": v(-320.68, 9.51) * mm});
            skLineSegment(sketch, "E36.8.0.11", {"start": v(-320.68, 9.51) * mm, "end": v(-304.8, 2.75) * mm});
            skLineSegment(sketch, "E36.8.0.12", {"start": v(-288.93, 9.51) * mm, "end": v(-304.8, 16.27) * mm});
            skLineSegment(sketch, "E36.8.0.13", {"start": v(-288.93, -9.41) * mm, "end": v(-304.8, -2.65) * mm});
            skLineSegment(sketch, "E36.8.0.14", {"start": v(-304.8, -16.17) * mm, "end": v(-288.93, -9.41) * mm});
            skLineSegment(sketch, "E36.8.0.15", {"start": v(-320.68, -9.41) * mm, "end": v(-304.8, -16.17) * mm});
            skLineSegment(sketch, "E36.8.0.16", {"start": v(-304.8, -2.65) * mm, "end": v(-320.68, -9.41) * mm});
            skLineSegment(sketch, "E36.8.0.17", {"start": v(-320.68, 47.36) * mm, "end": v(-304.8, 40.6) * mm});
            skLineSegment(sketch, "E36.8.0.18", {"start": v(-288.93, 47.36) * mm, "end": v(-304.8, 54.12) * mm});
            skLineSegment(sketch, "E36.8.0.19", {"start": v(-304.8, 21.67) * mm, "end": v(-288.93, 28.43) * mm});
            skLineSegment(sketch, "E36.8.0.20", {"start": v(-320.68, -28.33) * mm, "end": v(-304.8, -35.1) * mm});
            skLineSegment(sketch, "E36.8.0.21", {"start": v(-304.8, -35.1) * mm, "end": v(-288.93, -28.33) * mm});
            skLineSegment(sketch, "E36.8.0.22", {"start": v(-288.93, -28.33) * mm, "end": v(-304.8, -21.57) * mm});
            skLineSegment(sketch, "E36.8.0.23", {"start": v(-304.8, -40.5) * mm, "end": v(-320.68, -47.26) * mm});
            skLineSegment(sketch, "E36.8.0.24", {"start": v(-320.68, -47.26) * mm, "end": v(-304.8, -54.02) * mm});
            skLineSegment(sketch, "E36.8.0.25", {"start": v(-304.8, -54.02) * mm, "end": v(-288.93, -47.26) * mm});
            skLineSegment(sketch, "E36.8.0.26", {"start": v(-288.93, -47.26) * mm, "end": v(-304.8, -40.5) * mm});
            skLineSegment(sketch, "E36.8.0.27", {"start": v(-304.8, -59.42) * mm, "end": v(-320.68, -66.18) * mm});
            skLineSegment(sketch, "E36.8.0.28", {"start": v(-320.68, -9.41) * mm, "end": v(-295.28, -9.41) * mm, "construction": true});
            skLineSegment(sketch, "E36.direction1", {"start": v(-15.88, -66.18) * mm, "end": v(-53.98, -66.18) * mm, "construction": true});
            skLineSegment(sketch, "E37", {"start": v(269.87, -56.72) * mm, "end": v(285.75, -49.96) * mm});
            skLineSegment(sketch, "E38", {"start": v(285.75, -49.96) * mm, "end": v(301.62, -56.72) * mm});
            skLineSegment(sketch, "E39", {"start": v(301.62, -56.72) * mm, "end": v(285.75, -63.48) * mm});
            skLineSegment(sketch, "E40", {"start": v(285.75, -63.48) * mm, "end": v(269.87, -56.72) * mm});
            skLineSegment(sketch, "E41.0.1.0", {"start": v(285.75, -31.03) * mm, "end": v(301.62, -37.8) * mm});
            skLineSegment(sketch, "E41.0.1.1", {"start": v(269.87, -37.8) * mm, "end": v(285.75, -31.03) * mm});
            skLineSegment(sketch, "E41.0.1.2", {"start": v(301.62, -37.8) * mm, "end": v(285.75, -44.56) * mm});
            skLineSegment(sketch, "E41.0.1.3", {"start": v(285.75, -44.56) * mm, "end": v(269.87, -37.8) * mm});
            skLineSegment(sketch, "E41.0.2.0", {"start": v(285.75, -12.1) * mm, "end": v(301.62, -18.87) * mm});
            skLineSegment(sketch, "E41.0.2.1", {"start": v(269.87, -18.87) * mm, "end": v(285.75, -12.1) * mm});
            skLineSegment(sketch, "E41.0.2.2", {"start": v(301.62, -18.87) * mm, "end": v(285.75, -25.64) * mm});
            skLineSegment(sketch, "E41.0.2.3", {"start": v(285.75, -25.64) * mm, "end": v(269.87, -18.87) * mm});
            skLineSegment(sketch, "E41.0.3.0", {"start": v(285.75, 6.81) * mm, "end": v(301.62, 0.05) * mm});
            skLineSegment(sketch, "E41.0.3.1", {"start": v(269.87, 0.05) * mm, "end": v(285.75, 6.81) * mm});
            skLineSegment(sketch, "E41.0.3.2", {"start": v(301.62, 0.05) * mm, "end": v(285.75, -6.71) * mm});
            skLineSegment(sketch, "E41.0.3.3", {"start": v(285.75, -6.71) * mm, "end": v(269.87, 0.05) * mm});
            skLineSegment(sketch, "E41.0.4.0", {"start": v(285.75, 25.74) * mm, "end": v(301.62, 18.97) * mm});
            skLineSegment(sketch, "E41.0.4.1", {"start": v(269.87, 18.97) * mm, "end": v(285.75, 25.74) * mm});
            skLineSegment(sketch, "E41.0.4.2", {"start": v(301.62, 18.97) * mm, "end": v(285.75, 12.21) * mm});
            skLineSegment(sketch, "E41.0.4.3", {"start": v(285.75, 12.21) * mm, "end": v(269.87, 18.97) * mm});
            skLineSegment(sketch, "E41.0.5.0", {"start": v(285.75, 44.66) * mm, "end": v(301.62, 37.9) * mm});
            skLineSegment(sketch, "E41.0.5.1", {"start": v(269.87, 37.9) * mm, "end": v(285.75, 44.66) * mm});
            skLineSegment(sketch, "E41.0.5.2", {"start": v(301.62, 37.9) * mm, "end": v(285.75, 31.13) * mm});
            skLineSegment(sketch, "E41.0.5.3", {"start": v(285.75, 31.13) * mm, "end": v(269.87, 37.9) * mm});
            skLineSegment(sketch, "E41.1.0.0", {"start": v(247.65, -49.96) * mm, "end": v(263.52, -56.72) * mm});
            skLineSegment(sketch, "E41.1.0.1", {"start": v(231.77, -56.72) * mm, "end": v(247.65, -49.96) * mm});
            skLineSegment(sketch, "E41.1.0.2", {"start": v(263.52, -56.72) * mm, "end": v(247.65, -63.48) * mm});
            skLineSegment(sketch, "E41.1.0.3", {"start": v(247.65, -63.48) * mm, "end": v(231.77, -56.72) * mm});
            skLineSegment(sketch, "E41.1.1.0", {"start": v(247.65, -31.03) * mm, "end": v(263.52, -37.8) * mm});
            skLineSegment(sketch, "E41.1.1.1", {"start": v(231.77, -37.8) * mm, "end": v(247.65, -31.03) * mm});
            skLineSegment(sketch, "E41.1.1.2", {"start": v(263.52, -37.8) * mm, "end": v(247.65, -44.56) * mm});
            skLineSegment(sketch, "E41.1.1.3", {"start": v(247.65, -44.56) * mm, "end": v(231.77, -37.8) * mm});
            skLineSegment(sketch, "E41.1.2.0", {"start": v(247.65, -12.1) * mm, "end": v(263.52, -18.87) * mm});
            skLineSegment(sketch, "E41.1.2.1", {"start": v(231.77, -18.87) * mm, "end": v(247.65, -12.1) * mm});
            skLineSegment(sketch, "E41.1.2.2", {"start": v(263.52, -18.87) * mm, "end": v(247.65, -25.64) * mm});
            skLineSegment(sketch, "E41.1.2.3", {"start": v(247.65, -25.64) * mm, "end": v(231.77, -18.87) * mm});
            skLineSegment(sketch, "E41.1.3.0", {"start": v(247.65, 6.81) * mm, "end": v(263.52, 0.05) * mm});
            skLineSegment(sketch, "E41.1.3.1", {"start": v(231.77, 0.05) * mm, "end": v(247.65, 6.81) * mm});
            skLineSegment(sketch, "E41.1.3.2", {"start": v(263.52, 0.05) * mm, "end": v(247.65, -6.71) * mm});
            skLineSegment(sketch, "E41.1.3.3", {"start": v(247.65, -6.71) * mm, "end": v(231.77, 0.05) * mm});
            skLineSegment(sketch, "E41.1.4.0", {"start": v(247.65, 25.74) * mm, "end": v(263.52, 18.97) * mm});
            skLineSegment(sketch, "E41.1.4.1", {"start": v(231.77, 18.97) * mm, "end": v(247.65, 25.74) * mm});
            skLineSegment(sketch, "E41.1.4.2", {"start": v(263.52, 18.97) * mm, "end": v(247.65, 12.21) * mm});
            skLineSegment(sketch, "E41.1.4.3", {"start": v(247.65, 12.21) * mm, "end": v(231.77, 18.97) * mm});
            skLineSegment(sketch, "E41.1.5.0", {"start": v(247.65, 44.66) * mm, "end": v(263.52, 37.9) * mm});
            skLineSegment(sketch, "E41.1.5.1", {"start": v(231.77, 37.9) * mm, "end": v(247.65, 44.66) * mm});
            skLineSegment(sketch, "E41.1.5.2", {"start": v(263.52, 37.9) * mm, "end": v(247.65, 31.13) * mm});
            skLineSegment(sketch, "E41.1.5.3", {"start": v(247.65, 31.13) * mm, "end": v(231.77, 37.9) * mm});
            skLineSegment(sketch, "E41.2.0.0", {"start": v(209.55, -49.96) * mm, "end": v(225.42, -56.72) * mm});
            skLineSegment(sketch, "E41.2.0.1", {"start": v(193.67, -56.72) * mm, "end": v(209.55, -49.96) * mm});
            skLineSegment(sketch, "E41.2.0.2", {"start": v(225.42, -56.72) * mm, "end": v(209.55, -63.48) * mm});
            skLineSegment(sketch, "E41.2.0.3", {"start": v(209.55, -63.48) * mm, "end": v(193.67, -56.72) * mm});
            skLineSegment(sketch, "E41.2.1.0", {"start": v(209.55, -31.03) * mm, "end": v(225.42, -37.8) * mm});
            skLineSegment(sketch, "E41.2.1.1", {"start": v(193.67, -37.8) * mm, "end": v(209.55, -31.03) * mm});
            skLineSegment(sketch, "E41.2.1.2", {"start": v(225.42, -37.8) * mm, "end": v(209.55, -44.56) * mm});
            skLineSegment(sketch, "E41.2.1.3", {"start": v(209.55, -44.56) * mm, "end": v(193.67, -37.8) * mm});
            skLineSegment(sketch, "E41.2.2.0", {"start": v(209.55, -12.1) * mm, "end": v(225.42, -18.87) * mm});
            skLineSegment(sketch, "E41.2.2.1", {"start": v(193.67, -18.87) * mm, "end": v(209.55, -12.1) * mm});
            skLineSegment(sketch, "E41.2.2.2", {"start": v(225.42, -18.87) * mm, "end": v(209.55, -25.64) * mm});
            skLineSegment(sketch, "E41.2.2.3", {"start": v(209.55, -25.64) * mm, "end": v(193.67, -18.87) * mm});
            skLineSegment(sketch, "E41.2.3.0", {"start": v(209.55, 6.81) * mm, "end": v(225.42, 0.05) * mm});
            skLineSegment(sketch, "E41.2.3.1", {"start": v(193.67, 0.05) * mm, "end": v(209.55, 6.81) * mm});
            skLineSegment(sketch, "E41.2.3.2", {"start": v(225.42, 0.05) * mm, "end": v(209.55, -6.71) * mm});
            skLineSegment(sketch, "E41.2.3.3", {"start": v(209.55, -6.71) * mm, "end": v(193.67, 0.05) * mm});
            skLineSegment(sketch, "E41.2.4.0", {"start": v(209.55, 25.74) * mm, "end": v(225.42, 18.97) * mm});
            skLineSegment(sketch, "E41.2.4.1", {"start": v(193.67, 18.97) * mm, "end": v(209.55, 25.74) * mm});
            skLineSegment(sketch, "E41.2.4.2", {"start": v(225.42, 18.97) * mm, "end": v(209.55, 12.21) * mm});
            skLineSegment(sketch, "E41.2.4.3", {"start": v(209.55, 12.21) * mm, "end": v(193.67, 18.97) * mm});
            skLineSegment(sketch, "E41.2.5.0", {"start": v(209.55, 44.66) * mm, "end": v(225.42, 37.9) * mm});
            skLineSegment(sketch, "E41.2.5.1", {"start": v(193.67, 37.9) * mm, "end": v(209.55, 44.66) * mm});
            skLineSegment(sketch, "E41.2.5.2", {"start": v(225.42, 37.9) * mm, "end": v(209.55, 31.13) * mm});
            skLineSegment(sketch, "E41.2.5.3", {"start": v(209.55, 31.13) * mm, "end": v(193.67, 37.9) * mm});
            skLineSegment(sketch, "E41.3.0.0", {"start": v(171.45, -49.96) * mm, "end": v(187.32, -56.72) * mm});
            skLineSegment(sketch, "E41.3.0.1", {"start": v(155.57, -56.72) * mm, "end": v(171.45, -49.96) * mm});
            skLineSegment(sketch, "E41.3.0.2", {"start": v(187.32, -56.72) * mm, "end": v(171.45, -63.48) * mm});
            skLineSegment(sketch, "E41.3.0.3", {"start": v(171.45, -63.48) * mm, "end": v(155.57, -56.72) * mm});
            skLineSegment(sketch, "E41.3.1.0", {"start": v(171.45, -31.03) * mm, "end": v(187.32, -37.8) * mm});
            skLineSegment(sketch, "E41.3.1.1", {"start": v(155.57, -37.8) * mm, "end": v(171.45, -31.03) * mm});
            skLineSegment(sketch, "E41.3.1.2", {"start": v(187.32, -37.8) * mm, "end": v(171.45, -44.56) * mm});
            skLineSegment(sketch, "E41.3.1.3", {"start": v(171.45, -44.56) * mm, "end": v(155.57, -37.8) * mm});
            skLineSegment(sketch, "E41.3.2.0", {"start": v(171.45, -12.1) * mm, "end": v(187.32, -18.87) * mm});
            skLineSegment(sketch, "E41.3.2.1", {"start": v(155.57, -18.87) * mm, "end": v(171.45, -12.1) * mm});
            skLineSegment(sketch, "E41.3.2.2", {"start": v(187.32, -18.87) * mm, "end": v(171.45, -25.64) * mm});
            skLineSegment(sketch, "E41.3.2.3", {"start": v(171.45, -25.64) * mm, "end": v(155.57, -18.87) * mm});
            skLineSegment(sketch, "E41.3.3.0", {"start": v(171.45, 6.81) * mm, "end": v(187.32, 0.05) * mm});
            skLineSegment(sketch, "E41.3.3.1", {"start": v(155.57, 0.05) * mm, "end": v(171.45, 6.81) * mm});
            skLineSegment(sketch, "E41.3.3.2", {"start": v(187.32, 0.05) * mm, "end": v(171.45, -6.71) * mm});
            skLineSegment(sketch, "E41.3.3.3", {"start": v(171.45, -6.71) * mm, "end": v(155.57, 0.05) * mm});
            skLineSegment(sketch, "E41.3.4.0", {"start": v(171.45, 25.74) * mm, "end": v(187.32, 18.97) * mm});
            skLineSegment(sketch, "E41.3.4.1", {"start": v(155.57, 18.97) * mm, "end": v(171.45, 25.74) * mm});
            skLineSegment(sketch, "E41.3.4.2", {"start": v(187.32, 18.97) * mm, "end": v(171.45, 12.21) * mm});
            skLineSegment(sketch, "E41.3.4.3", {"start": v(171.45, 12.21) * mm, "end": v(155.57, 18.97) * mm});
            skLineSegment(sketch, "E41.3.5.0", {"start": v(171.45, 44.66) * mm, "end": v(187.32, 37.9) * mm});
            skLineSegment(sketch, "E41.3.5.1", {"start": v(155.57, 37.9) * mm, "end": v(171.45, 44.66) * mm});
            skLineSegment(sketch, "E41.3.5.2", {"start": v(187.32, 37.9) * mm, "end": v(171.45, 31.13) * mm});
            skLineSegment(sketch, "E41.3.5.3", {"start": v(171.45, 31.13) * mm, "end": v(155.57, 37.9) * mm});
            skLineSegment(sketch, "E41.4.0.0", {"start": v(133.35, -49.96) * mm, "end": v(149.22, -56.72) * mm});
            skLineSegment(sketch, "E41.4.0.1", {"start": v(117.47, -56.72) * mm, "end": v(133.35, -49.96) * mm});
            skLineSegment(sketch, "E41.4.0.2", {"start": v(149.22, -56.72) * mm, "end": v(133.35, -63.48) * mm});
            skLineSegment(sketch, "E41.4.0.3", {"start": v(133.35, -63.48) * mm, "end": v(117.47, -56.72) * mm});
            skLineSegment(sketch, "E41.4.1.0", {"start": v(133.35, -31.03) * mm, "end": v(149.22, -37.8) * mm});
            skLineSegment(sketch, "E41.4.1.1", {"start": v(117.47, -37.8) * mm, "end": v(133.35, -31.03) * mm});
            skLineSegment(sketch, "E41.4.1.2", {"start": v(149.22, -37.8) * mm, "end": v(133.35, -44.56) * mm});
            skLineSegment(sketch, "E41.4.1.3", {"start": v(133.35, -44.56) * mm, "end": v(117.47, -37.8) * mm});
            skLineSegment(sketch, "E41.4.2.0", {"start": v(133.35, -12.1) * mm, "end": v(149.22, -18.87) * mm});
            skLineSegment(sketch, "E41.4.2.1", {"start": v(117.47, -18.87) * mm, "end": v(133.35, -12.1) * mm});
            skLineSegment(sketch, "E41.4.2.2", {"start": v(149.22, -18.87) * mm, "end": v(133.35, -25.64) * mm});
            skLineSegment(sketch, "E41.4.2.3", {"start": v(133.35, -25.64) * mm, "end": v(117.47, -18.87) * mm});
            skLineSegment(sketch, "E41.4.3.0", {"start": v(133.35, 6.81) * mm, "end": v(149.22, 0.05) * mm});
            skLineSegment(sketch, "E41.4.3.1", {"start": v(117.47, 0.05) * mm, "end": v(133.35, 6.81) * mm});
            skLineSegment(sketch, "E41.4.3.2", {"start": v(149.22, 0.05) * mm, "end": v(133.35, -6.71) * mm});
            skLineSegment(sketch, "E41.4.3.3", {"start": v(133.35, -6.71) * mm, "end": v(117.47, 0.05) * mm});
            skLineSegment(sketch, "E41.4.4.0", {"start": v(133.35, 25.74) * mm, "end": v(149.22, 18.97) * mm});
            skLineSegment(sketch, "E41.4.4.1", {"start": v(117.47, 18.97) * mm, "end": v(133.35, 25.74) * mm});
            skLineSegment(sketch, "E41.4.4.2", {"start": v(149.22, 18.97) * mm, "end": v(133.35, 12.21) * mm});
            skLineSegment(sketch, "E41.4.4.3", {"start": v(133.35, 12.21) * mm, "end": v(117.47, 18.97) * mm});
            skLineSegment(sketch, "E41.4.5.0", {"start": v(133.35, 44.66) * mm, "end": v(149.22, 37.9) * mm});
            skLineSegment(sketch, "E41.4.5.1", {"start": v(117.47, 37.9) * mm, "end": v(133.35, 44.66) * mm});
            skLineSegment(sketch, "E41.4.5.2", {"start": v(149.22, 37.9) * mm, "end": v(133.35, 31.13) * mm});
            skLineSegment(sketch, "E41.4.5.3", {"start": v(133.35, 31.13) * mm, "end": v(117.47, 37.9) * mm});
            skLineSegment(sketch, "E41.5.0.0", {"start": v(95.25, -49.96) * mm, "end": v(111.12, -56.72) * mm});
            skLineSegment(sketch, "E41.5.0.1", {"start": v(79.37, -56.72) * mm, "end": v(95.25, -49.96) * mm});
            skLineSegment(sketch, "E41.5.0.2", {"start": v(111.12, -56.72) * mm, "end": v(95.25, -63.48) * mm});
            skLineSegment(sketch, "E41.5.0.3", {"start": v(95.25, -63.48) * mm, "end": v(79.37, -56.72) * mm});
            skLineSegment(sketch, "E41.5.1.0", {"start": v(95.25, -31.03) * mm, "end": v(111.12, -37.8) * mm});
            skLineSegment(sketch, "E41.5.1.1", {"start": v(79.37, -37.8) * mm, "end": v(95.25, -31.03) * mm});
            skLineSegment(sketch, "E41.5.1.2", {"start": v(111.12, -37.8) * mm, "end": v(95.25, -44.56) * mm});
            skLineSegment(sketch, "E41.5.1.3", {"start": v(95.25, -44.56) * mm, "end": v(79.37, -37.8) * mm});
            skLineSegment(sketch, "E41.5.2.0", {"start": v(95.25, -12.1) * mm, "end": v(111.12, -18.87) * mm});
            skLineSegment(sketch, "E41.5.2.1", {"start": v(79.37, -18.87) * mm, "end": v(95.25, -12.1) * mm});
            skLineSegment(sketch, "E41.5.2.2", {"start": v(111.12, -18.87) * mm, "end": v(95.25, -25.64) * mm});
            skLineSegment(sketch, "E41.5.2.3", {"start": v(95.25, -25.64) * mm, "end": v(79.37, -18.87) * mm});
            skLineSegment(sketch, "E41.5.3.0", {"start": v(95.25, 6.81) * mm, "end": v(111.12, 0.05) * mm});
            skLineSegment(sketch, "E41.5.3.1", {"start": v(79.37, 0.05) * mm, "end": v(95.25, 6.81) * mm});
            skLineSegment(sketch, "E41.5.3.2", {"start": v(111.12, 0.05) * mm, "end": v(95.25, -6.71) * mm});
            skLineSegment(sketch, "E41.5.3.3", {"start": v(95.25, -6.71) * mm, "end": v(79.37, 0.05) * mm});
            skLineSegment(sketch, "E41.5.4.0", {"start": v(95.25, 25.74) * mm, "end": v(111.12, 18.97) * mm});
            skLineSegment(sketch, "E41.5.4.1", {"start": v(79.37, 18.97) * mm, "end": v(95.25, 25.74) * mm});
            skLineSegment(sketch, "E41.5.4.2", {"start": v(111.12, 18.97) * mm, "end": v(95.25, 12.21) * mm});
            skLineSegment(sketch, "E41.5.4.3", {"start": v(95.25, 12.21) * mm, "end": v(79.37, 18.97) * mm});
            skLineSegment(sketch, "E41.5.5.0", {"start": v(95.25, 44.66) * mm, "end": v(111.12, 37.9) * mm});
            skLineSegment(sketch, "E41.5.5.1", {"start": v(79.37, 37.9) * mm, "end": v(95.25, 44.66) * mm});
            skLineSegment(sketch, "E41.5.5.2", {"start": v(111.12, 37.9) * mm, "end": v(95.25, 31.13) * mm});
            skLineSegment(sketch, "E41.5.5.3", {"start": v(95.25, 31.13) * mm, "end": v(79.37, 37.9) * mm});
            skLineSegment(sketch, "E41.6.0.0", {"start": v(57.15, -49.96) * mm, "end": v(73.02, -56.72) * mm});
            skLineSegment(sketch, "E41.6.0.1", {"start": v(41.27, -56.72) * mm, "end": v(57.15, -49.96) * mm});
            skLineSegment(sketch, "E41.6.0.2", {"start": v(73.02, -56.72) * mm, "end": v(57.15, -63.48) * mm});
            skLineSegment(sketch, "E41.6.0.3", {"start": v(57.15, -63.48) * mm, "end": v(41.27, -56.72) * mm});
            skLineSegment(sketch, "E41.6.1.0", {"start": v(57.15, -31.03) * mm, "end": v(73.02, -37.8) * mm});
            skLineSegment(sketch, "E41.6.1.1", {"start": v(41.27, -37.8) * mm, "end": v(57.15, -31.03) * mm});
            skLineSegment(sketch, "E41.6.1.2", {"start": v(73.02, -37.8) * mm, "end": v(57.15, -44.56) * mm});
            skLineSegment(sketch, "E41.6.1.3", {"start": v(57.15, -44.56) * mm, "end": v(41.27, -37.8) * mm});
            skLineSegment(sketch, "E41.6.2.0", {"start": v(57.15, -12.1) * mm, "end": v(73.02, -18.87) * mm});
            skLineSegment(sketch, "E41.6.2.1", {"start": v(41.27, -18.87) * mm, "end": v(57.15, -12.1) * mm});
            skLineSegment(sketch, "E41.6.2.2", {"start": v(73.02, -18.87) * mm, "end": v(57.15, -25.64) * mm});
            skLineSegment(sketch, "E41.6.2.3", {"start": v(57.15, -25.64) * mm, "end": v(41.27, -18.87) * mm});
            skLineSegment(sketch, "E41.6.3.0", {"start": v(57.15, 6.81) * mm, "end": v(73.02, 0.05) * mm});
            skLineSegment(sketch, "E41.6.3.1", {"start": v(41.27, 0.05) * mm, "end": v(57.15, 6.81) * mm});
            skLineSegment(sketch, "E41.6.3.2", {"start": v(73.02, 0.05) * mm, "end": v(57.15, -6.71) * mm});
            skLineSegment(sketch, "E41.6.3.3", {"start": v(57.15, -6.71) * mm, "end": v(41.27, 0.05) * mm});
            skLineSegment(sketch, "E41.6.4.0", {"start": v(57.15, 25.74) * mm, "end": v(73.02, 18.97) * mm});
            skLineSegment(sketch, "E41.6.4.1", {"start": v(41.27, 18.97) * mm, "end": v(57.15, 25.74) * mm});
            skLineSegment(sketch, "E41.6.4.2", {"start": v(73.02, 18.97) * mm, "end": v(57.15, 12.21) * mm});
            skLineSegment(sketch, "E41.6.4.3", {"start": v(57.15, 12.21) * mm, "end": v(41.27, 18.97) * mm});
            skLineSegment(sketch, "E41.6.5.0", {"start": v(57.15, 44.66) * mm, "end": v(73.02, 37.9) * mm});
            skLineSegment(sketch, "E41.6.5.1", {"start": v(41.27, 37.9) * mm, "end": v(57.15, 44.66) * mm});
            skLineSegment(sketch, "E41.6.5.2", {"start": v(73.02, 37.9) * mm, "end": v(57.15, 31.13) * mm});
            skLineSegment(sketch, "E41.6.5.3", {"start": v(57.15, 31.13) * mm, "end": v(41.27, 37.9) * mm});
            skLineSegment(sketch, "E41.7.0.0", {"start": v(19.05, -49.96) * mm, "end": v(34.92, -56.72) * mm});
            skLineSegment(sketch, "E41.7.0.1", {"start": v(3.17, -56.72) * mm, "end": v(19.05, -49.96) * mm});
            skLineSegment(sketch, "E41.7.0.2", {"start": v(34.92, -56.72) * mm, "end": v(19.05, -63.48) * mm});
            skLineSegment(sketch, "E41.7.0.3", {"start": v(19.05, -63.48) * mm, "end": v(3.17, -56.72) * mm});
            skLineSegment(sketch, "E41.7.1.0", {"start": v(19.05, -31.03) * mm, "end": v(34.92, -37.8) * mm});
            skLineSegment(sketch, "E41.7.1.1", {"start": v(3.17, -37.8) * mm, "end": v(19.05, -31.03) * mm});
            skLineSegment(sketch, "E41.7.1.2", {"start": v(34.92, -37.8) * mm, "end": v(19.05, -44.56) * mm});
            skLineSegment(sketch, "E41.7.1.3", {"start": v(19.05, -44.56) * mm, "end": v(3.17, -37.8) * mm});
            skLineSegment(sketch, "E41.7.2.0", {"start": v(19.05, -12.1) * mm, "end": v(34.92, -18.87) * mm});
            skLineSegment(sketch, "E41.7.2.1", {"start": v(3.17, -18.87) * mm, "end": v(19.05, -12.1) * mm});
            skLineSegment(sketch, "E41.7.2.2", {"start": v(34.92, -18.87) * mm, "end": v(19.05, -25.64) * mm});
            skLineSegment(sketch, "E41.7.2.3", {"start": v(19.05, -25.64) * mm, "end": v(3.17, -18.87) * mm});
            skLineSegment(sketch, "E41.7.3.0", {"start": v(19.05, 6.81) * mm, "end": v(34.92, 0.05) * mm});
            skLineSegment(sketch, "E41.7.3.1", {"start": v(3.17, 0.05) * mm, "end": v(19.05, 6.81) * mm});
            skLineSegment(sketch, "E41.7.3.2", {"start": v(34.92, 0.05) * mm, "end": v(19.05, -6.71) * mm});
            skLineSegment(sketch, "E41.7.3.3", {"start": v(19.05, -6.71) * mm, "end": v(3.17, 0.05) * mm});
            skLineSegment(sketch, "E41.7.4.0", {"start": v(19.05, 25.74) * mm, "end": v(34.92, 18.97) * mm});
            skLineSegment(sketch, "E41.7.4.1", {"start": v(3.17, 18.97) * mm, "end": v(19.05, 25.74) * mm});
            skLineSegment(sketch, "E41.7.4.2", {"start": v(34.92, 18.97) * mm, "end": v(19.05, 12.21) * mm});
            skLineSegment(sketch, "E41.7.4.3", {"start": v(19.05, 12.21) * mm, "end": v(3.17, 18.97) * mm});
            skLineSegment(sketch, "E41.7.5.0", {"start": v(19.05, 44.66) * mm, "end": v(34.92, 37.9) * mm});
            skLineSegment(sketch, "E41.7.5.1", {"start": v(3.17, 37.9) * mm, "end": v(19.05, 44.66) * mm});
            skLineSegment(sketch, "E41.7.5.2", {"start": v(34.92, 37.9) * mm, "end": v(19.05, 31.13) * mm});
            skLineSegment(sketch, "E41.7.5.3", {"start": v(19.05, 31.13) * mm, "end": v(3.17, 37.9) * mm});
            skLineSegment(sketch, "E41.8.0.0", {"start": v(-19.05, -49.96) * mm, "end": v(-3.18, -56.72) * mm});
            skLineSegment(sketch, "E41.8.0.1", {"start": v(-34.93, -56.72) * mm, "end": v(-19.05, -49.96) * mm});
            skLineSegment(sketch, "E41.8.0.2", {"start": v(-3.18, -56.72) * mm, "end": v(-19.05, -63.48) * mm});
            skLineSegment(sketch, "E41.8.0.3", {"start": v(-19.05, -63.48) * mm, "end": v(-34.93, -56.72) * mm});
            skLineSegment(sketch, "E41.8.1.0", {"start": v(-19.05, -31.03) * mm, "end": v(-3.18, -37.8) * mm});
            skLineSegment(sketch, "E41.8.1.1", {"start": v(-34.93, -37.8) * mm, "end": v(-19.05, -31.03) * mm});
            skLineSegment(sketch, "E41.8.1.2", {"start": v(-3.18, -37.8) * mm, "end": v(-19.05, -44.56) * mm});
            skLineSegment(sketch, "E41.8.1.3", {"start": v(-19.05, -44.56) * mm, "end": v(-34.93, -37.8) * mm});
            skLineSegment(sketch, "E41.8.2.0", {"start": v(-19.05, -12.1) * mm, "end": v(-3.18, -18.87) * mm});
            skLineSegment(sketch, "E41.8.2.1", {"start": v(-34.93, -18.87) * mm, "end": v(-19.05, -12.1) * mm});
            skLineSegment(sketch, "E41.8.2.2", {"start": v(-3.18, -18.87) * mm, "end": v(-19.05, -25.64) * mm});
            skLineSegment(sketch, "E41.8.2.3", {"start": v(-19.05, -25.64) * mm, "end": v(-34.93, -18.87) * mm});
            skLineSegment(sketch, "E41.8.3.0", {"start": v(-19.05, 6.81) * mm, "end": v(-3.18, 0.05) * mm});
            skLineSegment(sketch, "E41.8.3.1", {"start": v(-34.93, 0.05) * mm, "end": v(-19.05, 6.81) * mm});
            skLineSegment(sketch, "E41.8.3.2", {"start": v(-3.18, 0.05) * mm, "end": v(-19.05, -6.71) * mm});
            skLineSegment(sketch, "E41.8.3.3", {"start": v(-19.05, -6.71) * mm, "end": v(-34.93, 0.05) * mm});
            skLineSegment(sketch, "E41.8.4.0", {"start": v(-19.05, 25.74) * mm, "end": v(-3.18, 18.97) * mm});
            skLineSegment(sketch, "E41.8.4.1", {"start": v(-34.93, 18.97) * mm, "end": v(-19.05, 25.74) * mm});
            skLineSegment(sketch, "E41.8.4.2", {"start": v(-3.18, 18.97) * mm, "end": v(-19.05, 12.21) * mm});
            skLineSegment(sketch, "E41.8.4.3", {"start": v(-19.05, 12.21) * mm, "end": v(-34.93, 18.97) * mm});
            skLineSegment(sketch, "E41.8.5.0", {"start": v(-19.05, 44.66) * mm, "end": v(-3.18, 37.9) * mm});
            skLineSegment(sketch, "E41.8.5.1", {"start": v(-34.93, 37.9) * mm, "end": v(-19.05, 44.66) * mm});
            skLineSegment(sketch, "E41.8.5.2", {"start": v(-3.18, 37.9) * mm, "end": v(-19.05, 31.13) * mm});
            skLineSegment(sketch, "E41.8.5.3", {"start": v(-19.05, 31.13) * mm, "end": v(-34.93, 37.9) * mm});
            skLineSegment(sketch, "E41.9.0.0", {"start": v(-57.15, -49.96) * mm, "end": v(-41.28, -56.72) * mm});
            skLineSegment(sketch, "E41.9.0.1", {"start": v(-73.03, -56.72) * mm, "end": v(-57.15, -49.96) * mm});
            skLineSegment(sketch, "E41.9.0.2", {"start": v(-41.28, -56.72) * mm, "end": v(-57.15, -63.48) * mm});
            skLineSegment(sketch, "E41.9.0.3", {"start": v(-57.15, -63.48) * mm, "end": v(-73.03, -56.72) * mm});
            skLineSegment(sketch, "E41.9.1.0", {"start": v(-57.15, -31.03) * mm, "end": v(-41.28, -37.8) * mm});
            skLineSegment(sketch, "E41.9.1.1", {"start": v(-73.03, -37.8) * mm, "end": v(-57.15, -31.03) * mm});
            skLineSegment(sketch, "E41.9.1.2", {"start": v(-41.28, -37.8) * mm, "end": v(-57.15, -44.56) * mm});
            skLineSegment(sketch, "E41.9.1.3", {"start": v(-57.15, -44.56) * mm, "end": v(-73.03, -37.8) * mm});
            skLineSegment(sketch, "E41.9.2.0", {"start": v(-57.15, -12.1) * mm, "end": v(-41.28, -18.87) * mm});
            skLineSegment(sketch, "E41.9.2.1", {"start": v(-73.03, -18.87) * mm, "end": v(-57.15, -12.1) * mm});
            skLineSegment(sketch, "E41.9.2.2", {"start": v(-41.28, -18.87) * mm, "end": v(-57.15, -25.64) * mm});
            skLineSegment(sketch, "E41.9.2.3", {"start": v(-57.15, -25.64) * mm, "end": v(-73.03, -18.87) * mm});
            skLineSegment(sketch, "E41.9.3.0", {"start": v(-57.15, 6.81) * mm, "end": v(-41.28, 0.05) * mm});
            skLineSegment(sketch, "E41.9.3.1", {"start": v(-73.03, 0.05) * mm, "end": v(-57.15, 6.81) * mm});
            skLineSegment(sketch, "E41.9.3.2", {"start": v(-41.28, 0.05) * mm, "end": v(-57.15, -6.71) * mm});
            skLineSegment(sketch, "E41.9.3.3", {"start": v(-57.15, -6.71) * mm, "end": v(-73.03, 0.05) * mm});
            skLineSegment(sketch, "E41.9.4.0", {"start": v(-57.15, 25.74) * mm, "end": v(-41.28, 18.97) * mm});
            skLineSegment(sketch, "E41.9.4.1", {"start": v(-73.03, 18.97) * mm, "end": v(-57.15, 25.74) * mm});
            skLineSegment(sketch, "E41.9.4.2", {"start": v(-41.28, 18.97) * mm, "end": v(-57.15, 12.21) * mm});
            skLineSegment(sketch, "E41.9.4.3", {"start": v(-57.15, 12.21) * mm, "end": v(-73.03, 18.97) * mm});
            skLineSegment(sketch, "E41.9.5.0", {"start": v(-57.15, 44.66) * mm, "end": v(-41.28, 37.9) * mm});
            skLineSegment(sketch, "E41.9.5.1", {"start": v(-73.03, 37.9) * mm, "end": v(-57.15, 44.66) * mm});
            skLineSegment(sketch, "E41.9.5.2", {"start": v(-41.28, 37.9) * mm, "end": v(-57.15, 31.13) * mm});
            skLineSegment(sketch, "E41.9.5.3", {"start": v(-57.15, 31.13) * mm, "end": v(-73.03, 37.9) * mm});
            skLineSegment(sketch, "E41.10.0.0", {"start": v(-95.25, -49.96) * mm, "end": v(-79.38, -56.72) * mm});
            skLineSegment(sketch, "E41.10.0.1", {"start": v(-111.13, -56.72) * mm, "end": v(-95.25, -49.96) * mm});
            skLineSegment(sketch, "E41.10.0.2", {"start": v(-79.38, -56.72) * mm, "end": v(-95.25, -63.48) * mm});
            skLineSegment(sketch, "E41.10.0.3", {"start": v(-95.25, -63.48) * mm, "end": v(-111.13, -56.72) * mm});
            skLineSegment(sketch, "E41.10.1.0", {"start": v(-95.25, -31.03) * mm, "end": v(-79.38, -37.8) * mm});
            skLineSegment(sketch, "E41.10.1.1", {"start": v(-111.13, -37.8) * mm, "end": v(-95.25, -31.03) * mm});
            skLineSegment(sketch, "E41.10.1.2", {"start": v(-79.38, -37.8) * mm, "end": v(-95.25, -44.56) * mm});
            skLineSegment(sketch, "E41.10.1.3", {"start": v(-95.25, -44.56) * mm, "end": v(-111.13, -37.8) * mm});
            skLineSegment(sketch, "E41.10.2.0", {"start": v(-95.25, -12.1) * mm, "end": v(-79.38, -18.87) * mm});
            skLineSegment(sketch, "E41.10.2.1", {"start": v(-111.13, -18.87) * mm, "end": v(-95.25, -12.1) * mm});
            skLineSegment(sketch, "E41.10.2.2", {"start": v(-79.38, -18.87) * mm, "end": v(-95.25, -25.64) * mm});
            skLineSegment(sketch, "E41.10.2.3", {"start": v(-95.25, -25.64) * mm, "end": v(-111.13, -18.87) * mm});
            skLineSegment(sketch, "E41.10.3.0", {"start": v(-95.25, 6.81) * mm, "end": v(-79.38, 0.05) * mm});
            skLineSegment(sketch, "E41.10.3.1", {"start": v(-111.13, 0.05) * mm, "end": v(-95.25, 6.81) * mm});
            skLineSegment(sketch, "E41.10.3.2", {"start": v(-79.38, 0.05) * mm, "end": v(-95.25, -6.71) * mm});
            skLineSegment(sketch, "E41.10.3.3", {"start": v(-95.25, -6.71) * mm, "end": v(-111.13, 0.05) * mm});
            skLineSegment(sketch, "E41.10.4.0", {"start": v(-95.25, 25.74) * mm, "end": v(-79.38, 18.97) * mm});
            skLineSegment(sketch, "E41.10.4.1", {"start": v(-111.13, 18.97) * mm, "end": v(-95.25, 25.74) * mm});
            skLineSegment(sketch, "E41.10.4.2", {"start": v(-79.38, 18.97) * mm, "end": v(-95.25, 12.21) * mm});
            skLineSegment(sketch, "E41.10.4.3", {"start": v(-95.25, 12.21) * mm, "end": v(-111.13, 18.97) * mm});
            skLineSegment(sketch, "E41.10.5.0", {"start": v(-95.25, 44.66) * mm, "end": v(-79.38, 37.9) * mm});
            skLineSegment(sketch, "E41.10.5.1", {"start": v(-111.13, 37.9) * mm, "end": v(-95.25, 44.66) * mm});
            skLineSegment(sketch, "E41.10.5.2", {"start": v(-79.38, 37.9) * mm, "end": v(-95.25, 31.13) * mm});
            skLineSegment(sketch, "E41.10.5.3", {"start": v(-95.25, 31.13) * mm, "end": v(-111.13, 37.9) * mm});
            skLineSegment(sketch, "E41.11.0.0", {"start": v(-133.35, -49.96) * mm, "end": v(-117.48, -56.72) * mm});
            skLineSegment(sketch, "E41.11.0.1", {"start": v(-149.23, -56.72) * mm, "end": v(-133.35, -49.96) * mm});
            skLineSegment(sketch, "E41.11.0.2", {"start": v(-117.48, -56.72) * mm, "end": v(-133.35, -63.48) * mm});
            skLineSegment(sketch, "E41.11.0.3", {"start": v(-133.35, -63.48) * mm, "end": v(-149.23, -56.72) * mm});
            skLineSegment(sketch, "E41.11.1.0", {"start": v(-133.35, -31.03) * mm, "end": v(-117.48, -37.8) * mm});
            skLineSegment(sketch, "E41.11.1.1", {"start": v(-149.23, -37.8) * mm, "end": v(-133.35, -31.03) * mm});
            skLineSegment(sketch, "E41.11.1.2", {"start": v(-117.48, -37.8) * mm, "end": v(-133.35, -44.56) * mm});
            skLineSegment(sketch, "E41.11.1.3", {"start": v(-133.35, -44.56) * mm, "end": v(-149.23, -37.8) * mm});
            skLineSegment(sketch, "E41.11.2.0", {"start": v(-133.35, -12.1) * mm, "end": v(-117.48, -18.87) * mm});
            skLineSegment(sketch, "E41.11.2.1", {"start": v(-149.23, -18.87) * mm, "end": v(-133.35, -12.1) * mm});
            skLineSegment(sketch, "E41.11.2.2", {"start": v(-117.48, -18.87) * mm, "end": v(-133.35, -25.64) * mm});
            skLineSegment(sketch, "E41.11.2.3", {"start": v(-133.35, -25.64) * mm, "end": v(-149.23, -18.87) * mm});
            skLineSegment(sketch, "E41.11.3.0", {"start": v(-133.35, 6.81) * mm, "end": v(-117.48, 0.05) * mm});
            skLineSegment(sketch, "E41.11.3.1", {"start": v(-149.23, 0.05) * mm, "end": v(-133.35, 6.81) * mm});
            skLineSegment(sketch, "E41.11.3.2", {"start": v(-117.48, 0.05) * mm, "end": v(-133.35, -6.71) * mm});
            skLineSegment(sketch, "E41.11.3.3", {"start": v(-133.35, -6.71) * mm, "end": v(-149.23, 0.05) * mm});
            skLineSegment(sketch, "E41.11.4.0", {"start": v(-133.35, 25.74) * mm, "end": v(-117.48, 18.97) * mm});
            skLineSegment(sketch, "E41.11.4.1", {"start": v(-149.23, 18.97) * mm, "end": v(-133.35, 25.74) * mm});
            skLineSegment(sketch, "E41.11.4.2", {"start": v(-117.48, 18.97) * mm, "end": v(-133.35, 12.21) * mm});
            skLineSegment(sketch, "E41.11.4.3", {"start": v(-133.35, 12.21) * mm, "end": v(-149.23, 18.97) * mm});
            skLineSegment(sketch, "E41.11.5.0", {"start": v(-133.35, 44.66) * mm, "end": v(-117.48, 37.9) * mm});
            skLineSegment(sketch, "E41.11.5.1", {"start": v(-149.23, 37.9) * mm, "end": v(-133.35, 44.66) * mm});
            skLineSegment(sketch, "E41.11.5.2", {"start": v(-117.48, 37.9) * mm, "end": v(-133.35, 31.13) * mm});
            skLineSegment(sketch, "E41.11.5.3", {"start": v(-133.35, 31.13) * mm, "end": v(-149.23, 37.9) * mm});
            skLineSegment(sketch, "E41.12.0.0", {"start": v(-171.45, -49.96) * mm, "end": v(-155.58, -56.72) * mm});
            skLineSegment(sketch, "E41.12.0.1", {"start": v(-187.33, -56.72) * mm, "end": v(-171.45, -49.96) * mm});
            skLineSegment(sketch, "E41.12.0.2", {"start": v(-155.58, -56.72) * mm, "end": v(-171.45, -63.48) * mm});
            skLineSegment(sketch, "E41.12.0.3", {"start": v(-171.45, -63.48) * mm, "end": v(-187.33, -56.72) * mm});
            skLineSegment(sketch, "E41.12.1.0", {"start": v(-171.45, -31.03) * mm, "end": v(-155.58, -37.8) * mm});
            skLineSegment(sketch, "E41.12.1.1", {"start": v(-187.33, -37.8) * mm, "end": v(-171.45, -31.03) * mm});
            skLineSegment(sketch, "E41.12.1.2", {"start": v(-155.58, -37.8) * mm, "end": v(-171.45, -44.56) * mm});
            skLineSegment(sketch, "E41.12.1.3", {"start": v(-171.45, -44.56) * mm, "end": v(-187.33, -37.8) * mm});
            skLineSegment(sketch, "E41.12.2.0", {"start": v(-171.45, -12.1) * mm, "end": v(-155.58, -18.87) * mm});
            skLineSegment(sketch, "E41.12.2.1", {"start": v(-187.33, -18.87) * mm, "end": v(-171.45, -12.1) * mm});
            skLineSegment(sketch, "E41.12.2.2", {"start": v(-155.58, -18.87) * mm, "end": v(-171.45, -25.64) * mm});
            skLineSegment(sketch, "E41.12.2.3", {"start": v(-171.45, -25.64) * mm, "end": v(-187.33, -18.87) * mm});
            skLineSegment(sketch, "E41.12.3.0", {"start": v(-171.45, 6.81) * mm, "end": v(-155.58, 0.05) * mm});
            skLineSegment(sketch, "E41.12.3.1", {"start": v(-187.33, 0.05) * mm, "end": v(-171.45, 6.81) * mm});
            skLineSegment(sketch, "E41.12.3.2", {"start": v(-155.58, 0.05) * mm, "end": v(-171.45, -6.71) * mm});
            skLineSegment(sketch, "E41.12.3.3", {"start": v(-171.45, -6.71) * mm, "end": v(-187.33, 0.05) * mm});
            skLineSegment(sketch, "E41.12.4.0", {"start": v(-171.45, 25.74) * mm, "end": v(-155.58, 18.97) * mm});
            skLineSegment(sketch, "E41.12.4.1", {"start": v(-187.33, 18.97) * mm, "end": v(-171.45, 25.74) * mm});
            skLineSegment(sketch, "E41.12.4.2", {"start": v(-155.58, 18.97) * mm, "end": v(-171.45, 12.21) * mm});
            skLineSegment(sketch, "E41.12.4.3", {"start": v(-171.45, 12.21) * mm, "end": v(-187.33, 18.97) * mm});
            skLineSegment(sketch, "E41.12.5.0", {"start": v(-171.45, 44.66) * mm, "end": v(-155.58, 37.9) * mm});
            skLineSegment(sketch, "E41.12.5.1", {"start": v(-187.33, 37.9) * mm, "end": v(-171.45, 44.66) * mm});
            skLineSegment(sketch, "E41.12.5.2", {"start": v(-155.58, 37.9) * mm, "end": v(-171.45, 31.13) * mm});
            skLineSegment(sketch, "E41.12.5.3", {"start": v(-171.45, 31.13) * mm, "end": v(-187.33, 37.9) * mm});
            skLineSegment(sketch, "E41.13.0.0", {"start": v(-209.55, -49.96) * mm, "end": v(-193.68, -56.72) * mm});
            skLineSegment(sketch, "E41.13.0.1", {"start": v(-225.43, -56.72) * mm, "end": v(-209.55, -49.96) * mm});
            skLineSegment(sketch, "E41.13.0.2", {"start": v(-193.68, -56.72) * mm, "end": v(-209.55, -63.48) * mm});
            skLineSegment(sketch, "E41.13.0.3", {"start": v(-209.55, -63.48) * mm, "end": v(-225.43, -56.72) * mm});
            skLineSegment(sketch, "E41.13.1.0", {"start": v(-209.55, -31.03) * mm, "end": v(-193.68, -37.8) * mm});
            skLineSegment(sketch, "E41.13.1.1", {"start": v(-225.43, -37.8) * mm, "end": v(-209.55, -31.03) * mm});
            skLineSegment(sketch, "E41.13.1.2", {"start": v(-193.68, -37.8) * mm, "end": v(-209.55, -44.56) * mm});
            skLineSegment(sketch, "E41.13.1.3", {"start": v(-209.55, -44.56) * mm, "end": v(-225.43, -37.8) * mm});
            skLineSegment(sketch, "E41.13.2.0", {"start": v(-209.55, -12.1) * mm, "end": v(-193.68, -18.87) * mm});
            skLineSegment(sketch, "E41.13.2.1", {"start": v(-225.43, -18.87) * mm, "end": v(-209.55, -12.1) * mm});
            skLineSegment(sketch, "E41.13.2.2", {"start": v(-193.68, -18.87) * mm, "end": v(-209.55, -25.64) * mm});
            skLineSegment(sketch, "E41.13.2.3", {"start": v(-209.55, -25.64) * mm, "end": v(-225.43, -18.87) * mm});
            skLineSegment(sketch, "E41.13.3.0", {"start": v(-209.55, 6.81) * mm, "end": v(-193.68, 0.05) * mm});
            skLineSegment(sketch, "E41.13.3.1", {"start": v(-225.43, 0.05) * mm, "end": v(-209.55, 6.81) * mm});
            skLineSegment(sketch, "E41.13.3.2", {"start": v(-193.68, 0.05) * mm, "end": v(-209.55, -6.71) * mm});
            skLineSegment(sketch, "E41.13.3.3", {"start": v(-209.55, -6.71) * mm, "end": v(-225.43, 0.05) * mm});
            skLineSegment(sketch, "E41.13.4.0", {"start": v(-209.55, 25.74) * mm, "end": v(-193.68, 18.97) * mm});
            skLineSegment(sketch, "E41.13.4.1", {"start": v(-225.43, 18.97) * mm, "end": v(-209.55, 25.74) * mm});
            skLineSegment(sketch, "E41.13.4.2", {"start": v(-193.68, 18.97) * mm, "end": v(-209.55, 12.21) * mm});
            skLineSegment(sketch, "E41.13.4.3", {"start": v(-209.55, 12.21) * mm, "end": v(-225.43, 18.97) * mm});
            skLineSegment(sketch, "E41.13.5.0", {"start": v(-209.55, 44.66) * mm, "end": v(-193.68, 37.9) * mm});
            skLineSegment(sketch, "E41.13.5.1", {"start": v(-225.43, 37.9) * mm, "end": v(-209.55, 44.66) * mm});
            skLineSegment(sketch, "E41.13.5.2", {"start": v(-193.68, 37.9) * mm, "end": v(-209.55, 31.13) * mm});
            skLineSegment(sketch, "E41.13.5.3", {"start": v(-209.55, 31.13) * mm, "end": v(-225.43, 37.9) * mm});
            skLineSegment(sketch, "E41.14.0.0", {"start": v(-247.65, -49.96) * mm, "end": v(-231.78, -56.72) * mm});
            skLineSegment(sketch, "E41.14.0.1", {"start": v(-263.53, -56.72) * mm, "end": v(-247.65, -49.96) * mm});
            skLineSegment(sketch, "E41.14.0.2", {"start": v(-231.78, -56.72) * mm, "end": v(-247.65, -63.48) * mm});
            skLineSegment(sketch, "E41.14.0.3", {"start": v(-247.65, -63.48) * mm, "end": v(-263.53, -56.72) * mm});
            skLineSegment(sketch, "E41.14.1.0", {"start": v(-247.65, -31.03) * mm, "end": v(-231.78, -37.8) * mm});
            skLineSegment(sketch, "E41.14.1.1", {"start": v(-263.53, -37.8) * mm, "end": v(-247.65, -31.03) * mm});
            skLineSegment(sketch, "E41.14.1.2", {"start": v(-231.78, -37.8) * mm, "end": v(-247.65, -44.56) * mm});
            skLineSegment(sketch, "E41.14.1.3", {"start": v(-247.65, -44.56) * mm, "end": v(-263.53, -37.8) * mm});
            skLineSegment(sketch, "E41.14.2.0", {"start": v(-247.65, -12.1) * mm, "end": v(-231.78, -18.87) * mm});
            skLineSegment(sketch, "E41.14.2.1", {"start": v(-263.53, -18.87) * mm, "end": v(-247.65, -12.1) * mm});
            skLineSegment(sketch, "E41.14.2.2", {"start": v(-231.78, -18.87) * mm, "end": v(-247.65, -25.64) * mm});
            skLineSegment(sketch, "E41.14.2.3", {"start": v(-247.65, -25.64) * mm, "end": v(-263.53, -18.87) * mm});
            skLineSegment(sketch, "E41.14.3.0", {"start": v(-247.65, 6.81) * mm, "end": v(-231.78, 0.05) * mm});
            skLineSegment(sketch, "E41.14.3.1", {"start": v(-263.53, 0.05) * mm, "end": v(-247.65, 6.81) * mm});
            skLineSegment(sketch, "E41.14.3.2", {"start": v(-231.78, 0.05) * mm, "end": v(-247.65, -6.71) * mm});
            skLineSegment(sketch, "E41.14.3.3", {"start": v(-247.65, -6.71) * mm, "end": v(-263.53, 0.05) * mm});
            skLineSegment(sketch, "E41.14.4.0", {"start": v(-247.65, 25.74) * mm, "end": v(-231.78, 18.97) * mm});
            skLineSegment(sketch, "E41.14.4.1", {"start": v(-263.53, 18.97) * mm, "end": v(-247.65, 25.74) * mm});
            skLineSegment(sketch, "E41.14.4.2", {"start": v(-231.78, 18.97) * mm, "end": v(-247.65, 12.21) * mm});
            skLineSegment(sketch, "E41.14.4.3", {"start": v(-247.65, 12.21) * mm, "end": v(-263.53, 18.97) * mm});
            skLineSegment(sketch, "E41.14.5.0", {"start": v(-247.65, 44.66) * mm, "end": v(-231.78, 37.9) * mm});
            skLineSegment(sketch, "E41.14.5.1", {"start": v(-263.53, 37.9) * mm, "end": v(-247.65, 44.66) * mm});
            skLineSegment(sketch, "E41.14.5.2", {"start": v(-231.78, 37.9) * mm, "end": v(-247.65, 31.13) * mm});
            skLineSegment(sketch, "E41.14.5.3", {"start": v(-247.65, 31.13) * mm, "end": v(-263.53, 37.9) * mm});
            skLineSegment(sketch, "E41.15.0.0", {"start": v(-285.75, -49.96) * mm, "end": v(-269.88, -56.72) * mm});
            skLineSegment(sketch, "E41.15.0.1", {"start": v(-301.63, -56.72) * mm, "end": v(-285.75, -49.96) * mm});
            skLineSegment(sketch, "E41.15.0.2", {"start": v(-269.88, -56.72) * mm, "end": v(-285.75, -63.48) * mm});
            skLineSegment(sketch, "E41.15.0.3", {"start": v(-285.75, -63.48) * mm, "end": v(-301.63, -56.72) * mm});
            skLineSegment(sketch, "E41.15.1.0", {"start": v(-285.75, -31.03) * mm, "end": v(-269.88, -37.8) * mm});
            skLineSegment(sketch, "E41.15.1.1", {"start": v(-301.63, -37.8) * mm, "end": v(-285.75, -31.03) * mm});
            skLineSegment(sketch, "E41.15.1.2", {"start": v(-269.88, -37.8) * mm, "end": v(-285.75, -44.56) * mm});
            skLineSegment(sketch, "E41.15.1.3", {"start": v(-285.75, -44.56) * mm, "end": v(-301.63, -37.8) * mm});
            skLineSegment(sketch, "E41.15.2.0", {"start": v(-285.75, -12.1) * mm, "end": v(-269.88, -18.87) * mm});
            skLineSegment(sketch, "E41.15.2.1", {"start": v(-301.63, -18.87) * mm, "end": v(-285.75, -12.1) * mm});
            skLineSegment(sketch, "E41.15.2.2", {"start": v(-269.88, -18.87) * mm, "end": v(-285.75, -25.64) * mm});
            skLineSegment(sketch, "E41.15.2.3", {"start": v(-285.75, -25.64) * mm, "end": v(-301.63, -18.87) * mm});
            skLineSegment(sketch, "E41.15.3.0", {"start": v(-285.75, 6.81) * mm, "end": v(-269.88, 0.05) * mm});
            skLineSegment(sketch, "E41.15.3.1", {"start": v(-301.63, 0.05) * mm, "end": v(-285.75, 6.81) * mm});
            skLineSegment(sketch, "E41.15.3.2", {"start": v(-269.88, 0.05) * mm, "end": v(-285.75, -6.71) * mm});
            skLineSegment(sketch, "E41.15.3.3", {"start": v(-285.75, -6.71) * mm, "end": v(-301.63, 0.05) * mm});
            skLineSegment(sketch, "E41.15.4.0", {"start": v(-285.75, 25.74) * mm, "end": v(-269.88, 18.97) * mm});
            skLineSegment(sketch, "E41.15.4.1", {"start": v(-301.63, 18.97) * mm, "end": v(-285.75, 25.74) * mm});
            skLineSegment(sketch, "E41.15.4.2", {"start": v(-269.88, 18.97) * mm, "end": v(-285.75, 12.21) * mm});
            skLineSegment(sketch, "E41.15.4.3", {"start": v(-285.75, 12.21) * mm, "end": v(-301.63, 18.97) * mm});
            skLineSegment(sketch, "E41.15.5.0", {"start": v(-285.75, 44.66) * mm, "end": v(-269.88, 37.9) * mm});
            skLineSegment(sketch, "E41.15.5.1", {"start": v(-301.63, 37.9) * mm, "end": v(-285.75, 44.66) * mm});
            skLineSegment(sketch, "E41.15.5.2", {"start": v(-269.88, 37.9) * mm, "end": v(-285.75, 31.13) * mm});
            skLineSegment(sketch, "E41.15.5.3", {"start": v(-285.75, 31.13) * mm, "end": v(-301.63, 37.9) * mm});
            skLineSegment(sketch, "E41.direction1", {"start": v(269.87, -56.72) * mm, "end": v(231.77, -56.72) * mm, "construction": true});
            skLineSegment(sketch, "E41.direction2", {"start": v(269.87, -56.72) * mm, "end": v(269.87, -37.8) * mm, "construction": true});
            skSolve(sketch);
        }
        {
            var Q0;
            Q0 = qSketchRegion(id + "F8", true);
            extrude(context, id + "F9", {"entities" : qUnion([Q0]), "operationType" : NewBodyOperationType.REMOVE, "oppositeDirection" : true, "depth" : 25.4 * mm});
        }
    });
